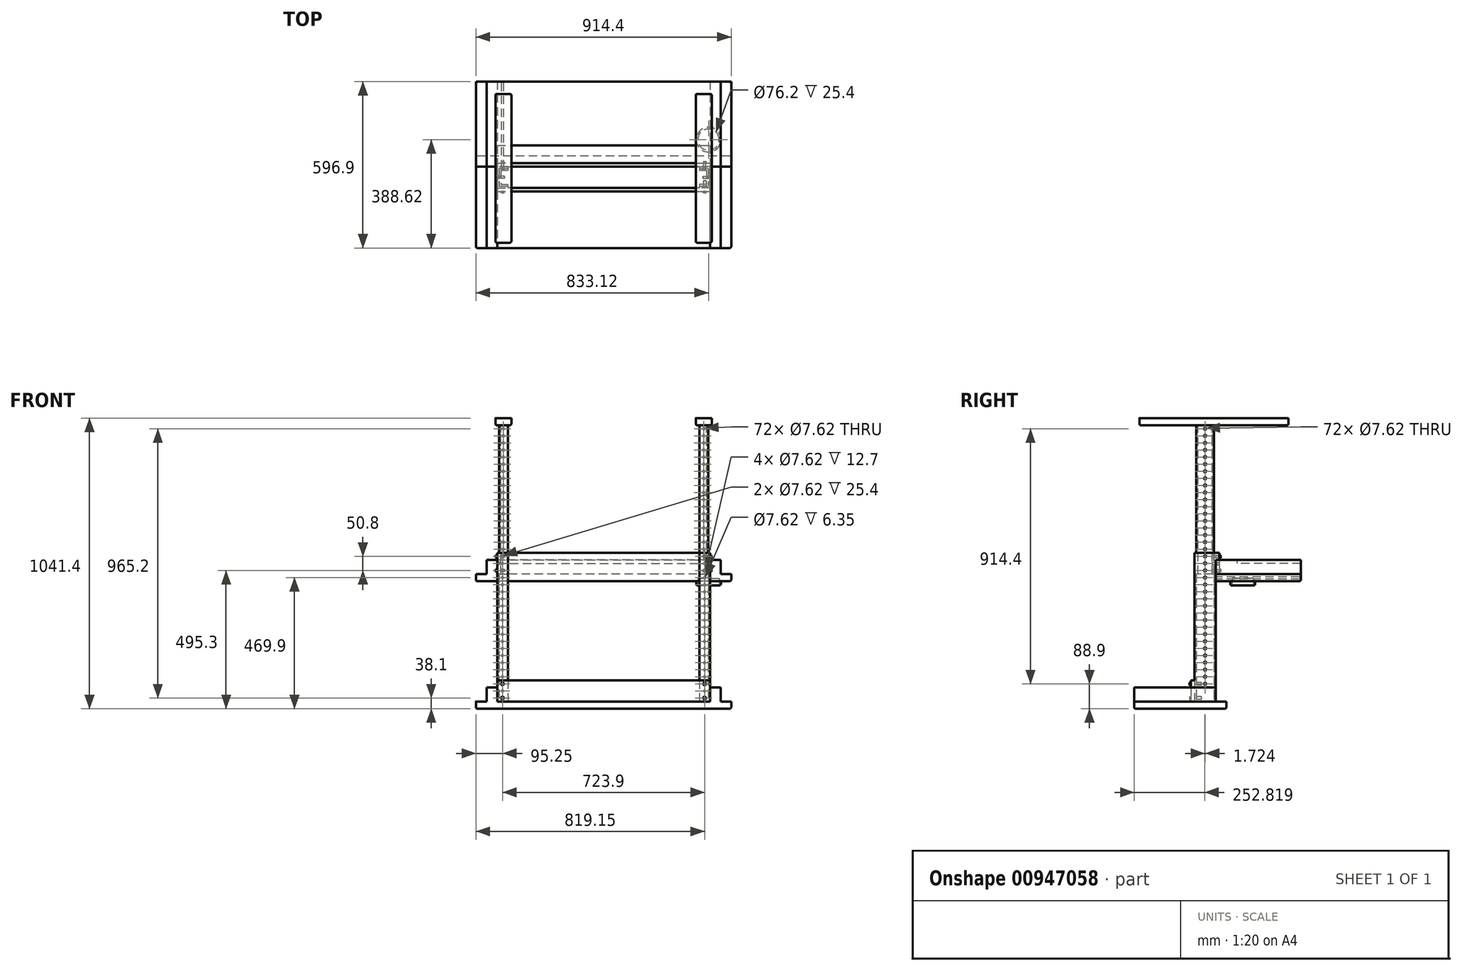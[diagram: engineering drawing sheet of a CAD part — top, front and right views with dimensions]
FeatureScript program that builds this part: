
annotation { "Feature Type Name" : "Feature", "Feature Type Description" : "" }
export const myFeature = defineFeature(function(context is Context, id is Id, definition is map)
    precondition{}
    {
        {
            var Q0;
            Q0=qCreatedBy(makeId("Top.planeOp"),FACE);
            var sketch = newSketch(context, id + "F0", { "sketchPlane" : qUnion([Q0])});
            skLineSegment(sketch, "E0.bottom", {"start": v(457.2, -165.1) * mm, "end": v(-457.2, -165.1) * mm});
            skLineSegment(sketch, "E0.top", {"start": v(457.2, 165.1) * mm, "end": v(-457.2, 165.1) * mm});
            skLineSegment(sketch, "E0.left", {"start": v(457.2, -165.1) * mm, "end": v(457.2, 165.1) * mm});
            skLineSegment(sketch, "E0.right", {"start": v(-457.2, -165.1) * mm, "end": v(-457.2, 165.1) * mm});
            skPoint(sketch, "E0.middle", {"position": v(0, 0) * mm});
            skSolve(sketch);
        }
        {
            var Q0;
            Q0=makeQuery(id+"F0.imprint","IMPRINT",FACE,{"disambiguationData":[TD([[makeQuery(id+"F0.imprint","IMPRINT",EDGE,{"derivedFrom":sQuery(id+"F0.wireOp",EDGE,"E0.bottom")}),-1.0]])]});
            extrude(context, id + "F1", {"entities" : qUnion([Q0]), "depth" : 25.4 * mm, "offsetDistance" : 25.4 * mm});
        }
        {
            var Q0;
            Q0=makeQuery(id+"F1.opExtrude","CAP_FACE",FACE,{"disambiguationData":[OSD([sQuery(id+"F0.wireOp",EDGE,"E0.bottom"),sQuery(id+"F0.wireOp",EDGE,"E0.top"),sQuery(id+"F0.wireOp",EDGE,"E0.left"),sQuery(id+"F0.wireOp",EDGE,"E0.right")])],"isStart":false});
            var sketch = newSketch(context, id + "F2", { "sketchPlane" : qUnion([Q0])});
            skLineSegment(sketch, "E1.bottom", {"start": v(-457.2, 165.1) * mm, "end": v(-381, 165.1) * mm});
            skLineSegment(sketch, "E1.top", {"start": v(-457.2, -165.1) * mm, "end": v(-381, -165.1) * mm});
            skLineSegment(sketch, "E1.left", {"start": v(-457.2, 165.1) * mm, "end": v(-457.2, -165.1) * mm});
            skLineSegment(sketch, "E1.right", {"start": v(-381, 165.1) * mm, "end": v(-381, -165.1) * mm});
            skLineSegment(sketch, "E2.bottom", {"start": v(457.2, -165.1) * mm, "end": v(381, -165.1) * mm});
            skLineSegment(sketch, "E2.top", {"start": v(457.2, 165.1) * mm, "end": v(381, 165.1) * mm});
            skLineSegment(sketch, "E2.left", {"start": v(457.2, -165.1) * mm, "end": v(457.2, 165.1) * mm});
            skLineSegment(sketch, "E2.right", {"start": v(381, -165.1) * mm, "end": v(381, 165.1) * mm});
            skLineSegment(sketch, "E3.bottom", {"start": v(-381, -165.1) * mm, "end": v(-419.1, -165.1) * mm});
            skLineSegment(sketch, "E3.top", {"start": v(-381, 165.1) * mm, "end": v(-419.1, 165.1) * mm});
            skLineSegment(sketch, "E3.left", {"start": v(-381, -165.1) * mm, "end": v(-381, 165.1) * mm});
            skLineSegment(sketch, "E3.right", {"start": v(-419.1, -165.1) * mm, "end": v(-419.1, 165.1) * mm});
            skLineSegment(sketch, "E4.bottom", {"start": v(381, 165.1) * mm, "end": v(419.1, 165.1) * mm});
            skLineSegment(sketch, "E4.top", {"start": v(381, -165.1) * mm, "end": v(419.1, -165.1) * mm});
            skLineSegment(sketch, "E4.left", {"start": v(381, 165.1) * mm, "end": v(381, -165.1) * mm});
            skLineSegment(sketch, "E4.right", {"start": v(419.1, 165.1) * mm, "end": v(419.1, -165.1) * mm});
            skLineSegment(sketch, "E5.bottom", {"start": v(-457.2, 165.1) * mm, "end": v(457.2, 165.1) * mm});
            skLineSegment(sketch, "E5.top", {"start": v(-457.2, 127) * mm, "end": v(457.2, 127) * mm});
            skLineSegment(sketch, "E5.left", {"start": v(-457.2, 165.1) * mm, "end": v(-457.2, 127) * mm});
            skLineSegment(sketch, "E5.right", {"start": v(457.2, 165.1) * mm, "end": v(457.2, 127) * mm});
            skLineSegment(sketch, "E6.bottom", {"start": v(-381, 127) * mm, "end": v(-342.9, 127) * mm});
            skLineSegment(sketch, "E6.top", {"start": v(-381, 50.8) * mm, "end": v(-342.9, 50.8) * mm});
            skLineSegment(sketch, "E6.left", {"start": v(-381, 127) * mm, "end": v(-381, 50.8) * mm});
            skLineSegment(sketch, "E6.right", {"start": v(-342.9, 127) * mm, "end": v(-342.9, 50.8) * mm});
            skLineSegment(sketch, "E7.bottom", {"start": v(381, 127) * mm, "end": v(342.9, 127) * mm});
            skLineSegment(sketch, "E7.top", {"start": v(381, 50.8) * mm, "end": v(342.9, 50.8) * mm});
            skLineSegment(sketch, "E7.left", {"start": v(381, 127) * mm, "end": v(381, 50.8) * mm});
            skLineSegment(sketch, "E7.right", {"start": v(342.9, 127) * mm, "end": v(342.9, 50.8) * mm});
            skLineSegment(sketch, "E8.bottom", {"start": v(342.9, 127) * mm, "end": v(381, 127) * mm});
            skLineSegment(sketch, "E8.top", {"start": v(342.9, 120.65) * mm, "end": v(381, 120.65) * mm});
            skLineSegment(sketch, "E8.left", {"start": v(342.9, 127) * mm, "end": v(342.9, 120.65) * mm});
            skLineSegment(sketch, "E8.right", {"start": v(381, 127) * mm, "end": v(381, 120.65) * mm});
            skLineSegment(sketch, "E9.bottom", {"start": v(342.9, 50.8) * mm, "end": v(381, 50.8) * mm});
            skLineSegment(sketch, "E9.top", {"start": v(342.9, 57.15) * mm, "end": v(381, 57.15) * mm});
            skLineSegment(sketch, "E9.left", {"start": v(342.9, 50.8) * mm, "end": v(342.9, 57.15) * mm});
            skLineSegment(sketch, "E9.right", {"start": v(381, 50.8) * mm, "end": v(381, 57.15) * mm});
            skLineSegment(sketch, "E10.bottom", {"start": v(381, 120.65) * mm, "end": v(374.65, 120.65) * mm});
            skLineSegment(sketch, "E10.top", {"start": v(381, 57.15) * mm, "end": v(374.65, 57.15) * mm});
            skLineSegment(sketch, "E10.left", {"start": v(381, 120.65) * mm, "end": v(381, 57.15) * mm});
            skLineSegment(sketch, "E10.right", {"start": v(374.65, 120.65) * mm, "end": v(374.65, 57.15) * mm});
            skLineSegment(sketch, "E11.top", {"start": v(-381, 120.65) * mm, "end": v(-342.9, 120.65) * mm});
            skLineSegment(sketch, "E11.left", {"start": v(-381, 127) * mm, "end": v(-381, 120.65) * mm});
            skLineSegment(sketch, "E11.right", {"start": v(-342.9, 127) * mm, "end": v(-342.9, 120.65) * mm});
            skLineSegment(sketch, "E12.top", {"start": v(-381, 57.15) * mm, "end": v(-342.9, 57.15) * mm});
            skLineSegment(sketch, "E12.left", {"start": v(-381, 50.8) * mm, "end": v(-381, 57.15) * mm});
            skLineSegment(sketch, "E12.right", {"start": v(-342.9, 50.8) * mm, "end": v(-342.9, 57.15) * mm});
            skLineSegment(sketch, "E13.bottom", {"start": v(-381, 120.65) * mm, "end": v(-374.65, 120.65) * mm});
            skLineSegment(sketch, "E13.top", {"start": v(-381, 57.15) * mm, "end": v(-374.65, 57.15) * mm});
            skLineSegment(sketch, "E13.left", {"start": v(-381, 120.65) * mm, "end": v(-381, 57.15) * mm});
            skLineSegment(sketch, "E13.right", {"start": v(-374.65, 120.65) * mm, "end": v(-374.65, 57.15) * mm});
            skLineSegment(sketch, "E14.bottom", {"start": v(-381, 50.8) * mm, "end": v(381, 50.8) * mm});
            skLineSegment(sketch, "E14.top", {"start": v(-381, 38.1) * mm, "end": v(381, 38.1) * mm});
            skLineSegment(sketch, "E14.left", {"start": v(-381, 50.8) * mm, "end": v(-381, 38.1) * mm});
            skLineSegment(sketch, "E14.right", {"start": v(381, 50.8) * mm, "end": v(381, 38.1) * mm});
            skSolve(sketch);
        }
        {
            var Q0;
            {var subQ0=sQuery(id+"F2.wireOp",EDGE,"E1.right");var subQ5=makeQuery(id+"F2.imprint","INTERSECT",VERTEX,{"derivedFrom":[subQ0,sQuery(id+"F2.wireOp",EDGE,"E11.top")]});Q0=makeQuery(id+"F2.imprint","IMPRINT",FACE,{"disambiguationData":[TD([[makeQuery(id+"F2.imprint","IMPRINT",EDGE,{"disambiguationData":[TD([[subQ5,-1.0]])],"derivedFrom":subQ0}),-1.0]])]});}
            var Q1;
            {var subQ0=sQuery(id+"F2.wireOp",EDGE,"E2.right");var subQ3=makeQuery(id+"F2.imprint","INTERSECT",VERTEX,{"derivedFrom":[subQ0,sQuery(id+"F2.wireOp",EDGE,"E8.top")]});Q1=makeQuery(id+"F2.imprint","IMPRINT",FACE,{"disambiguationData":[TD([[makeQuery(id+"F2.imprint","IMPRINT",EDGE,{"disambiguationData":[TD([[subQ3,1.0]])],"derivedFrom":subQ0}),-1.0]])]});}
            extrude(context, id + "F3", {"entities" : qUnion([Q0, Q1]), "operationType" : NewBodyOperationType.ADD, "depth" : 50.8 * mm, "offsetDistance" : 25.4 * mm});
        }
        {
            var Q0;
            {var subQ1=sQuery(id+"F2.wireOp",EDGE,"E6.top");Q0=makeQuery(id+"F2.imprint","IMPRINT",FACE,{"disambiguationData":[TD([[makeQuery(id+"F2.imprint","IMPRINT",EDGE,{"derivedFrom":subQ1}),-1.0]])]});}
            extrude(context, id + "F4", {"entities" : qUnion([Q0]), "operationType" : NewBodyOperationType.ADD, "depth" : 76.2 * mm, "offsetDistance" : 25.4 * mm});
        }
        {
            var Q0;
            {var subQ5=sQuery(id+"F2.wireOp",EDGE,"E13.right");Q0=makeQuery(id+"F2.imprint","IMPRINT",FACE,{"disambiguationData":[TD([[makeQuery(id+"F2.imprint","IMPRINT",EDGE,{"derivedFrom":subQ5}),-1.0]])]});}
            var Q1;
            {var subQ0=sQuery(id+"F2.wireOp",EDGE,"E11.top");var subQ6=sQuery(id+"F2.wireOp",EDGE,"E1.right");var subQ7=makeQuery(id+"F2.imprint","INTERSECT",VERTEX,{"derivedFrom":[subQ6,subQ0]});Q1=makeQuery(id+"F2.imprint","IMPRINT",FACE,{"disambiguationData":[TD([[makeQuery(id+"F2.imprint","IMPRINT",EDGE,{"disambiguationData":[TD([[subQ7,1.0]])],"derivedFrom":subQ6}),1.0]])]});}
            var Q2;
            {var subQ1=sQuery(id+"F2.wireOp",EDGE,"E6.top");Q2=makeQuery(id+"F2.imprint","IMPRINT",FACE,{"disambiguationData":[TD([[makeQuery(id+"F2.imprint","IMPRINT",EDGE,{"derivedFrom":subQ1}),1.0]])]});}
            var Q3;
            {var subQ4=sQuery(id+"F2.wireOp",EDGE,"E5.top");var subQ5=sQuery(id+"F2.wireOp",EDGE,"E2.right");var subQ6=makeQuery(id+"F2.imprint","INTERSECT",VERTEX,{"derivedFrom":[subQ5,subQ4]});Q3=makeQuery(id+"F2.imprint","IMPRINT",FACE,{"disambiguationData":[TD([[makeQuery(id+"F2.imprint","IMPRINT",EDGE,{"disambiguationData":[TD([[subQ6,1.0]])],"derivedFrom":subQ5}),1.0]])]});}
            var Q4;
            {var subQ5=sQuery(id+"F2.wireOp",EDGE,"E10.right");Q4=makeQuery(id+"F2.imprint","IMPRINT",FACE,{"disambiguationData":[TD([[makeQuery(id+"F2.imprint","IMPRINT",EDGE,{"derivedFrom":subQ5}),1.0]])]});}
            var Q5;
            {var subQ4=sQuery(id+"F2.wireOp",EDGE,"E7.top");Q5=makeQuery(id+"F2.imprint","IMPRINT",FACE,{"disambiguationData":[TD([[makeQuery(id+"F2.imprint","IMPRINT",EDGE,{"derivedFrom":subQ4}),-1.0]])]});}
            extrude(context, id + "F5", {"entities" : qUnion([Q0, Q1, Q2, Q3, Q4, Q5]), "operationType" : NewBodyOperationType.ADD, "depth" : 533.4 * mm, "offsetDistance" : 25.4 * mm});
        }
        {
            var Q0;
            Q0=makeQuery(id+"F4.opExtrude","SWEPT_FACE",FACE,{"disambiguationData":[OSD([sQuery(id+"F2.wireOp",EDGE,"E14.top")])]});
            var sketch = newSketch(context, id + "F6", { "sketchPlane" : qUnion([Q0])});
            skLineSegment(sketch, "E15.bottom", {"start": v(-381, 25.4) * mm, "end": v(-342.9, 25.4) * mm});
            skLineSegment(sketch, "E15.top", {"start": v(-381, 101.6) * mm, "end": v(-342.9, 101.6) * mm});
            skLineSegment(sketch, "E15.left", {"start": v(-381, 25.4) * mm, "end": v(-381, 101.6) * mm});
            skLineSegment(sketch, "E15.right", {"start": v(-342.9, 25.4) * mm, "end": v(-342.9, 101.6) * mm});
            skLineSegment(sketch, "E16.bottom", {"start": v(-342.9, 25.4) * mm, "end": v(-381, 25.4) * mm});
            skLineSegment(sketch, "E16.top", {"start": v(-342.9, 50.8) * mm, "end": v(-381, 50.8) * mm});
            skLineSegment(sketch, "E16.left", {"start": v(-342.9, 25.4) * mm, "end": v(-342.9, 50.8) * mm});
            skLineSegment(sketch, "E16.right", {"start": v(-381, 25.4) * mm, "end": v(-381, 50.8) * mm});
            skLineSegment(sketch, "E17.top", {"start": v(-342.9, 76.2) * mm, "end": v(-381, 76.2) * mm});
            skLineSegment(sketch, "E17.left", {"start": v(-342.9, 50.8) * mm, "end": v(-342.9, 76.2) * mm});
            skLineSegment(sketch, "E17.right", {"start": v(-381, 50.8) * mm, "end": v(-381, 76.2) * mm});
            skCircle(sketch, "E18", {"center": v(-361.95, 38.1) * mm, "radius": 5.08 * mm});
            skCircle(sketch, "E19", {"center": v(-361.95, 88.9) * mm, "radius": 5.08 * mm});
            skLineSegment(sketch, "E20.bottom", {"start": v(381, 101.6) * mm, "end": v(342.9, 101.6) * mm});
            skLineSegment(sketch, "E20.top", {"start": v(381, 25.4) * mm, "end": v(342.9, 25.4) * mm});
            skLineSegment(sketch, "E20.left", {"start": v(381, 101.6) * mm, "end": v(381, 25.4) * mm});
            skLineSegment(sketch, "E20.right", {"start": v(342.9, 101.6) * mm, "end": v(342.9, 25.4) * mm});
            skLineSegment(sketch, "E21.bottom", {"start": v(342.9, 101.6) * mm, "end": v(381, 101.6) * mm});
            skLineSegment(sketch, "E21.top", {"start": v(342.9, 76.2) * mm, "end": v(381, 76.2) * mm});
            skLineSegment(sketch, "E21.left", {"start": v(342.9, 101.6) * mm, "end": v(342.9, 76.2) * mm});
            skLineSegment(sketch, "E21.right", {"start": v(381, 101.6) * mm, "end": v(381, 76.2) * mm});
            skLineSegment(sketch, "E22.top", {"start": v(342.9, 50.8) * mm, "end": v(381, 50.8) * mm});
            skLineSegment(sketch, "E22.left", {"start": v(342.9, 76.2) * mm, "end": v(342.9, 50.8) * mm});
            skLineSegment(sketch, "E22.right", {"start": v(381, 76.2) * mm, "end": v(381, 50.8) * mm});
            skCircle(sketch, "E23", {"center": v(361.95, 88.9) * mm, "radius": 5.08 * mm});
            skCircle(sketch, "E24", {"center": v(361.95, 38.1) * mm, "radius": 5.08 * mm});
            skSolve(sketch);
        }
        {
            var Q0;
            Q0=makeQuery(id+"F6.imprint","IMPRINT",FACE,{"disambiguationData":[TD([[makeQuery(id+"F6.imprint","IMPRINT",EDGE,{"derivedFrom":sQuery(id+"F6.wireOp",EDGE,"E19")}),1.0]])]});
            var Q1;
            Q1=makeQuery(id+"F6.imprint","IMPRINT",FACE,{"disambiguationData":[TD([[makeQuery(id+"F6.imprint","IMPRINT",EDGE,{"derivedFrom":sQuery(id+"F6.wireOp",EDGE,"E18")}),1.0]])]});
            var Q2;
            Q2=makeQuery(id+"F6.imprint","IMPRINT",FACE,{"disambiguationData":[TD([[makeQuery(id+"F6.imprint","IMPRINT",EDGE,{"derivedFrom":sQuery(id+"F6.wireOp",EDGE,"E23")}),1.0]])]});
            var Q3;
            Q3=makeQuery(id+"F6.imprint","IMPRINT",FACE,{"disambiguationData":[TD([[makeQuery(id+"F6.imprint","IMPRINT",EDGE,{"derivedFrom":sQuery(id+"F6.wireOp",EDGE,"E24")}),1.0]])]});
            extrude(context, id + "F7", {"entities" : qUnion([Q0, Q1, Q2, Q3]), "operationType" : NewBodyOperationType.ADD, "depth" : 5.08 * mm, "offsetDistance" : 25.4 * mm});
        }
        {
            var Q0;
            Q0=makeQuery(id+"F5.opExtrude","CAP_FACE",FACE,{"disambiguationData":[OSD([sQuery(id+"F2.wireOp",EDGE,"E2.right"),sQuery(id+"F2.wireOp",EDGE,"E5.top"),sQuery(id+"F2.wireOp",EDGE,"E7.top"),sQuery(id+"F2.wireOp",EDGE,"E7.right"),sQuery(id+"F2.wireOp",EDGE,"E8.top"),sQuery(id+"F2.wireOp",EDGE,"E9.top"),sQuery(id+"F2.wireOp",EDGE,"E10.right")])],"isStart":false});
            var sketch = newSketch(context, id + "F8", { "sketchPlane" : qUnion([Q0])});
            skLineSegment(sketch, "E25.bottom", {"start": v(342.9, 120.65) * mm, "end": v(374.65, 120.65) * mm});
            skLineSegment(sketch, "E25.top", {"start": v(342.9, 57.15) * mm, "end": v(374.65, 57.15) * mm});
            skLineSegment(sketch, "E25.left", {"start": v(342.9, 120.65) * mm, "end": v(342.9, 57.15) * mm});
            skLineSegment(sketch, "E25.right", {"start": v(374.65, 120.65) * mm, "end": v(374.65, 57.15) * mm});
            skLineSegment(sketch, "E26.top", {"start": v(342.9, 114.3) * mm, "end": v(374.65, 114.3) * mm});
            skLineSegment(sketch, "E26.left", {"start": v(342.9, 120.65) * mm, "end": v(342.9, 114.3) * mm});
            skLineSegment(sketch, "E26.right", {"start": v(374.65, 120.65) * mm, "end": v(374.65, 114.3) * mm});
            skLineSegment(sketch, "E27.bottom", {"start": v(374.65, 120.65) * mm, "end": v(368.3, 120.65) * mm});
            skLineSegment(sketch, "E27.top", {"start": v(374.65, 57.15) * mm, "end": v(368.3, 57.15) * mm});
            skLineSegment(sketch, "E27.right", {"start": v(368.3, 120.65) * mm, "end": v(368.3, 57.15) * mm});
            skLineSegment(sketch, "E28.bottom", {"start": v(374.65, 57.15) * mm, "end": v(342.9, 57.15) * mm});
            skLineSegment(sketch, "E28.top", {"start": v(374.65, 63.5) * mm, "end": v(342.9, 63.5) * mm});
            skLineSegment(sketch, "E28.left", {"start": v(374.65, 57.15) * mm, "end": v(374.65, 63.5) * mm});
            skLineSegment(sketch, "E28.right", {"start": v(342.9, 57.15) * mm, "end": v(342.9, 63.5) * mm});
            skSolve(sketch);
        }
        {
            var Q0;
            {var subQ0=sQuery(id+"F8.wireOp",EDGE,"E25.left");var subQ6=sQuery(id+"F8.wireOp",EDGE,"E26.top");var subQ7=makeQuery(id+"F8.imprint","INTERSECT",VERTEX,{"derivedFrom":[subQ0,subQ6]});Q0=makeQuery(id+"F8.imprint","IMPRINT",FACE,{"disambiguationData":[TD([[makeQuery(id+"F8.imprint","IMPRINT",EDGE,{"disambiguationData":[TD([[subQ7,-1.0]])],"derivedFrom":subQ6}),1.0]])]});}
            var Q1;
            {var subQ1=sQuery(id+"F8.wireOp",EDGE,"E25.top");var subQ4=sQuery(id+"F8.wireOp",EDGE,"E27.right");var subQ5=makeQuery(id+"F8.imprint","INTERSECT",VERTEX,{"derivedFrom":[subQ1,subQ4]});Q1=makeQuery(id+"F8.imprint","IMPRINT",FACE,{"disambiguationData":[TD([[makeQuery(id+"F8.imprint","IMPRINT",EDGE,{"disambiguationData":[TD([[subQ5,1.0]])],"derivedFrom":subQ4}),-1.0]])]});}
            var Q2;
            {var subQ0=sQuery(id+"F8.wireOp",EDGE,"E25.right");var subQ1=sQuery(id+"F8.wireOp",EDGE,"E25.top");var subQ2=makeQuery(id+"F8.imprint","INTERSECT",VERTEX,{"derivedFrom":[subQ1,subQ0]});Q2=makeQuery(id+"F8.imprint","IMPRINT",FACE,{"disambiguationData":[TD([[makeQuery(id+"F8.imprint","IMPRINT",EDGE,{"disambiguationData":[TD([[subQ2,1.0]])],"derivedFrom":subQ1}),1.0]])]});}
            var Q3;
            {var subQ0=sQuery(id+"F8.wireOp",EDGE,"E26.top");var subQ1=sQuery(id+"F8.wireOp",EDGE,"E25.right");var subQ2=makeQuery(id+"F8.imprint","INTERSECT",VERTEX,{"derivedFrom":[subQ1,subQ0]});Q3=makeQuery(id+"F8.imprint","IMPRINT",FACE,{"disambiguationData":[TD([[makeQuery(id+"F8.imprint","IMPRINT",EDGE,{"disambiguationData":[TD([[subQ2,-1.0]])],"derivedFrom":subQ1}),-1.0]])]});}
            var Q4;
            {var subQ0=sQuery(id+"F8.wireOp",EDGE,"E25.right");var subQ1=sQuery(id+"F8.wireOp",EDGE,"E25.bottom");var subQ2=makeQuery(id+"F8.imprint","INTERSECT",VERTEX,{"derivedFrom":[subQ1,subQ0]});Q4=makeQuery(id+"F8.imprint","IMPRINT",FACE,{"disambiguationData":[TD([[makeQuery(id+"F8.imprint","IMPRINT",EDGE,{"disambiguationData":[TD([[subQ2,1.0]])],"derivedFrom":subQ1}),-1.0]])]});}
            extrude(context, id + "F9", {"entities" : qUnion([Q0, Q1, Q2, Q3, Q4]), "operationType" : NewBodyOperationType.ADD, "depth" : -76.2 * mm, "offsetDistance" : 25.4 * mm});
        }
        {
            var Q0;
            {var subQ0=sQuery(id+"F8.wireOp",EDGE,"E25.left");var subQ6=sQuery(id+"F8.wireOp",EDGE,"E26.top");var subQ7=makeQuery(id+"F8.imprint","INTERSECT",VERTEX,{"derivedFrom":[subQ0,subQ6]});Q0=makeQuery(id+"F8.imprint","IMPRINT",FACE,{"disambiguationData":[TD([[makeQuery(id+"F8.imprint","IMPRINT",EDGE,{"disambiguationData":[TD([[subQ7,-1.0]])],"derivedFrom":subQ6}),1.0]])]});}
            var Q1;
            {var subQ0=sQuery(id+"F8.wireOp",EDGE,"E25.right");var subQ1=sQuery(id+"F8.wireOp",EDGE,"E25.bottom");var subQ2=makeQuery(id+"F8.imprint","INTERSECT",VERTEX,{"derivedFrom":[subQ1,subQ0]});Q1=makeQuery(id+"F8.imprint","IMPRINT",FACE,{"disambiguationData":[TD([[makeQuery(id+"F8.imprint","IMPRINT",EDGE,{"disambiguationData":[TD([[subQ2,1.0]])],"derivedFrom":subQ1}),-1.0]])]});}
            var Q2;
            {var subQ0=sQuery(id+"F8.wireOp",EDGE,"E26.top");var subQ1=sQuery(id+"F8.wireOp",EDGE,"E25.right");var subQ2=makeQuery(id+"F8.imprint","INTERSECT",VERTEX,{"derivedFrom":[subQ1,subQ0]});Q2=makeQuery(id+"F8.imprint","IMPRINT",FACE,{"disambiguationData":[TD([[makeQuery(id+"F8.imprint","IMPRINT",EDGE,{"disambiguationData":[TD([[subQ2,-1.0]])],"derivedFrom":subQ1}),-1.0]])]});}
            var Q3;
            {var subQ0=sQuery(id+"F8.wireOp",EDGE,"E25.right");var subQ1=sQuery(id+"F8.wireOp",EDGE,"E25.top");var subQ2=makeQuery(id+"F8.imprint","INTERSECT",VERTEX,{"derivedFrom":[subQ1,subQ0]});Q3=makeQuery(id+"F8.imprint","IMPRINT",FACE,{"disambiguationData":[TD([[makeQuery(id+"F8.imprint","IMPRINT",EDGE,{"disambiguationData":[TD([[subQ2,1.0]])],"derivedFrom":subQ1}),1.0]])]});}
            var Q4;
            {var subQ1=sQuery(id+"F8.wireOp",EDGE,"E25.top");var subQ4=sQuery(id+"F8.wireOp",EDGE,"E27.right");var subQ5=makeQuery(id+"F8.imprint","INTERSECT",VERTEX,{"derivedFrom":[subQ1,subQ4]});Q4=makeQuery(id+"F8.imprint","IMPRINT",FACE,{"disambiguationData":[TD([[makeQuery(id+"F8.imprint","IMPRINT",EDGE,{"disambiguationData":[TD([[subQ5,1.0]])],"derivedFrom":subQ4}),-1.0]])]});}
            extrude(context, id + "F10", {"entities" : qUnion([Q0, Q1, Q2, Q3, Q4]), "operationType" : NewBodyOperationType.ADD, "depth" : 457.2 * mm, "offsetDistance" : 25.4 * mm});
        }
        {
            var Q0;
            Q0=makeQuery(id+"F5.opExtrude","CAP_FACE",FACE,{"disambiguationData":[OSD([sQuery(id+"F2.wireOp",EDGE,"E1.right"),sQuery(id+"F2.wireOp",EDGE,"E5.top"),sQuery(id+"F2.wireOp",EDGE,"E6.top"),sQuery(id+"F2.wireOp",EDGE,"E6.right"),sQuery(id+"F2.wireOp",EDGE,"E11.top"),sQuery(id+"F2.wireOp",EDGE,"E12.top"),sQuery(id+"F2.wireOp",EDGE,"E13.right")])],"isStart":false});
            var sketch = newSketch(context, id + "F11", { "sketchPlane" : qUnion([Q0])});
            skLineSegment(sketch, "E29.bottom", {"start": v(-374.65, 120.65) * mm, "end": v(-342.86, 120.65) * mm});
            skLineSegment(sketch, "E29.top", {"start": v(-374.65, 114.3) * mm, "end": v(-342.86, 114.3) * mm});
            skLineSegment(sketch, "E29.left", {"start": v(-374.65, 120.65) * mm, "end": v(-374.65, 114.3) * mm});
            skLineSegment(sketch, "E29.right", {"start": v(-342.86, 120.65) * mm, "end": v(-342.86, 114.3) * mm});
            skLineSegment(sketch, "E30.bottom", {"start": v(-374.65, 120.65) * mm, "end": v(-368.3, 120.65) * mm});
            skLineSegment(sketch, "E30.top", {"start": v(-374.65, 57.15) * mm, "end": v(-368.3, 57.15) * mm});
            skLineSegment(sketch, "E30.left", {"start": v(-374.65, 120.65) * mm, "end": v(-374.65, 57.15) * mm});
            skLineSegment(sketch, "E30.right", {"start": v(-368.3, 120.65) * mm, "end": v(-368.3, 57.15) * mm});
            skLineSegment(sketch, "E31.bottom", {"start": v(-374.65, 57.15) * mm, "end": v(-342.9, 57.15) * mm});
            skLineSegment(sketch, "E31.top", {"start": v(-374.65, 63.5) * mm, "end": v(-342.9, 63.5) * mm});
            skLineSegment(sketch, "E31.left", {"start": v(-374.65, 57.15) * mm, "end": v(-374.65, 63.5) * mm});
            skLineSegment(sketch, "E31.right", {"start": v(-342.9, 57.15) * mm, "end": v(-342.9, 63.5) * mm});
            skSolve(sketch);
        }
        {
            var Q0;
            {var subQ0=sQuery(id+"F11.wireOp",EDGE,"E29.left");Q0=makeQuery(id+"F11.imprint","IMPRINT",FACE,{"disambiguationData":[TD([[makeQuery(id+"F11.imprint","IMPRINT",EDGE,{"derivedFrom":subQ0}),1.0]])]});}
            var Q1;
            {var subQ3=sQuery(id+"F11.wireOp",EDGE,"E29.right");Q1=makeQuery(id+"F11.imprint","IMPRINT",FACE,{"disambiguationData":[TD([[makeQuery(id+"F11.imprint","IMPRINT",EDGE,{"derivedFrom":subQ3}),-1.0]])]});}
            var Q2;
            {var subQ0=sQuery(id+"F11.wireOp",EDGE,"E30.right");var subQ1=sQuery(id+"F11.wireOp",EDGE,"E29.top");var subQ2=makeQuery(id+"F11.imprint","INTERSECT",VERTEX,{"derivedFrom":[subQ1,subQ0]});Q2=makeQuery(id+"F11.imprint","IMPRINT",FACE,{"disambiguationData":[TD([[makeQuery(id+"F11.imprint","IMPRINT",EDGE,{"disambiguationData":[TD([[subQ2,-1.0]])],"derivedFrom":subQ0}),-1.0]])]});}
            var Q3;
            {var subQ0=sQuery(id+"F11.wireOp",EDGE,"E30.top");Q3=makeQuery(id+"F11.imprint","IMPRINT",FACE,{"disambiguationData":[TD([[makeQuery(id+"F11.imprint","IMPRINT",EDGE,{"derivedFrom":subQ0}),1.0]])]});}
            var Q4;
            {var subQ0=sQuery(id+"F11.wireOp",EDGE,"E31.bottom");Q4=makeQuery(id+"F11.imprint","IMPRINT",FACE,{"disambiguationData":[TD([[makeQuery(id+"F11.imprint","IMPRINT",EDGE,{"derivedFrom":subQ0}),1.0]])]});}
            extrude(context, id + "F12", {"entities" : qUnion([Q0, Q1, Q2, Q3, Q4]), "operationType" : NewBodyOperationType.ADD, "depth" : -76.2 * mm, "offsetDistance" : 25.4 * mm});
        }
        {
            var Q0;
            {var subQ3=sQuery(id+"F11.wireOp",EDGE,"E29.right");Q0=makeQuery(id+"F11.imprint","IMPRINT",FACE,{"disambiguationData":[TD([[makeQuery(id+"F11.imprint","IMPRINT",EDGE,{"derivedFrom":subQ3}),-1.0]])]});}
            var Q1;
            {var subQ0=sQuery(id+"F11.wireOp",EDGE,"E29.left");Q1=makeQuery(id+"F11.imprint","IMPRINT",FACE,{"disambiguationData":[TD([[makeQuery(id+"F11.imprint","IMPRINT",EDGE,{"derivedFrom":subQ0}),1.0]])]});}
            var Q2;
            {var subQ0=sQuery(id+"F11.wireOp",EDGE,"E30.right");var subQ1=sQuery(id+"F11.wireOp",EDGE,"E29.top");var subQ2=makeQuery(id+"F11.imprint","INTERSECT",VERTEX,{"derivedFrom":[subQ1,subQ0]});Q2=makeQuery(id+"F11.imprint","IMPRINT",FACE,{"disambiguationData":[TD([[makeQuery(id+"F11.imprint","IMPRINT",EDGE,{"disambiguationData":[TD([[subQ2,-1.0]])],"derivedFrom":subQ0}),-1.0]])]});}
            var Q3;
            {var subQ0=sQuery(id+"F11.wireOp",EDGE,"E30.top");Q3=makeQuery(id+"F11.imprint","IMPRINT",FACE,{"disambiguationData":[TD([[makeQuery(id+"F11.imprint","IMPRINT",EDGE,{"derivedFrom":subQ0}),1.0]])]});}
            var Q4;
            {var subQ0=sQuery(id+"F11.wireOp",EDGE,"E31.bottom");Q4=makeQuery(id+"F11.imprint","IMPRINT",FACE,{"disambiguationData":[TD([[makeQuery(id+"F11.imprint","IMPRINT",EDGE,{"derivedFrom":subQ0}),1.0]])]});}
            extrude(context, id + "F13", {"entities" : qUnion([Q0, Q1, Q2, Q3, Q4]), "operationType" : NewBodyOperationType.ADD, "depth" : 457.2 * mm, "offsetDistance" : 25.4 * mm});
        }
        {
            var Q0;
            {var subQ0=sQuery(id+"F2.wireOp",EDGE,"E1.right");Q0=makeQuery(id+"F5.boolean.opBoolean","MERGE",FACE,{"derivedFrom":[makeQuery(id+"F4.opExtrude","SWEPT_FACE",FACE,{"disambiguationData":[OSD([subQ0])]}),makeQuery(id+"F5.opExtrude","SWEPT_FACE",FACE,{"disambiguationData":[OSD([subQ0])]})]});}
            var sketch = newSketch(context, id + "F14", { "sketchPlane" : qUnion([Q0])});
            skLineSegment(sketch, "E32.bottom", {"start": v(-127, 558.8) * mm, "end": v(-50.8, 558.8) * mm});
            skLineSegment(sketch, "E32.top", {"start": v(-127, 533.4) * mm, "end": v(-50.8, 533.4) * mm});
            skLineSegment(sketch, "E32.left", {"start": v(-127, 558.8) * mm, "end": v(-127, 533.4) * mm});
            skLineSegment(sketch, "E32.right", {"start": v(-50.8, 558.8) * mm, "end": v(-50.8, 533.4) * mm});
            skLineSegment(sketch, "E33.top", {"start": v(-127, 508) * mm, "end": v(-50.8, 508) * mm});
            skLineSegment(sketch, "E33.left", {"start": v(-127, 533.4) * mm, "end": v(-127, 508) * mm});
            skLineSegment(sketch, "E33.right", {"start": v(-50.8, 533.4) * mm, "end": v(-50.8, 508) * mm});
            skLineSegment(sketch, "E34.top", {"start": v(-127, 482.6) * mm, "end": v(-50.8, 482.6) * mm});
            skLineSegment(sketch, "E34.left", {"start": v(-127, 508) * mm, "end": v(-127, 482.6) * mm});
            skLineSegment(sketch, "E34.right", {"start": v(-50.8, 508) * mm, "end": v(-50.8, 482.6) * mm});
            skLineSegment(sketch, "E35.top", {"start": v(-127, 457.2) * mm, "end": v(-50.8, 457.2) * mm});
            skLineSegment(sketch, "E35.left", {"start": v(-127, 482.6) * mm, "end": v(-127, 457.2) * mm});
            skLineSegment(sketch, "E35.right", {"start": v(-50.8, 482.6) * mm, "end": v(-50.8, 457.2) * mm});
            skLineSegment(sketch, "E36.bottom", {"start": v(-127, 457.2) * mm, "end": v(-48.44, 457.2) * mm});
            skLineSegment(sketch, "E36.top", {"start": v(-127, 431.8) * mm, "end": v(-48.44, 431.8) * mm});
            skLineSegment(sketch, "E36.left", {"start": v(-127, 457.2) * mm, "end": v(-127, 431.8) * mm});
            skLineSegment(sketch, "E36.right", {"start": v(-48.44, 457.2) * mm, "end": v(-48.44, 431.8) * mm});
            skLineSegment(sketch, "E37.bottom", {"start": v(-127, 431.8) * mm, "end": v(-50.8, 431.8) * mm});
            skLineSegment(sketch, "E37.top", {"start": v(-127, 406.4) * mm, "end": v(-50.8, 406.4) * mm});
            skLineSegment(sketch, "E37.left", {"start": v(-127, 431.8) * mm, "end": v(-127, 406.4) * mm});
            skLineSegment(sketch, "E37.right", {"start": v(-50.8, 431.8) * mm, "end": v(-50.8, 406.4) * mm});
            skLineSegment(sketch, "E38.bottom", {"start": v(-127, 406.4) * mm, "end": v(-48.44, 406.4) * mm});
            skLineSegment(sketch, "E38.top", {"start": v(-127, 381) * mm, "end": v(-48.44, 381) * mm});
            skLineSegment(sketch, "E38.left", {"start": v(-127, 406.4) * mm, "end": v(-127, 381) * mm});
            skLineSegment(sketch, "E38.right", {"start": v(-48.44, 406.4) * mm, "end": v(-48.44, 381) * mm});
            skLineSegment(sketch, "E39.bottom", {"start": v(-127, 381) * mm, "end": v(-50.8, 381) * mm});
            skLineSegment(sketch, "E39.top", {"start": v(-127, 355.6) * mm, "end": v(-50.8, 355.6) * mm});
            skLineSegment(sketch, "E39.left", {"start": v(-127, 381) * mm, "end": v(-127, 355.6) * mm});
            skLineSegment(sketch, "E39.right", {"start": v(-50.8, 381) * mm, "end": v(-50.8, 355.6) * mm});
            skLineSegment(sketch, "E40.top", {"start": v(-127, 330.2) * mm, "end": v(-50.8, 330.2) * mm});
            skLineSegment(sketch, "E40.left", {"start": v(-127, 355.6) * mm, "end": v(-127, 330.2) * mm});
            skLineSegment(sketch, "E40.right", {"start": v(-50.8, 355.6) * mm, "end": v(-50.8, 330.2) * mm});
            skLineSegment(sketch, "E41.top", {"start": v(-127, 304.8) * mm, "end": v(-50.8, 304.8) * mm});
            skLineSegment(sketch, "E41.left", {"start": v(-127, 330.2) * mm, "end": v(-127, 304.8) * mm});
            skLineSegment(sketch, "E41.right", {"start": v(-50.8, 330.2) * mm, "end": v(-50.8, 304.8) * mm});
            skLineSegment(sketch, "E42.bottom", {"start": v(-127, 304.8) * mm, "end": v(-48.44, 304.8) * mm});
            skLineSegment(sketch, "E42.top", {"start": v(-127, 279.4) * mm, "end": v(-48.44, 279.4) * mm});
            skLineSegment(sketch, "E42.left", {"start": v(-127, 304.8) * mm, "end": v(-127, 279.4) * mm});
            skLineSegment(sketch, "E42.right", {"start": v(-48.44, 304.8) * mm, "end": v(-48.44, 279.4) * mm});
            skLineSegment(sketch, "E43.bottom", {"start": v(-127, 279.4) * mm, "end": v(-50.8, 279.4) * mm});
            skLineSegment(sketch, "E43.top", {"start": v(-127, 254) * mm, "end": v(-50.8, 254) * mm});
            skLineSegment(sketch, "E43.left", {"start": v(-127, 279.4) * mm, "end": v(-127, 254) * mm});
            skLineSegment(sketch, "E43.right", {"start": v(-50.8, 279.4) * mm, "end": v(-50.8, 254) * mm});
            skLineSegment(sketch, "E44.top", {"start": v(-127, 228.6) * mm, "end": v(-50.8, 228.6) * mm});
            skLineSegment(sketch, "E44.left", {"start": v(-127, 254) * mm, "end": v(-127, 228.6) * mm});
            skLineSegment(sketch, "E44.right", {"start": v(-50.8, 254) * mm, "end": v(-50.8, 228.6) * mm});
            skLineSegment(sketch, "E45.top", {"start": v(-127, 203.2) * mm, "end": v(-50.8, 203.2) * mm});
            skLineSegment(sketch, "E45.left", {"start": v(-127, 228.6) * mm, "end": v(-127, 203.2) * mm});
            skLineSegment(sketch, "E45.right", {"start": v(-50.8, 228.6) * mm, "end": v(-50.8, 203.2) * mm});
            skLineSegment(sketch, "E46.top", {"start": v(-127, 177.8) * mm, "end": v(-50.8, 177.8) * mm});
            skLineSegment(sketch, "E46.left", {"start": v(-127, 203.2) * mm, "end": v(-127, 177.8) * mm});
            skLineSegment(sketch, "E46.right", {"start": v(-50.8, 203.2) * mm, "end": v(-50.8, 177.8) * mm});
            skLineSegment(sketch, "E47.top", {"start": v(-127, 152.4) * mm, "end": v(-50.8, 152.4) * mm});
            skLineSegment(sketch, "E47.left", {"start": v(-127, 177.8) * mm, "end": v(-127, 152.4) * mm});
            skLineSegment(sketch, "E47.right", {"start": v(-50.8, 177.8) * mm, "end": v(-50.8, 152.4) * mm});
            skLineSegment(sketch, "E48.top", {"start": v(-127, 127) * mm, "end": v(-50.8, 127) * mm});
            skLineSegment(sketch, "E48.left", {"start": v(-127, 152.4) * mm, "end": v(-127, 127) * mm});
            skLineSegment(sketch, "E48.right", {"start": v(-50.8, 152.4) * mm, "end": v(-50.8, 127) * mm});
            skLineSegment(sketch, "E49.top", {"start": v(-127, 101.6) * mm, "end": v(-50.8, 101.6) * mm});
            skLineSegment(sketch, "E49.left", {"start": v(-127, 127) * mm, "end": v(-127, 101.6) * mm});
            skLineSegment(sketch, "E49.right", {"start": v(-50.8, 127) * mm, "end": v(-50.8, 101.6) * mm});
            skLineSegment(sketch, "E50.top", {"start": v(-127, 76.2) * mm, "end": v(-50.8, 76.2) * mm});
            skLineSegment(sketch, "E50.left", {"start": v(-127, 101.6) * mm, "end": v(-127, 76.2) * mm});
            skLineSegment(sketch, "E50.right", {"start": v(-50.8, 101.6) * mm, "end": v(-50.8, 76.2) * mm});
            skCircle(sketch, "E51", {"center": v(-89.44, 190.68) * mm, "radius": 3.81 * mm});
            skCircle(sketch, "E52", {"center": v(-88.9, 165.1) * mm, "radius": 3.81 * mm});
            skCircle(sketch, "E53", {"center": v(-88.9, 139.7) * mm, "radius": 3.81 * mm});
            skCircle(sketch, "E54", {"center": v(-88.9, 114.3) * mm, "radius": 3.81 * mm});
            skCircle(sketch, "E55", {"center": v(-88.9, 88.9) * mm, "radius": 3.81 * mm});
            skCircle(sketch, "E56", {"center": v(-88.32, 317.7) * mm, "radius": 3.81 * mm});
            skCircle(sketch, "E57", {"center": v(-88.9, 292.1) * mm, "radius": 3.81 * mm});
            skCircle(sketch, "E58", {"center": v(-88.9, 266.7) * mm, "radius": 3.81 * mm});
            skCircle(sketch, "E59", {"center": v(-88.9, 241.3) * mm, "radius": 3.81 * mm});
            skCircle(sketch, "E60", {"center": v(-88.9, 215.9) * mm, "radius": 3.81 * mm});
            skCircle(sketch, "E61", {"center": v(-87.72, 368.3) * mm, "radius": 3.81 * mm});
            skCircle(sketch, "E62", {"center": v(-88.9, 342.9) * mm, "radius": 3.8 * mm});
            skCircle(sketch, "E63", {"center": v(-88.9, 393.7) * mm, "radius": 3.81 * mm});
            skCircle(sketch, "E64", {"center": v(-87.72, 418.7) * mm, "radius": 3.81 * mm});
            skPoint(sketch, "E64.centerSnap0", {"position": v(-87.72, 406.4) * mm});
            skCircle(sketch, "E65", {"center": v(-88.9, 444.5) * mm, "radius": 3.81 * mm});
            skCircle(sketch, "E66", {"center": v(-88.9, 469.9) * mm, "radius": 3.81 * mm});
            skCircle(sketch, "E67", {"center": v(-88.9, 495.3) * mm, "radius": 3.81 * mm});
            skCircle(sketch, "E68", {"center": v(-88.9, 546.1) * mm, "radius": 3.81 * mm});
            skCircle(sketch, "E69", {"center": v(-88.9, 520.7) * mm, "radius": 3.81 * mm});
            skLineSegment(sketch, "E70.bottom", {"start": v(-50.8, 76.2) * mm, "end": v(-127.37, 76.2) * mm});
            skSolve(sketch);
        }
        {
            var Q0;
            Q0=makeQuery(id+"F14.imprint","IMPRINT",FACE,{"disambiguationData":[TD([[makeQuery(id+"F14.imprint","IMPRINT",EDGE,{"derivedFrom":sQuery(id+"F14.wireOp",EDGE,"E55")}),1.0]])]});
            var Q1;
            Q1=makeQuery(id+"F14.imprint","IMPRINT",FACE,{"disambiguationData":[TD([[makeQuery(id+"F14.imprint","IMPRINT",EDGE,{"derivedFrom":sQuery(id+"F14.wireOp",EDGE,"E54")}),1.0]])]});
            var Q2;
            Q2=makeQuery(id+"F14.imprint","IMPRINT",FACE,{"disambiguationData":[TD([[makeQuery(id+"F14.imprint","IMPRINT",EDGE,{"derivedFrom":sQuery(id+"F14.wireOp",EDGE,"E53")}),1.0]])]});
            var Q3;
            Q3=makeQuery(id+"F14.imprint","IMPRINT",FACE,{"disambiguationData":[TD([[makeQuery(id+"F14.imprint","IMPRINT",EDGE,{"derivedFrom":sQuery(id+"F14.wireOp",EDGE,"E52")}),1.0]])]});
            var Q4;
            Q4=makeQuery(id+"F14.imprint","IMPRINT",FACE,{"disambiguationData":[TD([[makeQuery(id+"F14.imprint","IMPRINT",EDGE,{"derivedFrom":sQuery(id+"F14.wireOp",EDGE,"E51")}),1.0]])]});
            var Q5;
            Q5=makeQuery(id+"F14.imprint","IMPRINT",FACE,{"disambiguationData":[TD([[makeQuery(id+"F14.imprint","IMPRINT",EDGE,{"derivedFrom":sQuery(id+"F14.wireOp",EDGE,"E60")}),1.0]])]});
            var Q6;
            Q6=makeQuery(id+"F14.imprint","IMPRINT",FACE,{"disambiguationData":[TD([[makeQuery(id+"F14.imprint","IMPRINT",EDGE,{"derivedFrom":sQuery(id+"F14.wireOp",EDGE,"E59")}),1.0]])]});
            var Q7;
            Q7=makeQuery(id+"F14.imprint","IMPRINT",FACE,{"disambiguationData":[TD([[makeQuery(id+"F14.imprint","IMPRINT",EDGE,{"derivedFrom":sQuery(id+"F14.wireOp",EDGE,"E58")}),1.0]])]});
            var Q8;
            Q8=makeQuery(id+"F14.imprint","IMPRINT",FACE,{"disambiguationData":[TD([[makeQuery(id+"F14.imprint","IMPRINT",EDGE,{"derivedFrom":sQuery(id+"F14.wireOp",EDGE,"E57")}),1.0]])]});
            var Q9;
            Q9=makeQuery(id+"F14.imprint","IMPRINT",FACE,{"disambiguationData":[TD([[makeQuery(id+"F14.imprint","IMPRINT",EDGE,{"derivedFrom":sQuery(id+"F14.wireOp",EDGE,"E56")}),1.0]])]});
            var Q10;
            Q10=makeQuery(id+"F14.imprint","IMPRINT",FACE,{"disambiguationData":[TD([[makeQuery(id+"F14.imprint","IMPRINT",EDGE,{"derivedFrom":sQuery(id+"F14.wireOp",EDGE,"E62")}),1.0]])]});
            var Q11;
            Q11=makeQuery(id+"F14.imprint","IMPRINT",FACE,{"disambiguationData":[TD([[makeQuery(id+"F14.imprint","IMPRINT",EDGE,{"derivedFrom":sQuery(id+"F14.wireOp",EDGE,"E61")}),1.0]])]});
            var Q12;
            Q12=makeQuery(id+"F14.imprint","IMPRINT",FACE,{"disambiguationData":[TD([[makeQuery(id+"F14.imprint","IMPRINT",EDGE,{"derivedFrom":sQuery(id+"F14.wireOp",EDGE,"E63")}),1.0]])]});
            var Q13;
            Q13=makeQuery(id+"F14.imprint","IMPRINT",FACE,{"disambiguationData":[TD([[makeQuery(id+"F14.imprint","IMPRINT",EDGE,{"derivedFrom":sQuery(id+"F14.wireOp",EDGE,"E64")}),1.0]])]});
            var Q14;
            Q14=makeQuery(id+"F14.imprint","IMPRINT",FACE,{"disambiguationData":[TD([[makeQuery(id+"F14.imprint","IMPRINT",EDGE,{"derivedFrom":sQuery(id+"F14.wireOp",EDGE,"E65")}),1.0]])]});
            var Q15;
            Q15=makeQuery(id+"F14.imprint","IMPRINT",FACE,{"disambiguationData":[TD([[makeQuery(id+"F14.imprint","IMPRINT",EDGE,{"derivedFrom":sQuery(id+"F14.wireOp",EDGE,"E66")}),1.0]])]});
            var Q16;
            Q16=makeQuery(id+"F14.imprint","IMPRINT",FACE,{"disambiguationData":[TD([[makeQuery(id+"F14.imprint","IMPRINT",EDGE,{"derivedFrom":sQuery(id+"F14.wireOp",EDGE,"E69")}),1.0]])]});
            extrude(context, id + "F15", {"entities" : qUnion([Q0, Q1, Q2, Q3, Q4, Q5, Q6, Q7, Q8, Q9, Q10, Q11, Q12, Q13, Q14, Q15, Q16]), "operationType" : NewBodyOperationType.REMOVE, "oppositeDirection" : true, "depth" : 50.8 * mm, "offsetDistance" : 25.4 * mm});
        }
        {
            var Q0;
            {var subQ0=sQuery(id+"F2.wireOp",EDGE,"E2.right");Q0=makeQuery(id+"F5.boolean.opBoolean","MERGE",FACE,{"derivedFrom":[makeQuery(id+"F4.opExtrude","SWEPT_FACE",FACE,{"disambiguationData":[OSD([subQ0])]}),makeQuery(id+"F5.opExtrude","SWEPT_FACE",FACE,{"disambiguationData":[OSD([subQ0])]})]});}
            var sketch = newSketch(context, id + "F16", { "sketchPlane" : qUnion([Q0])});
            skLineSegment(sketch, "E71.bottom", {"start": v(127, 558.8) * mm, "end": v(50.8, 558.8) * mm});
            skLineSegment(sketch, "E71.top", {"start": v(127, 533.4) * mm, "end": v(50.8, 533.4) * mm});
            skLineSegment(sketch, "E71.left", {"start": v(127, 558.8) * mm, "end": v(127, 533.4) * mm});
            skLineSegment(sketch, "E71.right", {"start": v(50.8, 558.8) * mm, "end": v(50.8, 533.4) * mm});
            skLineSegment(sketch, "E72.top", {"start": v(127, 508) * mm, "end": v(50.8, 508) * mm});
            skLineSegment(sketch, "E72.left", {"start": v(127, 533.4) * mm, "end": v(127, 508) * mm});
            skLineSegment(sketch, "E72.right", {"start": v(50.8, 533.4) * mm, "end": v(50.8, 508) * mm});
            skLineSegment(sketch, "E73.top", {"start": v(127, 482.6) * mm, "end": v(50.8, 482.6) * mm});
            skLineSegment(sketch, "E73.left", {"start": v(127, 508) * mm, "end": v(127, 482.6) * mm});
            skLineSegment(sketch, "E73.right", {"start": v(50.8, 508) * mm, "end": v(50.8, 482.6) * mm});
            skLineSegment(sketch, "E74.top", {"start": v(127, 457.2) * mm, "end": v(50.8, 457.2) * mm});
            skLineSegment(sketch, "E74.left", {"start": v(127, 482.6) * mm, "end": v(127, 457.2) * mm});
            skLineSegment(sketch, "E74.right", {"start": v(50.8, 482.6) * mm, "end": v(50.8, 457.2) * mm});
            skLineSegment(sketch, "E75.top", {"start": v(127, 431.8) * mm, "end": v(50.8, 431.8) * mm});
            skLineSegment(sketch, "E75.left", {"start": v(127, 457.2) * mm, "end": v(127, 431.8) * mm});
            skLineSegment(sketch, "E75.right", {"start": v(50.8, 457.2) * mm, "end": v(50.8, 431.8) * mm});
            skLineSegment(sketch, "E76.top", {"start": v(127, 406.4) * mm, "end": v(50.8, 406.4) * mm});
            skLineSegment(sketch, "E76.left", {"start": v(127, 431.8) * mm, "end": v(127, 406.4) * mm});
            skLineSegment(sketch, "E76.right", {"start": v(50.8, 431.8) * mm, "end": v(50.8, 406.4) * mm});
            skLineSegment(sketch, "E77.top", {"start": v(127, 381) * mm, "end": v(50.8, 381) * mm});
            skLineSegment(sketch, "E77.left", {"start": v(127, 406.4) * mm, "end": v(127, 381) * mm});
            skLineSegment(sketch, "E77.right", {"start": v(50.8, 406.4) * mm, "end": v(50.8, 381) * mm});
            skLineSegment(sketch, "E78.top", {"start": v(127, 355.6) * mm, "end": v(50.8, 355.6) * mm});
            skLineSegment(sketch, "E78.left", {"start": v(127, 381) * mm, "end": v(127, 355.6) * mm});
            skLineSegment(sketch, "E78.right", {"start": v(50.8, 381) * mm, "end": v(50.8, 355.6) * mm});
            skLineSegment(sketch, "E79.top", {"start": v(127, 330.2) * mm, "end": v(50.8, 330.2) * mm});
            skLineSegment(sketch, "E79.left", {"start": v(127, 355.6) * mm, "end": v(127, 330.2) * mm});
            skLineSegment(sketch, "E79.right", {"start": v(50.8, 355.6) * mm, "end": v(50.8, 330.2) * mm});
            skLineSegment(sketch, "E80.top", {"start": v(127, 304.8) * mm, "end": v(50.8, 304.8) * mm});
            skLineSegment(sketch, "E80.left", {"start": v(127, 330.2) * mm, "end": v(127, 304.8) * mm});
            skLineSegment(sketch, "E80.right", {"start": v(50.8, 330.2) * mm, "end": v(50.8, 304.8) * mm});
            skLineSegment(sketch, "E81.top", {"start": v(127, 279.4) * mm, "end": v(50.8, 279.4) * mm});
            skLineSegment(sketch, "E81.left", {"start": v(127, 304.8) * mm, "end": v(127, 279.4) * mm});
            skLineSegment(sketch, "E81.right", {"start": v(50.8, 304.8) * mm, "end": v(50.8, 279.4) * mm});
            skLineSegment(sketch, "E82.top", {"start": v(127, 254) * mm, "end": v(50.8, 254) * mm});
            skLineSegment(sketch, "E82.left", {"start": v(127, 279.4) * mm, "end": v(127, 254) * mm});
            skLineSegment(sketch, "E82.right", {"start": v(50.8, 279.4) * mm, "end": v(50.8, 254) * mm});
            skLineSegment(sketch, "E83.top", {"start": v(127, 228.6) * mm, "end": v(50.8, 228.6) * mm});
            skLineSegment(sketch, "E83.left", {"start": v(127, 254) * mm, "end": v(127, 228.6) * mm});
            skLineSegment(sketch, "E83.right", {"start": v(50.8, 254) * mm, "end": v(50.8, 228.6) * mm});
            skLineSegment(sketch, "E84.top", {"start": v(127, 203.2) * mm, "end": v(50.8, 203.2) * mm});
            skLineSegment(sketch, "E84.left", {"start": v(127, 228.6) * mm, "end": v(127, 203.2) * mm});
            skLineSegment(sketch, "E84.right", {"start": v(50.8, 228.6) * mm, "end": v(50.8, 203.2) * mm});
            skLineSegment(sketch, "E85.top", {"start": v(127, 177.8) * mm, "end": v(50.8, 177.8) * mm});
            skLineSegment(sketch, "E85.left", {"start": v(127, 203.2) * mm, "end": v(127, 177.8) * mm});
            skLineSegment(sketch, "E85.right", {"start": v(50.8, 203.2) * mm, "end": v(50.8, 177.8) * mm});
            skLineSegment(sketch, "E86.top", {"start": v(127, 152.4) * mm, "end": v(50.8, 152.4) * mm});
            skLineSegment(sketch, "E86.left", {"start": v(127, 177.8) * mm, "end": v(127, 152.4) * mm});
            skLineSegment(sketch, "E86.right", {"start": v(50.8, 177.8) * mm, "end": v(50.8, 152.4) * mm});
            skLineSegment(sketch, "E87.top", {"start": v(127, 127) * mm, "end": v(50.8, 127) * mm});
            skLineSegment(sketch, "E87.left", {"start": v(127, 152.4) * mm, "end": v(127, 127) * mm});
            skLineSegment(sketch, "E87.right", {"start": v(50.8, 152.4) * mm, "end": v(50.8, 127) * mm});
            skLineSegment(sketch, "E88.top", {"start": v(127, 101.6) * mm, "end": v(50.8, 101.6) * mm});
            skLineSegment(sketch, "E88.left", {"start": v(127, 127) * mm, "end": v(127, 101.6) * mm});
            skLineSegment(sketch, "E88.right", {"start": v(50.8, 127) * mm, "end": v(50.8, 101.6) * mm});
            skLineSegment(sketch, "E89.bottom", {"start": v(127, 76.2) * mm, "end": v(50.8, 76.2) * mm});
            skLineSegment(sketch, "E89.left", {"start": v(127, 76.2) * mm, "end": v(127, 101.6) * mm});
            skLineSegment(sketch, "E89.right", {"start": v(50.8, 76.2) * mm, "end": v(50.8, 101.6) * mm});
            skCircle(sketch, "E90", {"center": v(88.9, 88.9) * mm, "radius": 3.81 * mm});
            skCircle(sketch, "E91", {"center": v(88.9, 114.3) * mm, "radius": 3.81 * mm});
            skCircle(sketch, "E92", {"center": v(88.9, 139.7) * mm, "radius": 3.81 * mm});
            skCircle(sketch, "E93", {"center": v(88.9, 165.1) * mm, "radius": 3.81 * mm});
            skCircle(sketch, "E94", {"center": v(88.9, 190.5) * mm, "radius": 3.81 * mm});
            skCircle(sketch, "E95", {"center": v(88.9, 215.9) * mm, "radius": 3.81 * mm});
            skCircle(sketch, "E96", {"center": v(88.9, 241.3) * mm, "radius": 3.81 * mm});
            skCircle(sketch, "E97", {"center": v(88.9, 266.7) * mm, "radius": 3.81 * mm});
            skCircle(sketch, "E98", {"center": v(88.9, 292.1) * mm, "radius": 3.81 * mm});
            skCircle(sketch, "E99", {"center": v(88.9, 317.5) * mm, "radius": 3.81 * mm});
            skCircle(sketch, "E100", {"center": v(88.9, 342.9) * mm, "radius": 3.81 * mm});
            skCircle(sketch, "E101", {"center": v(88.9, 368.3) * mm, "radius": 3.8 * mm});
            skCircle(sketch, "E102", {"center": v(88.9, 393.7) * mm, "radius": 3.81 * mm});
            skCircle(sketch, "E103", {"center": v(88.9, 419.1) * mm, "radius": 3.81 * mm});
            skCircle(sketch, "E104", {"center": v(88.9, 444.5) * mm, "radius": 3.81 * mm});
            skCircle(sketch, "E105", {"center": v(88.9, 469.9) * mm, "radius": 3.81 * mm});
            skCircle(sketch, "E106", {"center": v(88.9, 495.3) * mm, "radius": 3.81 * mm});
            skCircle(sketch, "E107", {"center": v(88.9, 520.7) * mm, "radius": 3.81 * mm});
            skCircle(sketch, "E108", {"center": v(88.9, 546.1) * mm, "radius": 3.81 * mm});
            skSolve(sketch);
        }
        {
            var Q0;
            Q0=makeQuery(id+"F6.imprint","IMPRINT",FACE,{"disambiguationData":[TD([[makeQuery(id+"F6.imprint","IMPRINT",EDGE,{"derivedFrom":sQuery(id+"F6.wireOp",EDGE,"E23")}),1.0]])]});
            var Q1;
            Q1=makeQuery(id+"F6.imprint","IMPRINT",FACE,{"disambiguationData":[TD([[makeQuery(id+"F6.imprint","IMPRINT",EDGE,{"derivedFrom":sQuery(id+"F6.wireOp",EDGE,"E24")}),1.0]])]});
            extrude(context, id + "F17", {"entities" : qUnion([Q0, Q1]), "operationType" : NewBodyOperationType.ADD, "depth" : -38.1 * mm, "offsetDistance" : 25.4 * mm});
        }
        {
            var Q0;
            Q0=makeQuery(id+"F16.imprint","IMPRINT",FACE,{"disambiguationData":[TD([[makeQuery(id+"F16.imprint","IMPRINT",EDGE,{"derivedFrom":sQuery(id+"F16.wireOp",EDGE,"E108")}),1.0]])]});
            var Q1;
            Q1=makeQuery(id+"F16.imprint","IMPRINT",FACE,{"disambiguationData":[TD([[makeQuery(id+"F16.imprint","IMPRINT",EDGE,{"derivedFrom":sQuery(id+"F16.wireOp",EDGE,"E107")}),1.0]])]});
            var Q2;
            Q2=makeQuery(id+"F16.imprint","IMPRINT",FACE,{"disambiguationData":[TD([[makeQuery(id+"F16.imprint","IMPRINT",EDGE,{"derivedFrom":sQuery(id+"F16.wireOp",EDGE,"E106")}),1.0]])]});
            var Q3;
            Q3=makeQuery(id+"F16.imprint","IMPRINT",FACE,{"disambiguationData":[TD([[makeQuery(id+"F16.imprint","IMPRINT",EDGE,{"derivedFrom":sQuery(id+"F16.wireOp",EDGE,"E105")}),1.0]])]});
            var Q4;
            Q4=makeQuery(id+"F16.imprint","IMPRINT",FACE,{"disambiguationData":[TD([[makeQuery(id+"F16.imprint","IMPRINT",EDGE,{"derivedFrom":sQuery(id+"F16.wireOp",EDGE,"E104")}),1.0]])]});
            var Q5;
            Q5=makeQuery(id+"F16.imprint","IMPRINT",FACE,{"disambiguationData":[TD([[makeQuery(id+"F16.imprint","IMPRINT",EDGE,{"derivedFrom":sQuery(id+"F16.wireOp",EDGE,"E103")}),1.0]])]});
            var Q6;
            Q6=makeQuery(id+"F16.imprint","IMPRINT",FACE,{"disambiguationData":[TD([[makeQuery(id+"F16.imprint","IMPRINT",EDGE,{"derivedFrom":sQuery(id+"F16.wireOp",EDGE,"E102")}),1.0]])]});
            var Q7;
            Q7=makeQuery(id+"F16.imprint","IMPRINT",FACE,{"disambiguationData":[TD([[makeQuery(id+"F16.imprint","IMPRINT",EDGE,{"derivedFrom":sQuery(id+"F16.wireOp",EDGE,"E101")}),1.0]])]});
            var Q8;
            Q8=makeQuery(id+"F16.imprint","IMPRINT",FACE,{"disambiguationData":[TD([[makeQuery(id+"F16.imprint","IMPRINT",EDGE,{"derivedFrom":sQuery(id+"F16.wireOp",EDGE,"E100")}),1.0]])]});
            var Q9;
            Q9=makeQuery(id+"F16.imprint","IMPRINT",FACE,{"disambiguationData":[TD([[makeQuery(id+"F16.imprint","IMPRINT",EDGE,{"derivedFrom":sQuery(id+"F16.wireOp",EDGE,"E99")}),1.0]])]});
            var Q10;
            Q10=makeQuery(id+"F16.imprint","IMPRINT",FACE,{"disambiguationData":[TD([[makeQuery(id+"F16.imprint","IMPRINT",EDGE,{"derivedFrom":sQuery(id+"F16.wireOp",EDGE,"E98")}),1.0]])]});
            var Q11;
            Q11=makeQuery(id+"F16.imprint","IMPRINT",FACE,{"disambiguationData":[TD([[makeQuery(id+"F16.imprint","IMPRINT",EDGE,{"derivedFrom":sQuery(id+"F16.wireOp",EDGE,"E97")}),1.0]])]});
            var Q12;
            Q12=makeQuery(id+"F16.imprint","IMPRINT",FACE,{"disambiguationData":[TD([[makeQuery(id+"F16.imprint","IMPRINT",EDGE,{"derivedFrom":sQuery(id+"F16.wireOp",EDGE,"E96")}),1.0]])]});
            var Q13;
            Q13=makeQuery(id+"F16.imprint","IMPRINT",FACE,{"disambiguationData":[TD([[makeQuery(id+"F16.imprint","IMPRINT",EDGE,{"derivedFrom":sQuery(id+"F16.wireOp",EDGE,"E95")}),1.0]])]});
            var Q14;
            Q14=makeQuery(id+"F16.imprint","IMPRINT",FACE,{"disambiguationData":[TD([[makeQuery(id+"F16.imprint","IMPRINT",EDGE,{"derivedFrom":sQuery(id+"F16.wireOp",EDGE,"E94")}),1.0]])]});
            var Q15;
            Q15=makeQuery(id+"F16.imprint","IMPRINT",FACE,{"disambiguationData":[TD([[makeQuery(id+"F16.imprint","IMPRINT",EDGE,{"derivedFrom":sQuery(id+"F16.wireOp",EDGE,"E93")}),1.0]])]});
            var Q16;
            Q16=makeQuery(id+"F16.imprint","IMPRINT",FACE,{"disambiguationData":[TD([[makeQuery(id+"F16.imprint","IMPRINT",EDGE,{"derivedFrom":sQuery(id+"F16.wireOp",EDGE,"E92")}),1.0]])]});
            var Q17;
            Q17=makeQuery(id+"F16.imprint","IMPRINT",FACE,{"disambiguationData":[TD([[makeQuery(id+"F16.imprint","IMPRINT",EDGE,{"derivedFrom":sQuery(id+"F16.wireOp",EDGE,"E91")}),1.0]])]});
            var Q18;
            Q18=makeQuery(id+"F16.imprint","IMPRINT",FACE,{"disambiguationData":[TD([[makeQuery(id+"F16.imprint","IMPRINT",EDGE,{"derivedFrom":sQuery(id+"F16.wireOp",EDGE,"E90")}),1.0]])]});
            extrude(context, id + "F18", {"entities" : qUnion([Q0, Q1, Q2, Q3, Q4, Q5, Q6, Q7, Q8, Q9, Q10, Q11, Q12, Q13, Q14, Q15, Q16, Q17, Q18]), "operationType" : NewBodyOperationType.REMOVE, "oppositeDirection" : true, "depth" : 38.1 * mm, "offsetDistance" : 25.4 * mm});
        }
        {
            var Q0;
            Q0=makeQuery(id+"F13.opExtrude","SWEPT_FACE",FACE,{"disambiguationData":[OSD([sQuery(id+"F11.wireOp",EDGE,"E29.left"),sQuery(id+"F11.wireOp",EDGE,"E30.left")])]});
            var sketch = newSketch(context, id + "F19", { "sketchPlane" : qUnion([Q0])});
            skLineSegment(sketch, "E109.bottom", {"start": v(-120.65, 558.8) * mm, "end": v(-57.15, 558.8) * mm});
            skLineSegment(sketch, "E109.top", {"start": v(-120.65, 584.2) * mm, "end": v(-57.15, 584.2) * mm});
            skLineSegment(sketch, "E109.left", {"start": v(-120.65, 558.8) * mm, "end": v(-120.65, 584.2) * mm});
            skLineSegment(sketch, "E109.right", {"start": v(-57.15, 558.8) * mm, "end": v(-57.15, 584.2) * mm});
            skLineSegment(sketch, "E110.top", {"start": v(-120.65, 609.6) * mm, "end": v(-57.15, 609.6) * mm});
            skLineSegment(sketch, "E110.left", {"start": v(-120.65, 584.2) * mm, "end": v(-120.65, 609.6) * mm});
            skLineSegment(sketch, "E110.right", {"start": v(-57.15, 584.2) * mm, "end": v(-57.15, 609.6) * mm});
            skLineSegment(sketch, "E111.top", {"start": v(-120.65, 635) * mm, "end": v(-57.15, 635) * mm});
            skLineSegment(sketch, "E111.left", {"start": v(-120.65, 609.6) * mm, "end": v(-120.65, 635) * mm});
            skLineSegment(sketch, "E111.right", {"start": v(-57.15, 609.6) * mm, "end": v(-57.15, 635) * mm});
            skLineSegment(sketch, "E112.top", {"start": v(-120.65, 660.4) * mm, "end": v(-57.15, 660.4) * mm});
            skLineSegment(sketch, "E112.left", {"start": v(-120.65, 635) * mm, "end": v(-120.65, 660.4) * mm});
            skLineSegment(sketch, "E112.right", {"start": v(-57.15, 635) * mm, "end": v(-57.15, 660.4) * mm});
            skLineSegment(sketch, "E113.top", {"start": v(-120.65, 685.8) * mm, "end": v(-57.15, 685.8) * mm});
            skLineSegment(sketch, "E113.left", {"start": v(-120.65, 660.4) * mm, "end": v(-120.65, 685.8) * mm});
            skLineSegment(sketch, "E113.right", {"start": v(-57.15, 660.4) * mm, "end": v(-57.15, 685.8) * mm});
            skLineSegment(sketch, "E114.top", {"start": v(-120.65, 711.2) * mm, "end": v(-57.15, 711.2) * mm});
            skLineSegment(sketch, "E114.left", {"start": v(-120.65, 685.8) * mm, "end": v(-120.65, 711.2) * mm});
            skLineSegment(sketch, "E114.right", {"start": v(-57.15, 685.8) * mm, "end": v(-57.15, 711.2) * mm});
            skLineSegment(sketch, "E115.top", {"start": v(-120.65, 736.6) * mm, "end": v(-57.15, 736.6) * mm});
            skLineSegment(sketch, "E115.left", {"start": v(-120.65, 711.2) * mm, "end": v(-120.65, 736.6) * mm});
            skLineSegment(sketch, "E115.right", {"start": v(-57.15, 711.2) * mm, "end": v(-57.15, 736.6) * mm});
            skLineSegment(sketch, "E116.top", {"start": v(-120.65, 762) * mm, "end": v(-57.15, 762) * mm});
            skLineSegment(sketch, "E116.left", {"start": v(-120.65, 736.6) * mm, "end": v(-120.65, 762) * mm});
            skLineSegment(sketch, "E116.right", {"start": v(-57.15, 736.6) * mm, "end": v(-57.15, 762) * mm});
            skLineSegment(sketch, "E117.top", {"start": v(-120.65, 787.4) * mm, "end": v(-57.15, 787.4) * mm});
            skLineSegment(sketch, "E117.left", {"start": v(-120.65, 762) * mm, "end": v(-120.65, 787.4) * mm});
            skLineSegment(sketch, "E117.right", {"start": v(-57.15, 762) * mm, "end": v(-57.15, 787.4) * mm});
            skLineSegment(sketch, "E118.top", {"start": v(-120.65, 812.8) * mm, "end": v(-57.15, 812.8) * mm});
            skLineSegment(sketch, "E118.left", {"start": v(-120.65, 787.4) * mm, "end": v(-120.65, 812.8) * mm});
            skLineSegment(sketch, "E118.right", {"start": v(-57.15, 787.4) * mm, "end": v(-57.15, 812.8) * mm});
            skLineSegment(sketch, "E119.top", {"start": v(-120.65, 838.2) * mm, "end": v(-57.15, 838.2) * mm});
            skLineSegment(sketch, "E119.left", {"start": v(-120.65, 812.8) * mm, "end": v(-120.65, 838.2) * mm});
            skLineSegment(sketch, "E119.right", {"start": v(-57.15, 812.8) * mm, "end": v(-57.15, 838.2) * mm});
            skLineSegment(sketch, "E120.top", {"start": v(-120.65, 863.6) * mm, "end": v(-57.15, 863.6) * mm});
            skLineSegment(sketch, "E120.left", {"start": v(-120.65, 838.2) * mm, "end": v(-120.65, 863.6) * mm});
            skLineSegment(sketch, "E120.right", {"start": v(-57.15, 838.2) * mm, "end": v(-57.15, 863.6) * mm});
            skLineSegment(sketch, "E121.top", {"start": v(-120.65, 889) * mm, "end": v(-57.15, 889) * mm});
            skLineSegment(sketch, "E121.left", {"start": v(-120.65, 863.6) * mm, "end": v(-120.65, 889) * mm});
            skLineSegment(sketch, "E121.right", {"start": v(-57.15, 863.6) * mm, "end": v(-57.15, 889) * mm});
            skLineSegment(sketch, "E122.top", {"start": v(-120.65, 914.4) * mm, "end": v(-57.15, 914.4) * mm});
            skLineSegment(sketch, "E122.left", {"start": v(-120.65, 889) * mm, "end": v(-120.65, 914.4) * mm});
            skLineSegment(sketch, "E122.right", {"start": v(-57.15, 889) * mm, "end": v(-57.15, 914.4) * mm});
            skLineSegment(sketch, "E123.top", {"start": v(-120.65, 939.8) * mm, "end": v(-57.15, 939.8) * mm});
            skLineSegment(sketch, "E123.left", {"start": v(-120.65, 914.4) * mm, "end": v(-120.65, 939.8) * mm});
            skLineSegment(sketch, "E123.right", {"start": v(-57.15, 914.4) * mm, "end": v(-57.15, 939.8) * mm});
            skLineSegment(sketch, "E124.top", {"start": v(-120.65, 965.2) * mm, "end": v(-57.15, 965.2) * mm});
            skLineSegment(sketch, "E124.left", {"start": v(-120.65, 939.8) * mm, "end": v(-120.65, 965.2) * mm});
            skLineSegment(sketch, "E124.right", {"start": v(-57.15, 939.8) * mm, "end": v(-57.15, 965.2) * mm});
            skLineSegment(sketch, "E125.top", {"start": v(-120.65, 990.6) * mm, "end": v(-57.15, 990.6) * mm});
            skLineSegment(sketch, "E125.left", {"start": v(-120.65, 965.2) * mm, "end": v(-120.65, 990.6) * mm});
            skLineSegment(sketch, "E125.right", {"start": v(-57.15, 965.2) * mm, "end": v(-57.15, 990.6) * mm});
            skCircle(sketch, "E126", {"center": v(-88.9, 1003.3) * mm, "radius": 3.81 * mm});
            skCircle(sketch, "E127", {"center": v(-88.9, 977.9) * mm, "radius": 3.81 * mm});
            skCircle(sketch, "E128", {"center": v(-88.9, 952.5) * mm, "radius": 3.81 * mm});
            skCircle(sketch, "E129", {"center": v(-88.9, 927.1) * mm, "radius": 3.81 * mm});
            skCircle(sketch, "E130", {"center": v(-88.9, 901.7) * mm, "radius": 3.81 * mm});
            skCircle(sketch, "E131", {"center": v(-88.9, 876.3) * mm, "radius": 3.81 * mm});
            skCircle(sketch, "E132", {"center": v(-88.9, 850.9) * mm, "radius": 3.81 * mm});
            skCircle(sketch, "E133", {"center": v(-88.9, 825.5) * mm, "radius": 3.81 * mm});
            skCircle(sketch, "E134", {"center": v(-88.9, 800.1) * mm, "radius": 3.81 * mm});
            skCircle(sketch, "E135", {"center": v(-88.9, 774.7) * mm, "radius": 3.81 * mm});
            skCircle(sketch, "E136", {"center": v(-88.9, 749.3) * mm, "radius": 3.81 * mm});
            skCircle(sketch, "E137", {"center": v(-88.9, 723.9) * mm, "radius": 3.81 * mm});
            skCircle(sketch, "E138", {"center": v(-88.9, 698.5) * mm, "radius": 3.81 * mm});
            skCircle(sketch, "E139", {"center": v(-88.9, 673.1) * mm, "radius": 3.81 * mm});
            skCircle(sketch, "E140", {"center": v(-88.9, 647.7) * mm, "radius": 3.81 * mm});
            skCircle(sketch, "E141", {"center": v(-88.9, 622.3) * mm, "radius": 3.81 * mm});
            skCircle(sketch, "E142", {"center": v(-88.9, 596.9) * mm, "radius": 3.81 * mm});
            skCircle(sketch, "E143", {"center": v(-88.9, 571.5) * mm, "radius": 3.81 * mm});
            skSolve(sketch);
        }
        {
            var Q0;
            Q0=makeQuery(id+"F19.imprint","IMPRINT",FACE,{"disambiguationData":[TD([[makeQuery(id+"F19.imprint","IMPRINT",EDGE,{"derivedFrom":sQuery(id+"F19.wireOp",EDGE,"E143")}),1.0]])]});
            var Q1;
            Q1=makeQuery(id+"F19.imprint","IMPRINT",FACE,{"disambiguationData":[TD([[makeQuery(id+"F19.imprint","IMPRINT",EDGE,{"derivedFrom":sQuery(id+"F19.wireOp",EDGE,"E142")}),1.0]])]});
            var Q2;
            Q2=makeQuery(id+"F19.imprint","IMPRINT",FACE,{"disambiguationData":[TD([[makeQuery(id+"F19.imprint","IMPRINT",EDGE,{"derivedFrom":sQuery(id+"F19.wireOp",EDGE,"E141")}),1.0]])]});
            var Q3;
            Q3=makeQuery(id+"F19.imprint","IMPRINT",FACE,{"disambiguationData":[TD([[makeQuery(id+"F19.imprint","IMPRINT",EDGE,{"derivedFrom":sQuery(id+"F19.wireOp",EDGE,"E140")}),1.0]])]});
            var Q4;
            Q4=makeQuery(id+"F19.imprint","IMPRINT",FACE,{"disambiguationData":[TD([[makeQuery(id+"F19.imprint","IMPRINT",EDGE,{"derivedFrom":sQuery(id+"F19.wireOp",EDGE,"E139")}),1.0]])]});
            var Q5;
            Q5=makeQuery(id+"F19.imprint","IMPRINT",FACE,{"disambiguationData":[TD([[makeQuery(id+"F19.imprint","IMPRINT",EDGE,{"derivedFrom":sQuery(id+"F19.wireOp",EDGE,"E138")}),1.0]])]});
            var Q6;
            Q6=makeQuery(id+"F19.imprint","IMPRINT",FACE,{"disambiguationData":[TD([[makeQuery(id+"F19.imprint","IMPRINT",EDGE,{"derivedFrom":sQuery(id+"F19.wireOp",EDGE,"E137")}),1.0]])]});
            var Q7;
            Q7=makeQuery(id+"F19.imprint","IMPRINT",FACE,{"disambiguationData":[TD([[makeQuery(id+"F19.imprint","IMPRINT",EDGE,{"derivedFrom":sQuery(id+"F19.wireOp",EDGE,"E136")}),1.0]])]});
            var Q8;
            Q8=makeQuery(id+"F19.imprint","IMPRINT",FACE,{"disambiguationData":[TD([[makeQuery(id+"F19.imprint","IMPRINT",EDGE,{"derivedFrom":sQuery(id+"F19.wireOp",EDGE,"E135")}),1.0]])]});
            var Q9;
            Q9=makeQuery(id+"F19.imprint","IMPRINT",FACE,{"disambiguationData":[TD([[makeQuery(id+"F19.imprint","IMPRINT",EDGE,{"derivedFrom":sQuery(id+"F19.wireOp",EDGE,"E134")}),1.0]])]});
            var Q10;
            Q10=makeQuery(id+"F19.imprint","IMPRINT",FACE,{"disambiguationData":[TD([[makeQuery(id+"F19.imprint","IMPRINT",EDGE,{"derivedFrom":sQuery(id+"F19.wireOp",EDGE,"E133")}),1.0]])]});
            var Q11;
            Q11=makeQuery(id+"F19.imprint","IMPRINT",FACE,{"disambiguationData":[TD([[makeQuery(id+"F19.imprint","IMPRINT",EDGE,{"derivedFrom":sQuery(id+"F19.wireOp",EDGE,"E132")}),1.0]])]});
            var Q12;
            Q12=makeQuery(id+"F19.imprint","IMPRINT",FACE,{"disambiguationData":[TD([[makeQuery(id+"F19.imprint","IMPRINT",EDGE,{"derivedFrom":sQuery(id+"F19.wireOp",EDGE,"E131")}),1.0]])]});
            var Q13;
            Q13=makeQuery(id+"F19.imprint","IMPRINT",FACE,{"disambiguationData":[TD([[makeQuery(id+"F19.imprint","IMPRINT",EDGE,{"derivedFrom":sQuery(id+"F19.wireOp",EDGE,"E130")}),1.0]])]});
            var Q14;
            Q14=makeQuery(id+"F19.imprint","IMPRINT",FACE,{"disambiguationData":[TD([[makeQuery(id+"F19.imprint","IMPRINT",EDGE,{"derivedFrom":sQuery(id+"F19.wireOp",EDGE,"E129")}),1.0]])]});
            var Q15;
            Q15=makeQuery(id+"F19.imprint","IMPRINT",FACE,{"disambiguationData":[TD([[makeQuery(id+"F19.imprint","IMPRINT",EDGE,{"derivedFrom":sQuery(id+"F19.wireOp",EDGE,"E128")}),1.0]])]});
            var Q16;
            Q16=makeQuery(id+"F19.imprint","IMPRINT",FACE,{"disambiguationData":[TD([[makeQuery(id+"F19.imprint","IMPRINT",EDGE,{"derivedFrom":sQuery(id+"F19.wireOp",EDGE,"E127")}),1.0]])]});
            var Q17;
            Q17=makeQuery(id+"F19.imprint","IMPRINT",FACE,{"disambiguationData":[TD([[makeQuery(id+"F19.imprint","IMPRINT",EDGE,{"derivedFrom":sQuery(id+"F19.wireOp",EDGE,"E126")}),1.0]])]});
            extrude(context, id + "F20", {"entities" : qUnion([Q0, Q1, Q2, Q3, Q4, Q5, Q6, Q7, Q8, Q9, Q10, Q11, Q12, Q13, Q14, Q15, Q16, Q17]), "operationType" : NewBodyOperationType.REMOVE, "oppositeDirection" : true, "depth" : 25.4 * mm, "offsetDistance" : 25.4 * mm});
        }
        {
            var Q0;
            Q0=makeQuery(id+"F14.imprint","IMPRINT",FACE,{"disambiguationData":[TD([[makeQuery(id+"F14.imprint","IMPRINT",EDGE,{"derivedFrom":sQuery(id+"F14.wireOp",EDGE,"E68")}),1.0]])]});
            var Q1;
            Q1=makeQuery(id+"F14.imprint","IMPRINT",FACE,{"disambiguationData":[TD([[makeQuery(id+"F14.imprint","IMPRINT",EDGE,{"derivedFrom":sQuery(id+"F14.wireOp",EDGE,"E67")}),1.0]])]});
            extrude(context, id + "F21", {"entities" : qUnion([Q0, Q1]), "operationType" : NewBodyOperationType.ADD, "depth" : 6.35 * mm, "offsetDistance" : 25.4 * mm});
        }
        {
            var Q0;
            Q0=makeQuery(id+"F14.imprint","IMPRINT",FACE,{"disambiguationData":[TD([[makeQuery(id+"F14.imprint","IMPRINT",EDGE,{"derivedFrom":sQuery(id+"F14.wireOp",EDGE,"E68")}),1.0]])]});
            var Q1;
            Q1=makeQuery(id+"F14.imprint","IMPRINT",FACE,{"disambiguationData":[TD([[makeQuery(id+"F14.imprint","IMPRINT",EDGE,{"derivedFrom":sQuery(id+"F14.wireOp",EDGE,"E67")}),1.0]])]});
            extrude(context, id + "F22", {"entities" : qUnion([Q0, Q1]), "operationType" : NewBodyOperationType.ADD, "depth" : -25.4 * mm, "offsetDistance" : 25.4 * mm});
        }
        {
            var Q0;
            Q0=makeQuery(id+"F10.opExtrude","SWEPT_FACE",FACE,{"disambiguationData":[OSD([sQuery(id+"F8.wireOp",EDGE,"E25.right")])]});
            var sketch = newSketch(context, id + "F23", { "sketchPlane" : qUnion([Q0])});
            skLineSegment(sketch, "E144.bottom", {"start": v(57.15, 558.8) * mm, "end": v(120.65, 558.8) * mm});
            skLineSegment(sketch, "E144.top", {"start": v(57.15, 584.2) * mm, "end": v(120.65, 584.2) * mm});
            skLineSegment(sketch, "E144.left", {"start": v(57.15, 558.8) * mm, "end": v(57.15, 584.2) * mm});
            skLineSegment(sketch, "E144.right", {"start": v(120.65, 558.8) * mm, "end": v(120.65, 584.2) * mm});
            skLineSegment(sketch, "E145.top", {"start": v(57.15, 609.6) * mm, "end": v(120.65, 609.6) * mm});
            skLineSegment(sketch, "E145.left", {"start": v(57.15, 584.2) * mm, "end": v(57.15, 609.6) * mm});
            skLineSegment(sketch, "E145.right", {"start": v(120.65, 584.2) * mm, "end": v(120.65, 609.6) * mm});
            skLineSegment(sketch, "E146.top", {"start": v(57.15, 635) * mm, "end": v(120.65, 635) * mm});
            skLineSegment(sketch, "E146.left", {"start": v(57.15, 609.6) * mm, "end": v(57.15, 635) * mm});
            skLineSegment(sketch, "E146.right", {"start": v(120.65, 609.6) * mm, "end": v(120.65, 635) * mm});
            skLineSegment(sketch, "E147.top", {"start": v(57.15, 660.4) * mm, "end": v(120.65, 660.4) * mm});
            skLineSegment(sketch, "E147.left", {"start": v(57.15, 635) * mm, "end": v(57.15, 660.4) * mm});
            skLineSegment(sketch, "E147.right", {"start": v(120.65, 635) * mm, "end": v(120.65, 660.4) * mm});
            skLineSegment(sketch, "E148.top", {"start": v(57.15, 685.8) * mm, "end": v(120.65, 685.8) * mm});
            skLineSegment(sketch, "E148.left", {"start": v(57.15, 660.4) * mm, "end": v(57.15, 685.8) * mm});
            skLineSegment(sketch, "E148.right", {"start": v(120.65, 660.4) * mm, "end": v(120.65, 685.8) * mm});
            skLineSegment(sketch, "E149.top", {"start": v(57.15, 711.2) * mm, "end": v(120.65, 711.2) * mm});
            skLineSegment(sketch, "E149.left", {"start": v(57.15, 685.8) * mm, "end": v(57.15, 711.2) * mm});
            skLineSegment(sketch, "E149.right", {"start": v(120.65, 685.8) * mm, "end": v(120.65, 711.2) * mm});
            skLineSegment(sketch, "E150.top", {"start": v(57.15, 736.6) * mm, "end": v(120.65, 736.6) * mm});
            skLineSegment(sketch, "E150.left", {"start": v(57.15, 711.2) * mm, "end": v(57.15, 736.6) * mm});
            skLineSegment(sketch, "E150.right", {"start": v(120.65, 711.2) * mm, "end": v(120.65, 736.6) * mm});
            skLineSegment(sketch, "E151.top", {"start": v(57.15, 762) * mm, "end": v(120.65, 762) * mm});
            skLineSegment(sketch, "E151.left", {"start": v(57.15, 736.6) * mm, "end": v(57.15, 762) * mm});
            skLineSegment(sketch, "E151.right", {"start": v(120.65, 736.6) * mm, "end": v(120.65, 762) * mm});
            skLineSegment(sketch, "E152.top", {"start": v(57.15, 787.4) * mm, "end": v(120.65, 787.4) * mm});
            skLineSegment(sketch, "E152.left", {"start": v(57.15, 762) * mm, "end": v(57.15, 787.4) * mm});
            skLineSegment(sketch, "E152.right", {"start": v(120.65, 762) * mm, "end": v(120.65, 787.4) * mm});
            skLineSegment(sketch, "E153.top", {"start": v(57.15, 812.8) * mm, "end": v(120.65, 812.8) * mm});
            skLineSegment(sketch, "E153.left", {"start": v(57.15, 787.4) * mm, "end": v(57.15, 812.8) * mm});
            skLineSegment(sketch, "E153.right", {"start": v(120.65, 787.4) * mm, "end": v(120.65, 812.8) * mm});
            skLineSegment(sketch, "E154.top", {"start": v(57.15, 838.2) * mm, "end": v(120.65, 838.2) * mm});
            skLineSegment(sketch, "E154.left", {"start": v(57.15, 812.8) * mm, "end": v(57.15, 838.2) * mm});
            skLineSegment(sketch, "E154.right", {"start": v(120.65, 812.8) * mm, "end": v(120.65, 838.2) * mm});
            skLineSegment(sketch, "E155.top", {"start": v(57.15, 863.6) * mm, "end": v(120.65, 863.6) * mm});
            skLineSegment(sketch, "E155.left", {"start": v(57.15, 838.2) * mm, "end": v(57.15, 863.6) * mm});
            skLineSegment(sketch, "E155.right", {"start": v(120.65, 838.2) * mm, "end": v(120.65, 863.6) * mm});
            skLineSegment(sketch, "E156.top", {"start": v(57.15, 889) * mm, "end": v(120.65, 889) * mm});
            skLineSegment(sketch, "E156.left", {"start": v(57.15, 863.6) * mm, "end": v(57.15, 889) * mm});
            skLineSegment(sketch, "E156.right", {"start": v(120.65, 863.6) * mm, "end": v(120.65, 889) * mm});
            skLineSegment(sketch, "E157.top", {"start": v(57.15, 914.4) * mm, "end": v(120.65, 914.4) * mm});
            skLineSegment(sketch, "E157.left", {"start": v(57.15, 889) * mm, "end": v(57.15, 914.4) * mm});
            skLineSegment(sketch, "E157.right", {"start": v(120.65, 889) * mm, "end": v(120.65, 914.4) * mm});
            skLineSegment(sketch, "E158.top", {"start": v(57.15, 939.8) * mm, "end": v(120.65, 939.8) * mm});
            skLineSegment(sketch, "E158.left", {"start": v(57.15, 914.4) * mm, "end": v(57.15, 939.8) * mm});
            skLineSegment(sketch, "E158.right", {"start": v(120.65, 914.4) * mm, "end": v(120.65, 939.8) * mm});
            skLineSegment(sketch, "E159.top", {"start": v(57.15, 965.2) * mm, "end": v(120.65, 965.2) * mm});
            skLineSegment(sketch, "E159.left", {"start": v(57.15, 939.8) * mm, "end": v(57.15, 965.2) * mm});
            skLineSegment(sketch, "E159.right", {"start": v(120.65, 939.8) * mm, "end": v(120.65, 965.2) * mm});
            skLineSegment(sketch, "E160.top", {"start": v(57.15, 990.6) * mm, "end": v(120.65, 990.6) * mm});
            skLineSegment(sketch, "E160.left", {"start": v(57.15, 965.2) * mm, "end": v(57.15, 990.6) * mm});
            skLineSegment(sketch, "E160.right", {"start": v(120.65, 965.2) * mm, "end": v(120.65, 990.6) * mm});
            skCircle(sketch, "E161", {"center": v(88.9, 800.1) * mm, "radius": 3.81 * mm});
            skCircle(sketch, "E162", {"center": v(88.9, 774.7) * mm, "radius": 3.81 * mm});
            skCircle(sketch, "E163", {"center": v(88.9, 749.3) * mm, "radius": 3.81 * mm});
            skCircle(sketch, "E164", {"center": v(88.9, 723.9) * mm, "radius": 3.81 * mm});
            skCircle(sketch, "E165", {"center": v(88.9, 698.5) * mm, "radius": 3.81 * mm});
            skCircle(sketch, "E166", {"center": v(88.9, 673.1) * mm, "radius": 3.81 * mm});
            skCircle(sketch, "E167", {"center": v(88.9, 647.7) * mm, "radius": 3.81 * mm});
            skCircle(sketch, "E168", {"center": v(88.9, 622.3) * mm, "radius": 3.81 * mm});
            skCircle(sketch, "E169", {"center": v(88.9, 596.9) * mm, "radius": 3.81 * mm});
            skCircle(sketch, "E170", {"center": v(88.9, 571.5) * mm, "radius": 3.81 * mm});
            skCircle(sketch, "E171", {"center": v(88.9, 1003.3) * mm, "radius": 3.81 * mm});
            skCircle(sketch, "E172", {"center": v(88.9, 977.9) * mm, "radius": 3.81 * mm});
            skCircle(sketch, "E173", {"center": v(88.9, 952.5) * mm, "radius": 3.81 * mm});
            skCircle(sketch, "E174", {"center": v(88.9, 927.1) * mm, "radius": 3.81 * mm});
            skCircle(sketch, "E175", {"center": v(88.9, 901.7) * mm, "radius": 3.81 * mm});
            skCircle(sketch, "E176", {"center": v(88.9, 876.3) * mm, "radius": 3.8 * mm});
            skCircle(sketch, "E177", {"center": v(88.9, 850.9) * mm, "radius": 3.81 * mm});
            skCircle(sketch, "E178", {"center": v(88.9, 825.5) * mm, "radius": 3.81 * mm});
            skSolve(sketch);
        }
        {
            var Q0;
            Q0=makeQuery(id+"F16.imprint","IMPRINT",FACE,{"disambiguationData":[TD([[makeQuery(id+"F16.imprint","IMPRINT",EDGE,{"derivedFrom":sQuery(id+"F16.wireOp",EDGE,"E108")}),1.0]])]});
            var Q1;
            Q1=makeQuery(id+"F16.imprint","IMPRINT",FACE,{"disambiguationData":[TD([[makeQuery(id+"F16.imprint","IMPRINT",EDGE,{"derivedFrom":sQuery(id+"F16.wireOp",EDGE,"E106")}),1.0]])]});
            extrude(context, id + "F24", {"entities" : qUnion([Q0, Q1]), "depth" : 6.35 * mm, "offsetDistance" : 25.4 * mm});
        }
        {
            var Q0;
            Q0=makeQuery(id+"F24.opExtrude","SWEPT_BODY",BODY,{"disambiguationData":[OSD([sQuery(id+"F16.wireOp",EDGE,"E108")])]});
            var Q1;
            Q1=makeQuery(id+"F24.opExtrude","SWEPT_BODY",BODY,{"disambiguationData":[OSD([sQuery(id+"F16.wireOp",EDGE,"E106")])]});
            deleteBodies(context, id + "F25", {"entities" : qUnion([Q0, Q1])});
        }
        {
            var Q0;
            Q0=makeQuery(id+"F16.imprint","IMPRINT",FACE,{"disambiguationData":[TD([[makeQuery(id+"F16.imprint","IMPRINT",EDGE,{"derivedFrom":sQuery(id+"F16.wireOp",EDGE,"E108")}),1.0]])]});
            var Q1;
            Q1=makeQuery(id+"F16.imprint","IMPRINT",FACE,{"disambiguationData":[TD([[makeQuery(id+"F16.imprint","IMPRINT",EDGE,{"derivedFrom":sQuery(id+"F16.wireOp",EDGE,"E106")}),1.0]])]});
            extrude(context, id + "F26", {"entities" : qUnion([Q0, Q1]), "depth" : 5.08 * mm, "offsetDistance" : 25.4 * mm});
        }
        {
            var Q0;
            Q0=makeQuery(id+"F16.imprint","IMPRINT",FACE,{"disambiguationData":[TD([[makeQuery(id+"F16.imprint","IMPRINT",EDGE,{"derivedFrom":sQuery(id+"F16.wireOp",EDGE,"E108")}),1.0]])]});
            var Q1;
            Q1=makeQuery(id+"F16.imprint","IMPRINT",FACE,{"disambiguationData":[TD([[makeQuery(id+"F16.imprint","IMPRINT",EDGE,{"derivedFrom":sQuery(id+"F16.wireOp",EDGE,"E106")}),1.0]])]});
            extrude(context, id + "F27", {"entities" : qUnion([Q0, Q1]), "depth" : -25.4 * mm, "offsetDistance" : 25.4 * mm});
        }
        {
            var Q0;
            Q0=makeQuery(id+"F23.imprint","IMPRINT",FACE,{"disambiguationData":[TD([[makeQuery(id+"F23.imprint","IMPRINT",EDGE,{"derivedFrom":sQuery(id+"F23.wireOp",EDGE,"E170")}),1.0]])]});
            var Q1;
            Q1=makeQuery(id+"F23.imprint","IMPRINT",FACE,{"disambiguationData":[TD([[makeQuery(id+"F23.imprint","IMPRINT",EDGE,{"derivedFrom":sQuery(id+"F23.wireOp",EDGE,"E169")}),1.0]])]});
            var Q2;
            Q2=makeQuery(id+"F23.imprint","IMPRINT",FACE,{"disambiguationData":[TD([[makeQuery(id+"F23.imprint","IMPRINT",EDGE,{"derivedFrom":sQuery(id+"F23.wireOp",EDGE,"E167")}),1.0]])]});
            var Q3;
            Q3=makeQuery(id+"F23.imprint","IMPRINT",FACE,{"disambiguationData":[TD([[makeQuery(id+"F23.imprint","IMPRINT",EDGE,{"derivedFrom":sQuery(id+"F23.wireOp",EDGE,"E168")}),1.0]])]});
            var Q4;
            Q4=makeQuery(id+"F23.imprint","IMPRINT",FACE,{"disambiguationData":[TD([[makeQuery(id+"F23.imprint","IMPRINT",EDGE,{"derivedFrom":sQuery(id+"F23.wireOp",EDGE,"E166")}),1.0]])]});
            var Q5;
            Q5=makeQuery(id+"F23.imprint","IMPRINT",FACE,{"disambiguationData":[TD([[makeQuery(id+"F23.imprint","IMPRINT",EDGE,{"derivedFrom":sQuery(id+"F23.wireOp",EDGE,"E165")}),1.0]])]});
            var Q6;
            Q6=makeQuery(id+"F23.imprint","IMPRINT",FACE,{"disambiguationData":[TD([[makeQuery(id+"F23.imprint","IMPRINT",EDGE,{"derivedFrom":sQuery(id+"F23.wireOp",EDGE,"E164")}),1.0]])]});
            var Q7;
            Q7=makeQuery(id+"F23.imprint","IMPRINT",FACE,{"disambiguationData":[TD([[makeQuery(id+"F23.imprint","IMPRINT",EDGE,{"derivedFrom":sQuery(id+"F23.wireOp",EDGE,"E163")}),1.0]])]});
            var Q8;
            Q8=makeQuery(id+"F23.imprint","IMPRINT",FACE,{"disambiguationData":[TD([[makeQuery(id+"F23.imprint","IMPRINT",EDGE,{"derivedFrom":sQuery(id+"F23.wireOp",EDGE,"E162")}),1.0]])]});
            var Q9;
            Q9=makeQuery(id+"F23.imprint","IMPRINT",FACE,{"disambiguationData":[TD([[makeQuery(id+"F23.imprint","IMPRINT",EDGE,{"derivedFrom":sQuery(id+"F23.wireOp",EDGE,"E161")}),1.0]])]});
            var Q10;
            Q10=makeQuery(id+"F23.imprint","IMPRINT",FACE,{"disambiguationData":[TD([[makeQuery(id+"F23.imprint","IMPRINT",EDGE,{"derivedFrom":sQuery(id+"F23.wireOp",EDGE,"E178")}),1.0]])]});
            var Q11;
            Q11=makeQuery(id+"F23.imprint","IMPRINT",FACE,{"disambiguationData":[TD([[makeQuery(id+"F23.imprint","IMPRINT",EDGE,{"derivedFrom":sQuery(id+"F23.wireOp",EDGE,"E177")}),1.0]])]});
            var Q12;
            Q12=makeQuery(id+"F23.imprint","IMPRINT",FACE,{"disambiguationData":[TD([[makeQuery(id+"F23.imprint","IMPRINT",EDGE,{"derivedFrom":sQuery(id+"F23.wireOp",EDGE,"E176")}),1.0]])]});
            var Q13;
            Q13=makeQuery(id+"F23.imprint","IMPRINT",FACE,{"disambiguationData":[TD([[makeQuery(id+"F23.imprint","IMPRINT",EDGE,{"derivedFrom":sQuery(id+"F23.wireOp",EDGE,"E175")}),1.0]])]});
            var Q14;
            Q14=makeQuery(id+"F23.imprint","IMPRINT",FACE,{"disambiguationData":[TD([[makeQuery(id+"F23.imprint","IMPRINT",EDGE,{"derivedFrom":sQuery(id+"F23.wireOp",EDGE,"E174")}),1.0]])]});
            var Q15;
            Q15=makeQuery(id+"F23.imprint","IMPRINT",FACE,{"disambiguationData":[TD([[makeQuery(id+"F23.imprint","IMPRINT",EDGE,{"derivedFrom":sQuery(id+"F23.wireOp",EDGE,"E173")}),1.0]])]});
            var Q16;
            Q16=makeQuery(id+"F23.imprint","IMPRINT",FACE,{"disambiguationData":[TD([[makeQuery(id+"F23.imprint","IMPRINT",EDGE,{"derivedFrom":sQuery(id+"F23.wireOp",EDGE,"E172")}),1.0]])]});
            var Q17;
            Q17=makeQuery(id+"F23.imprint","IMPRINT",FACE,{"disambiguationData":[TD([[makeQuery(id+"F23.imprint","IMPRINT",EDGE,{"derivedFrom":sQuery(id+"F23.wireOp",EDGE,"E171")}),1.0]])]});
            extrude(context, id + "F28", {"entities" : qUnion([Q0, Q1, Q2, Q3, Q4, Q5, Q6, Q7, Q8, Q9, Q10, Q11, Q12, Q13, Q14, Q15, Q16, Q17]), "operationType" : NewBodyOperationType.REMOVE, "oppositeDirection" : true, "depth" : 25.4 * mm, "offsetDistance" : 25.4 * mm});
        }
        {
            var Q0;
            {var subQ0=sQuery(id+"F2.wireOp",EDGE,"E5.top");var subQ1=makeQuery(id+"F2.imprint","INTERSECT",VERTEX,{"derivedFrom":[sQuery(id+"F2.wireOp",EDGE,"E2.right"),subQ0]});Q0=makeQuery(id+"F5.boolean.opBoolean","MERGE",FACE,{"derivedFrom":[makeQuery(id+"F3.opExtrude","SWEPT_FACE",FACE,{"disambiguationData":[OSD([subQ0]),TDD([makeQuery(id+"F2.imprint","IMPRINT",EDGE,{"disambiguationData":[TD([[subQ1,-1.0]])],"derivedFrom":subQ0})])]}),makeQuery(id+"F5.opExtrude","SWEPT_FACE",FACE,{"disambiguationData":[OSD([subQ0]),TDD([makeQuery(id+"F2.imprint","IMPRINT",EDGE,{"disambiguationData":[TD([[subQ1,1.0]])],"derivedFrom":subQ0})])]})]});}
            var sketch = newSketch(context, id + "F29", { "sketchPlane" : qUnion([Q0])});
            skLineSegment(sketch, "E179.bottom", {"start": v(-381, 25.4) * mm, "end": v(-342.9, 25.4) * mm});
            skLineSegment(sketch, "E179.top", {"start": v(-381, 50.8) * mm, "end": v(-342.9, 50.8) * mm});
            skLineSegment(sketch, "E179.left", {"start": v(-381, 25.4) * mm, "end": v(-381, 50.8) * mm});
            skLineSegment(sketch, "E179.right", {"start": v(-342.9, 25.4) * mm, "end": v(-342.9, 50.8) * mm});
            skLineSegment(sketch, "E180.top", {"start": v(-381, 76.2) * mm, "end": v(-342.9, 76.2) * mm});
            skLineSegment(sketch, "E180.left", {"start": v(-381, 50.8) * mm, "end": v(-381, 76.2) * mm});
            skLineSegment(sketch, "E180.right", {"start": v(-342.9, 50.8) * mm, "end": v(-342.9, 76.2) * mm});
            skLineSegment(sketch, "E181.top", {"start": v(-381, 101.6) * mm, "end": v(-342.9, 101.6) * mm});
            skLineSegment(sketch, "E181.left", {"start": v(-381, 76.2) * mm, "end": v(-381, 101.6) * mm});
            skLineSegment(sketch, "E181.right", {"start": v(-342.9, 76.2) * mm, "end": v(-342.9, 101.6) * mm});
            skLineSegment(sketch, "E182.top", {"start": v(-381, 127) * mm, "end": v(-342.9, 127) * mm});
            skLineSegment(sketch, "E182.left", {"start": v(-381, 101.6) * mm, "end": v(-381, 127) * mm});
            skLineSegment(sketch, "E182.right", {"start": v(-342.9, 101.6) * mm, "end": v(-342.9, 127) * mm});
            skLineSegment(sketch, "E183.top", {"start": v(-381, 152.4) * mm, "end": v(-342.9, 152.4) * mm});
            skLineSegment(sketch, "E183.left", {"start": v(-381, 127) * mm, "end": v(-381, 152.4) * mm});
            skLineSegment(sketch, "E183.right", {"start": v(-342.9, 127) * mm, "end": v(-342.9, 152.4) * mm});
            skLineSegment(sketch, "E184.top", {"start": v(-381, 177.8) * mm, "end": v(-342.9, 177.8) * mm});
            skLineSegment(sketch, "E184.left", {"start": v(-381, 152.4) * mm, "end": v(-381, 177.8) * mm});
            skLineSegment(sketch, "E184.right", {"start": v(-342.9, 152.4) * mm, "end": v(-342.9, 177.8) * mm});
            skLineSegment(sketch, "E185.top", {"start": v(-381, 203.2) * mm, "end": v(-342.9, 203.2) * mm});
            skLineSegment(sketch, "E185.left", {"start": v(-381, 177.8) * mm, "end": v(-381, 203.2) * mm});
            skLineSegment(sketch, "E185.right", {"start": v(-342.9, 177.8) * mm, "end": v(-342.9, 203.2) * mm});
            skLineSegment(sketch, "E186.top", {"start": v(-381, 228.6) * mm, "end": v(-342.9, 228.6) * mm});
            skLineSegment(sketch, "E186.left", {"start": v(-381, 203.2) * mm, "end": v(-381, 228.6) * mm});
            skLineSegment(sketch, "E186.right", {"start": v(-342.9, 203.2) * mm, "end": v(-342.9, 228.6) * mm});
            skLineSegment(sketch, "E187.top", {"start": v(-381, 254) * mm, "end": v(-342.9, 254) * mm});
            skLineSegment(sketch, "E187.left", {"start": v(-381, 228.6) * mm, "end": v(-381, 254) * mm});
            skLineSegment(sketch, "E187.right", {"start": v(-342.9, 228.6) * mm, "end": v(-342.9, 254) * mm});
            skLineSegment(sketch, "E188.top", {"start": v(-381, 279.4) * mm, "end": v(-342.9, 279.4) * mm});
            skLineSegment(sketch, "E188.left", {"start": v(-381, 254) * mm, "end": v(-381, 279.4) * mm});
            skLineSegment(sketch, "E188.right", {"start": v(-342.9, 254) * mm, "end": v(-342.9, 279.4) * mm});
            skLineSegment(sketch, "E189.top", {"start": v(-381, 304.8) * mm, "end": v(-342.9, 304.8) * mm});
            skLineSegment(sketch, "E189.left", {"start": v(-381, 279.4) * mm, "end": v(-381, 304.8) * mm});
            skLineSegment(sketch, "E189.right", {"start": v(-342.9, 279.4) * mm, "end": v(-342.9, 304.8) * mm});
            skLineSegment(sketch, "E190.top", {"start": v(-381, 330.2) * mm, "end": v(-342.9, 330.2) * mm});
            skLineSegment(sketch, "E190.left", {"start": v(-381, 304.8) * mm, "end": v(-381, 330.2) * mm});
            skLineSegment(sketch, "E190.right", {"start": v(-342.9, 304.8) * mm, "end": v(-342.9, 330.2) * mm});
            skLineSegment(sketch, "E191.top", {"start": v(-381, 355.6) * mm, "end": v(-342.9, 355.6) * mm});
            skLineSegment(sketch, "E191.left", {"start": v(-381, 330.2) * mm, "end": v(-381, 355.6) * mm});
            skLineSegment(sketch, "E191.right", {"start": v(-342.9, 330.2) * mm, "end": v(-342.9, 355.6) * mm});
            skLineSegment(sketch, "E192.top", {"start": v(-381, 381) * mm, "end": v(-342.9, 381) * mm});
            skLineSegment(sketch, "E192.left", {"start": v(-381, 355.6) * mm, "end": v(-381, 381) * mm});
            skLineSegment(sketch, "E192.right", {"start": v(-342.9, 355.6) * mm, "end": v(-342.9, 381) * mm});
            skLineSegment(sketch, "E193.top", {"start": v(-381, 406.4) * mm, "end": v(-342.9, 406.4) * mm});
            skLineSegment(sketch, "E193.left", {"start": v(-381, 381) * mm, "end": v(-381, 406.4) * mm});
            skLineSegment(sketch, "E193.right", {"start": v(-342.9, 381) * mm, "end": v(-342.9, 406.4) * mm});
            skLineSegment(sketch, "E194.bottom", {"start": v(-381, 406.4) * mm, "end": v(-338.79, 406.4) * mm});
            skLineSegment(sketch, "E194.top", {"start": v(-381, 431.8) * mm, "end": v(-338.79, 431.8) * mm});
            skLineSegment(sketch, "E194.left", {"start": v(-381, 406.4) * mm, "end": v(-381, 431.8) * mm});
            skLineSegment(sketch, "E194.right", {"start": v(-338.79, 406.4) * mm, "end": v(-338.79, 431.8) * mm});
            skLineSegment(sketch, "E195.bottom", {"start": v(-381, 431.8) * mm, "end": v(-342.9, 431.8) * mm});
            skLineSegment(sketch, "E195.top", {"start": v(-381, 457.2) * mm, "end": v(-342.9, 457.2) * mm});
            skLineSegment(sketch, "E195.left", {"start": v(-381, 431.8) * mm, "end": v(-381, 457.2) * mm});
            skLineSegment(sketch, "E195.right", {"start": v(-342.9, 431.8) * mm, "end": v(-342.9, 457.2) * mm});
            skLineSegment(sketch, "E196.top", {"start": v(-381, 482.6) * mm, "end": v(-342.9, 482.6) * mm});
            skLineSegment(sketch, "E196.left", {"start": v(-381, 457.2) * mm, "end": v(-381, 482.6) * mm});
            skLineSegment(sketch, "E196.right", {"start": v(-342.9, 457.2) * mm, "end": v(-342.9, 482.6) * mm});
            skLineSegment(sketch, "E197.top", {"start": v(-381, 508) * mm, "end": v(-342.9, 508) * mm});
            skLineSegment(sketch, "E197.left", {"start": v(-381, 482.6) * mm, "end": v(-381, 508) * mm});
            skLineSegment(sketch, "E197.right", {"start": v(-342.9, 482.6) * mm, "end": v(-342.9, 508) * mm});
            skLineSegment(sketch, "E198.top", {"start": v(-381, 533.4) * mm, "end": v(-342.9, 533.4) * mm});
            skLineSegment(sketch, "E198.left", {"start": v(-381, 508) * mm, "end": v(-381, 533.4) * mm});
            skLineSegment(sketch, "E198.right", {"start": v(-342.9, 508) * mm, "end": v(-342.9, 533.4) * mm});
            skCircle(sketch, "E199", {"center": v(-361.95, 546.1) * mm, "radius": 3.8 * mm});
            skCircle(sketch, "E200", {"center": v(-361.95, 520.7) * mm, "radius": 3.81 * mm});
            skCircle(sketch, "E201", {"center": v(-361.95, 495.3) * mm, "radius": 3.81 * mm});
            skCircle(sketch, "E202", {"center": v(-361.95, 469.9) * mm, "radius": 3.81 * mm});
            skCircle(sketch, "E203", {"center": v(-361.95, 419.1) * mm, "radius": 3.81 * mm});
            skCircle(sketch, "E204", {"center": v(-361.95, 444.5) * mm, "radius": 3.81 * mm});
            skCircle(sketch, "E205", {"center": v(-361.95, 393.7) * mm, "radius": 3.81 * mm});
            skCircle(sketch, "E206", {"center": v(-361.95, 368.3) * mm, "radius": 3.81 * mm});
            skCircle(sketch, "E207", {"center": v(-361.95, 342.9) * mm, "radius": 3.81 * mm});
            skCircle(sketch, "E208", {"center": v(-361.95, 317.5) * mm, "radius": 3.81 * mm});
            skCircle(sketch, "E209", {"center": v(-361.95, 292.1) * mm, "radius": 3.8 * mm});
            skCircle(sketch, "E210", {"center": v(-361.95, 266.7) * mm, "radius": 3.81 * mm});
            skCircle(sketch, "E211", {"center": v(-361.95, 241.3) * mm, "radius": 3.8 * mm});
            skCircle(sketch, "E212", {"center": v(-361.95, 215.9) * mm, "radius": 3.81 * mm});
            skCircle(sketch, "E213", {"center": v(-361.95, 190.5) * mm, "radius": 3.81 * mm});
            skCircle(sketch, "E214", {"center": v(-361.95, 165.1) * mm, "radius": 3.81 * mm});
            skCircle(sketch, "E215", {"center": v(-361.95, 139.7) * mm, "radius": 3.81 * mm});
            skCircle(sketch, "E216", {"center": v(-361.95, 114.3) * mm, "radius": 3.8 * mm});
            skCircle(sketch, "E217", {"center": v(-361.95, 88.9) * mm, "radius": 3.81 * mm});
            skCircle(sketch, "E218", {"center": v(-361.95, 63.5) * mm, "radius": 3.81 * mm});
            skCircle(sketch, "E219", {"center": v(-361.95, 38.1) * mm, "radius": 3.8 * mm});
            skSolve(sketch);
        }
        {
            var Q0;
            Q0=makeQuery(id+"F29.imprint","IMPRINT",FACE,{"disambiguationData":[TD([[makeQuery(id+"F29.imprint","IMPRINT",EDGE,{"derivedFrom":sQuery(id+"F29.wireOp",EDGE,"E199")}),1.0]])]});
            var Q1;
            Q1=makeQuery(id+"F29.imprint","IMPRINT",FACE,{"disambiguationData":[TD([[makeQuery(id+"F29.imprint","IMPRINT",EDGE,{"derivedFrom":sQuery(id+"F29.wireOp",EDGE,"E200")}),1.0]])]});
            var Q2;
            Q2=makeQuery(id+"F29.imprint","IMPRINT",FACE,{"disambiguationData":[TD([[makeQuery(id+"F29.imprint","IMPRINT",EDGE,{"derivedFrom":sQuery(id+"F29.wireOp",EDGE,"E201")}),1.0]])]});
            var Q3;
            Q3=makeQuery(id+"F29.imprint","IMPRINT",FACE,{"disambiguationData":[TD([[makeQuery(id+"F29.imprint","IMPRINT",EDGE,{"derivedFrom":sQuery(id+"F29.wireOp",EDGE,"E202")}),1.0]])]});
            var Q4;
            Q4=makeQuery(id+"F29.imprint","IMPRINT",FACE,{"disambiguationData":[TD([[makeQuery(id+"F29.imprint","IMPRINT",EDGE,{"derivedFrom":sQuery(id+"F29.wireOp",EDGE,"E204")}),1.0]])]});
            var Q5;
            Q5=makeQuery(id+"F29.imprint","IMPRINT",FACE,{"disambiguationData":[TD([[makeQuery(id+"F29.imprint","IMPRINT",EDGE,{"derivedFrom":sQuery(id+"F29.wireOp",EDGE,"E203")}),1.0]])]});
            var Q6;
            Q6=makeQuery(id+"F29.imprint","IMPRINT",FACE,{"disambiguationData":[TD([[makeQuery(id+"F29.imprint","IMPRINT",EDGE,{"derivedFrom":sQuery(id+"F29.wireOp",EDGE,"E205")}),1.0]])]});
            var Q7;
            Q7=makeQuery(id+"F29.imprint","IMPRINT",FACE,{"disambiguationData":[TD([[makeQuery(id+"F29.imprint","IMPRINT",EDGE,{"derivedFrom":sQuery(id+"F29.wireOp",EDGE,"E206")}),1.0]])]});
            var Q8;
            Q8=makeQuery(id+"F29.imprint","IMPRINT",FACE,{"disambiguationData":[TD([[makeQuery(id+"F29.imprint","IMPRINT",EDGE,{"derivedFrom":sQuery(id+"F29.wireOp",EDGE,"E207")}),1.0]])]});
            var Q9;
            Q9=makeQuery(id+"F29.imprint","IMPRINT",FACE,{"disambiguationData":[TD([[makeQuery(id+"F29.imprint","IMPRINT",EDGE,{"derivedFrom":sQuery(id+"F29.wireOp",EDGE,"E208")}),1.0]])]});
            var Q10;
            Q10=makeQuery(id+"F29.imprint","IMPRINT",FACE,{"disambiguationData":[TD([[makeQuery(id+"F29.imprint","IMPRINT",EDGE,{"derivedFrom":sQuery(id+"F29.wireOp",EDGE,"E209")}),1.0]])]});
            var Q11;
            Q11=makeQuery(id+"F29.imprint","IMPRINT",FACE,{"disambiguationData":[TD([[makeQuery(id+"F29.imprint","IMPRINT",EDGE,{"derivedFrom":sQuery(id+"F29.wireOp",EDGE,"E210")}),1.0]])]});
            var Q12;
            Q12=makeQuery(id+"F29.imprint","IMPRINT",FACE,{"disambiguationData":[TD([[makeQuery(id+"F29.imprint","IMPRINT",EDGE,{"derivedFrom":sQuery(id+"F29.wireOp",EDGE,"E211")}),1.0]])]});
            var Q13;
            Q13=makeQuery(id+"F29.imprint","IMPRINT",FACE,{"disambiguationData":[TD([[makeQuery(id+"F29.imprint","IMPRINT",EDGE,{"derivedFrom":sQuery(id+"F29.wireOp",EDGE,"E212")}),1.0]])]});
            var Q14;
            Q14=makeQuery(id+"F29.imprint","IMPRINT",FACE,{"disambiguationData":[TD([[makeQuery(id+"F29.imprint","IMPRINT",EDGE,{"derivedFrom":sQuery(id+"F29.wireOp",EDGE,"E213")}),1.0]])]});
            var Q15;
            Q15=makeQuery(id+"F29.imprint","IMPRINT",FACE,{"disambiguationData":[TD([[makeQuery(id+"F29.imprint","IMPRINT",EDGE,{"derivedFrom":sQuery(id+"F29.wireOp",EDGE,"E214")}),1.0]])]});
            var Q16;
            Q16=makeQuery(id+"F29.imprint","IMPRINT",FACE,{"disambiguationData":[TD([[makeQuery(id+"F29.imprint","IMPRINT",EDGE,{"derivedFrom":sQuery(id+"F29.wireOp",EDGE,"E215")}),1.0]])]});
            var Q17;
            Q17=makeQuery(id+"F29.imprint","IMPRINT",FACE,{"disambiguationData":[TD([[makeQuery(id+"F29.imprint","IMPRINT",EDGE,{"derivedFrom":sQuery(id+"F29.wireOp",EDGE,"E216")}),1.0]])]});
            var Q18;
            Q18=makeQuery(id+"F29.imprint","IMPRINT",FACE,{"disambiguationData":[TD([[makeQuery(id+"F29.imprint","IMPRINT",EDGE,{"derivedFrom":sQuery(id+"F29.wireOp",EDGE,"E217")}),1.0]])]});
            var Q19;
            Q19=makeQuery(id+"F29.imprint","IMPRINT",FACE,{"disambiguationData":[TD([[makeQuery(id+"F29.imprint","IMPRINT",EDGE,{"derivedFrom":sQuery(id+"F29.wireOp",EDGE,"E218")}),1.0]])]});
            var Q20;
            Q20=makeQuery(id+"F29.imprint","IMPRINT",FACE,{"disambiguationData":[TD([[makeQuery(id+"F29.imprint","IMPRINT",EDGE,{"derivedFrom":sQuery(id+"F29.wireOp",EDGE,"E219")}),1.0]])]});
            extrude(context, id + "F30", {"entities" : qUnion([Q0, Q1, Q2, Q3, Q4, Q5, Q6, Q7, Q8, Q9, Q10, Q11, Q12, Q13, Q14, Q15, Q16, Q17, Q18, Q19, Q20]), "operationType" : NewBodyOperationType.REMOVE, "oppositeDirection" : true, "depth" : 25.4 * mm, "offsetDistance" : 25.4 * mm});
        }
        {
            var Q0;
            {var subQ0=sQuery(id+"F2.wireOp",EDGE,"E5.top");var subQ1=makeQuery(id+"F2.imprint","INTERSECT",VERTEX,{"derivedFrom":[sQuery(id+"F2.wireOp",EDGE,"E1.right"),subQ0]});Q0=makeQuery(id+"F5.boolean.opBoolean","MERGE",FACE,{"derivedFrom":[makeQuery(id+"F3.opExtrude","SWEPT_FACE",FACE,{"disambiguationData":[OSD([subQ0]),TDD([makeQuery(id+"F2.imprint","IMPRINT",EDGE,{"disambiguationData":[TD([[subQ1,1.0]])],"derivedFrom":subQ0})])]}),makeQuery(id+"F5.opExtrude","SWEPT_FACE",FACE,{"disambiguationData":[OSD([subQ0]),TDD([makeQuery(id+"F2.imprint","IMPRINT",EDGE,{"disambiguationData":[TD([[makeQuery(id+"F2.imprint","INTERSECT",VERTEX,{"derivedFrom":[subQ0,sQuery(id+"F2.wireOp",EDGE,"E6.right")]}),1.0]])],"derivedFrom":subQ0})])]})]});}
            var sketch = newSketch(context, id + "F31", { "sketchPlane" : qUnion([Q0])});
            skLineSegment(sketch, "E220.bottom", {"start": v(342.9, 558.8) * mm, "end": v(381, 558.8) * mm});
            skLineSegment(sketch, "E220.top", {"start": v(342.9, 533.4) * mm, "end": v(381, 533.4) * mm});
            skLineSegment(sketch, "E220.left", {"start": v(342.9, 558.8) * mm, "end": v(342.9, 533.4) * mm});
            skLineSegment(sketch, "E220.right", {"start": v(381, 558.8) * mm, "end": v(381, 533.4) * mm});
            skLineSegment(sketch, "E221.top", {"start": v(342.9, 508) * mm, "end": v(381, 508) * mm});
            skLineSegment(sketch, "E221.left", {"start": v(342.9, 533.4) * mm, "end": v(342.9, 508) * mm});
            skLineSegment(sketch, "E221.right", {"start": v(381, 533.4) * mm, "end": v(381, 508) * mm});
            skLineSegment(sketch, "E222.top", {"start": v(342.9, 482.6) * mm, "end": v(381, 482.6) * mm});
            skLineSegment(sketch, "E222.left", {"start": v(342.9, 508) * mm, "end": v(342.9, 482.6) * mm});
            skLineSegment(sketch, "E222.right", {"start": v(381, 508) * mm, "end": v(381, 482.6) * mm});
            skLineSegment(sketch, "E223.top", {"start": v(342.9, 457.2) * mm, "end": v(381, 457.2) * mm});
            skLineSegment(sketch, "E223.left", {"start": v(342.9, 482.6) * mm, "end": v(342.9, 457.2) * mm});
            skLineSegment(sketch, "E223.right", {"start": v(381, 482.6) * mm, "end": v(381, 457.2) * mm});
            skLineSegment(sketch, "E224.top", {"start": v(342.9, 431.8) * mm, "end": v(381, 431.8) * mm});
            skLineSegment(sketch, "E224.left", {"start": v(342.9, 457.2) * mm, "end": v(342.9, 431.8) * mm});
            skLineSegment(sketch, "E224.right", {"start": v(381, 457.2) * mm, "end": v(381, 431.8) * mm});
            skCircle(sketch, "E225", {"center": v(361.95, 546.1) * mm, "radius": 3.81 * mm});
            skCircle(sketch, "E226", {"center": v(361.95, 520.7) * mm, "radius": 3.81 * mm});
            skCircle(sketch, "E227", {"center": v(361.95, 495.3) * mm, "radius": 3.81 * mm});
            skCircle(sketch, "E228", {"center": v(361.95, 469.9) * mm, "radius": 3.81 * mm});
            skCircle(sketch, "E229", {"center": v(361.95, 444.5) * mm, "radius": 3.81 * mm});
            skLineSegment(sketch, "E230.top", {"start": v(342.9, 406.4) * mm, "end": v(381, 406.4) * mm});
            skLineSegment(sketch, "E230.left", {"start": v(342.9, 431.8) * mm, "end": v(342.9, 406.4) * mm});
            skLineSegment(sketch, "E230.right", {"start": v(381, 431.8) * mm, "end": v(381, 406.4) * mm});
            skLineSegment(sketch, "E231.top", {"start": v(342.9, 381) * mm, "end": v(381, 381) * mm});
            skLineSegment(sketch, "E231.left", {"start": v(342.9, 406.4) * mm, "end": v(342.9, 381) * mm});
            skLineSegment(sketch, "E231.right", {"start": v(381, 406.4) * mm, "end": v(381, 381) * mm});
            skLineSegment(sketch, "E232.top", {"start": v(342.9, 355.6) * mm, "end": v(381, 355.6) * mm});
            skLineSegment(sketch, "E232.left", {"start": v(342.9, 381) * mm, "end": v(342.9, 355.6) * mm});
            skLineSegment(sketch, "E232.right", {"start": v(381, 381) * mm, "end": v(381, 355.6) * mm});
            skLineSegment(sketch, "E233.top", {"start": v(342.9, 330.2) * mm, "end": v(381, 330.2) * mm});
            skLineSegment(sketch, "E233.left", {"start": v(342.9, 355.6) * mm, "end": v(342.9, 330.2) * mm});
            skLineSegment(sketch, "E233.right", {"start": v(381, 355.6) * mm, "end": v(381, 330.2) * mm});
            skLineSegment(sketch, "E234.top", {"start": v(342.9, 304.8) * mm, "end": v(381, 304.8) * mm});
            skLineSegment(sketch, "E234.left", {"start": v(342.9, 330.2) * mm, "end": v(342.9, 304.8) * mm});
            skLineSegment(sketch, "E234.right", {"start": v(381, 330.2) * mm, "end": v(381, 304.8) * mm});
            skLineSegment(sketch, "E235.top", {"start": v(342.9, 279.4) * mm, "end": v(381, 279.4) * mm});
            skLineSegment(sketch, "E235.left", {"start": v(342.9, 304.8) * mm, "end": v(342.9, 279.4) * mm});
            skLineSegment(sketch, "E235.right", {"start": v(381, 304.8) * mm, "end": v(381, 279.4) * mm});
            skLineSegment(sketch, "E236.top", {"start": v(342.9, 254) * mm, "end": v(381, 254) * mm});
            skLineSegment(sketch, "E236.left", {"start": v(342.9, 279.4) * mm, "end": v(342.9, 254) * mm});
            skLineSegment(sketch, "E236.right", {"start": v(381, 279.4) * mm, "end": v(381, 254) * mm});
            skLineSegment(sketch, "E237.top", {"start": v(342.9, 228.6) * mm, "end": v(381, 228.6) * mm});
            skLineSegment(sketch, "E237.left", {"start": v(342.9, 254) * mm, "end": v(342.9, 228.6) * mm});
            skLineSegment(sketch, "E237.right", {"start": v(381, 254) * mm, "end": v(381, 228.6) * mm});
            skLineSegment(sketch, "E238.top", {"start": v(342.9, 203.2) * mm, "end": v(381, 203.2) * mm});
            skLineSegment(sketch, "E238.left", {"start": v(342.9, 228.6) * mm, "end": v(342.9, 203.2) * mm});
            skLineSegment(sketch, "E238.right", {"start": v(381, 228.6) * mm, "end": v(381, 203.2) * mm});
            skLineSegment(sketch, "E239.top", {"start": v(342.9, 177.8) * mm, "end": v(381, 177.8) * mm});
            skLineSegment(sketch, "E239.left", {"start": v(342.9, 203.2) * mm, "end": v(342.9, 177.8) * mm});
            skLineSegment(sketch, "E239.right", {"start": v(381, 203.2) * mm, "end": v(381, 177.8) * mm});
            skLineSegment(sketch, "E240.top", {"start": v(342.9, 152.4) * mm, "end": v(381, 152.4) * mm});
            skLineSegment(sketch, "E240.left", {"start": v(342.9, 177.8) * mm, "end": v(342.9, 152.4) * mm});
            skLineSegment(sketch, "E240.right", {"start": v(381, 177.8) * mm, "end": v(381, 152.4) * mm});
            skLineSegment(sketch, "E241.top", {"start": v(342.9, 127) * mm, "end": v(381, 127) * mm});
            skLineSegment(sketch, "E241.left", {"start": v(342.9, 152.4) * mm, "end": v(342.9, 127) * mm});
            skLineSegment(sketch, "E241.right", {"start": v(381, 152.4) * mm, "end": v(381, 127) * mm});
            skLineSegment(sketch, "E242.top", {"start": v(342.9, 101.6) * mm, "end": v(381, 101.6) * mm});
            skLineSegment(sketch, "E242.left", {"start": v(342.9, 127) * mm, "end": v(342.9, 101.6) * mm});
            skLineSegment(sketch, "E242.right", {"start": v(381, 127) * mm, "end": v(381, 101.6) * mm});
            skLineSegment(sketch, "E243.top", {"start": v(342.9, 76.2) * mm, "end": v(381, 76.2) * mm});
            skLineSegment(sketch, "E243.left", {"start": v(342.9, 101.6) * mm, "end": v(342.9, 76.2) * mm});
            skLineSegment(sketch, "E243.right", {"start": v(381, 101.6) * mm, "end": v(381, 76.2) * mm});
            skLineSegment(sketch, "E244.top", {"start": v(342.9, 51.8) * mm, "end": v(381, 51.8) * mm});
            skLineSegment(sketch, "E244.left", {"start": v(342.9, 76.2) * mm, "end": v(342.9, 51.8) * mm});
            skLineSegment(sketch, "E244.right", {"start": v(381, 76.2) * mm, "end": v(381, 51.8) * mm});
            skLineSegment(sketch, "E245.top", {"start": v(342.9, 25.4) * mm, "end": v(381, 25.4) * mm});
            skLineSegment(sketch, "E245.left", {"start": v(342.9, 51.8) * mm, "end": v(342.9, 25.4) * mm});
            skLineSegment(sketch, "E245.right", {"start": v(381, 51.8) * mm, "end": v(381, 25.4) * mm});
            skCircle(sketch, "E246", {"center": v(361.95, 419.1) * mm, "radius": 3.81 * mm});
            skCircle(sketch, "E247", {"center": v(361.95, 393.7) * mm, "radius": 3.8 * mm});
            skCircle(sketch, "E248", {"center": v(361.95, 368.3) * mm, "radius": 3.81 * mm});
            skCircle(sketch, "E249", {"center": v(361.95, 342.9) * mm, "radius": 3.8 * mm});
            skCircle(sketch, "E250", {"center": v(361.95, 317.5) * mm, "radius": 3.81 * mm});
            skCircle(sketch, "E251", {"center": v(361.95, 292.1) * mm, "radius": 3.8 * mm});
            skCircle(sketch, "E252", {"center": v(361.95, 266.7) * mm, "radius": 3.8 * mm});
            skCircle(sketch, "E253", {"center": v(361.95, 241.3) * mm, "radius": 3.81 * mm});
            skCircle(sketch, "E254", {"center": v(361.95, 215.9) * mm, "radius": 3.81 * mm});
            skCircle(sketch, "E255", {"center": v(361.95, 190.5) * mm, "radius": 3.81 * mm});
            skCircle(sketch, "E256", {"center": v(361.95, 165.1) * mm, "radius": 3.8 * mm});
            skCircle(sketch, "E257", {"center": v(361.95, 139.7) * mm, "radius": 3.81 * mm});
            skCircle(sketch, "E258", {"center": v(361.95, 114.3) * mm, "radius": 3.81 * mm});
            skCircle(sketch, "E259", {"center": v(361.95, 88.9) * mm, "radius": 3.81 * mm});
            skCircle(sketch, "E260", {"center": v(361.95, 64) * mm, "radius": 3.81 * mm});
            skCircle(sketch, "E261", {"center": v(361.95, 38.6) * mm, "radius": 3.81 * mm});
            skSolve(sketch);
        }
        {
            var Q0;
            Q0=makeQuery(id+"F31.imprint","IMPRINT",FACE,{"disambiguationData":[TD([[makeQuery(id+"F31.imprint","IMPRINT",EDGE,{"derivedFrom":sQuery(id+"F31.wireOp",EDGE,"E225")}),1.0]])]});
            var Q1;
            Q1=makeQuery(id+"F31.imprint","IMPRINT",FACE,{"disambiguationData":[TD([[makeQuery(id+"F31.imprint","IMPRINT",EDGE,{"derivedFrom":sQuery(id+"F31.wireOp",EDGE,"E226")}),1.0]])]});
            var Q2;
            Q2=makeQuery(id+"F31.imprint","IMPRINT",FACE,{"disambiguationData":[TD([[makeQuery(id+"F31.imprint","IMPRINT",EDGE,{"derivedFrom":sQuery(id+"F31.wireOp",EDGE,"E227")}),1.0]])]});
            var Q3;
            Q3=makeQuery(id+"F31.imprint","IMPRINT",FACE,{"disambiguationData":[TD([[makeQuery(id+"F31.imprint","IMPRINT",EDGE,{"derivedFrom":sQuery(id+"F31.wireOp",EDGE,"E228")}),1.0]])]});
            var Q4;
            Q4=makeQuery(id+"F31.imprint","IMPRINT",FACE,{"disambiguationData":[TD([[makeQuery(id+"F31.imprint","IMPRINT",EDGE,{"derivedFrom":sQuery(id+"F31.wireOp",EDGE,"E229")}),1.0]])]});
            var Q5;
            Q5=makeQuery(id+"F31.imprint","IMPRINT",FACE,{"disambiguationData":[TD([[makeQuery(id+"F31.imprint","IMPRINT",EDGE,{"derivedFrom":sQuery(id+"F31.wireOp",EDGE,"E247")}),1.0]])]});
            var Q6;
            Q6=makeQuery(id+"F31.imprint","IMPRINT",FACE,{"disambiguationData":[TD([[makeQuery(id+"F31.imprint","IMPRINT",EDGE,{"derivedFrom":sQuery(id+"F31.wireOp",EDGE,"E248")}),1.0]])]});
            var Q7;
            Q7=makeQuery(id+"F31.imprint","IMPRINT",FACE,{"disambiguationData":[TD([[makeQuery(id+"F31.imprint","IMPRINT",EDGE,{"derivedFrom":sQuery(id+"F31.wireOp",EDGE,"E249")}),1.0]])]});
            var Q8;
            Q8=makeQuery(id+"F31.imprint","IMPRINT",FACE,{"disambiguationData":[TD([[makeQuery(id+"F31.imprint","IMPRINT",EDGE,{"derivedFrom":sQuery(id+"F31.wireOp",EDGE,"E250")}),1.0]])]});
            var Q9;
            Q9=makeQuery(id+"F31.imprint","IMPRINT",FACE,{"disambiguationData":[TD([[makeQuery(id+"F31.imprint","IMPRINT",EDGE,{"derivedFrom":sQuery(id+"F31.wireOp",EDGE,"E251")}),1.0]])]});
            var Q10;
            Q10=makeQuery(id+"F31.imprint","IMPRINT",FACE,{"disambiguationData":[TD([[makeQuery(id+"F31.imprint","IMPRINT",EDGE,{"derivedFrom":sQuery(id+"F31.wireOp",EDGE,"E252")}),1.0]])]});
            var Q11;
            Q11=makeQuery(id+"F31.imprint","IMPRINT",FACE,{"disambiguationData":[TD([[makeQuery(id+"F31.imprint","IMPRINT",EDGE,{"derivedFrom":sQuery(id+"F31.wireOp",EDGE,"E253")}),1.0]])]});
            var Q12;
            Q12=makeQuery(id+"F31.imprint","IMPRINT",FACE,{"disambiguationData":[TD([[makeQuery(id+"F31.imprint","IMPRINT",EDGE,{"derivedFrom":sQuery(id+"F31.wireOp",EDGE,"E254")}),1.0]])]});
            var Q13;
            Q13=makeQuery(id+"F31.imprint","IMPRINT",FACE,{"disambiguationData":[TD([[makeQuery(id+"F31.imprint","IMPRINT",EDGE,{"derivedFrom":sQuery(id+"F31.wireOp",EDGE,"E255")}),1.0]])]});
            var Q14;
            Q14=makeQuery(id+"F31.imprint","IMPRINT",FACE,{"disambiguationData":[TD([[makeQuery(id+"F31.imprint","IMPRINT",EDGE,{"derivedFrom":sQuery(id+"F31.wireOp",EDGE,"E256")}),1.0]])]});
            var Q15;
            Q15=makeQuery(id+"F31.imprint","IMPRINT",FACE,{"disambiguationData":[TD([[makeQuery(id+"F31.imprint","IMPRINT",EDGE,{"derivedFrom":sQuery(id+"F31.wireOp",EDGE,"E257")}),1.0]])]});
            var Q16;
            Q16=makeQuery(id+"F31.imprint","IMPRINT",FACE,{"disambiguationData":[TD([[makeQuery(id+"F31.imprint","IMPRINT",EDGE,{"derivedFrom":sQuery(id+"F31.wireOp",EDGE,"E258")}),1.0]])]});
            var Q17;
            Q17=makeQuery(id+"F31.imprint","IMPRINT",FACE,{"disambiguationData":[TD([[makeQuery(id+"F31.imprint","IMPRINT",EDGE,{"derivedFrom":sQuery(id+"F31.wireOp",EDGE,"E259")}),1.0]])]});
            var Q18;
            Q18=makeQuery(id+"F31.imprint","IMPRINT",FACE,{"disambiguationData":[TD([[makeQuery(id+"F31.imprint","IMPRINT",EDGE,{"derivedFrom":sQuery(id+"F31.wireOp",EDGE,"E260")}),1.0]])]});
            var Q19;
            Q19=makeQuery(id+"F31.imprint","IMPRINT",FACE,{"disambiguationData":[TD([[makeQuery(id+"F31.imprint","IMPRINT",EDGE,{"derivedFrom":sQuery(id+"F31.wireOp",EDGE,"E261")}),1.0]])]});
            var Q20;
            Q20=makeQuery(id+"F31.imprint","IMPRINT",FACE,{"disambiguationData":[TD([[makeQuery(id+"F31.imprint","IMPRINT",EDGE,{"derivedFrom":sQuery(id+"F31.wireOp",EDGE,"E246")}),1.0]])]});
            extrude(context, id + "F32", {"entities" : qUnion([Q0, Q1, Q2, Q3, Q4, Q5, Q6, Q7, Q8, Q9, Q10, Q11, Q12, Q13, Q14, Q15, Q16, Q17, Q18, Q19, Q20]), "operationType" : NewBodyOperationType.REMOVE, "oppositeDirection" : true, "depth" : 25.4 * mm, "offsetDistance" : 25.4 * mm});
        }
        {
            var Q0;
            {var subQ0=sQuery(id+"F11.wireOp",EDGE,"E29.bottom");Q0=makeQuery(id+"F13.boolean.opBoolean","MERGE",FACE,{"derivedFrom":[makeQuery(id+"F12.opExtrude","SWEPT_FACE",FACE,{"disambiguationData":[OSD([subQ0])]}),makeQuery(id+"F13.opExtrude","SWEPT_FACE",FACE,{"disambiguationData":[OSD([subQ0])]})]});}
            var sketch = newSketch(context, id + "F33", { "sketchPlane" : qUnion([Q0])});
            skLineSegment(sketch, "E262.bottom", {"start": v(342.86, 1016) * mm, "end": v(374.65, 1016) * mm});
            skLineSegment(sketch, "E262.top", {"start": v(342.86, 990.6) * mm, "end": v(374.65, 990.6) * mm});
            skLineSegment(sketch, "E262.left", {"start": v(342.86, 1016) * mm, "end": v(342.86, 990.6) * mm});
            skLineSegment(sketch, "E262.right", {"start": v(374.65, 1016) * mm, "end": v(374.65, 990.6) * mm});
            skLineSegment(sketch, "E263.bottom", {"start": v(342.86, 990.6) * mm, "end": v(376.94, 990.6) * mm});
            skLineSegment(sketch, "E263.top", {"start": v(342.86, 965.2) * mm, "end": v(376.94, 965.2) * mm});
            skLineSegment(sketch, "E263.left", {"start": v(342.86, 990.6) * mm, "end": v(342.86, 965.2) * mm});
            skLineSegment(sketch, "E263.right", {"start": v(376.94, 990.6) * mm, "end": v(376.94, 965.2) * mm});
            skLineSegment(sketch, "E264.bottom", {"start": v(342.86, 965.2) * mm, "end": v(376.7, 965.2) * mm});
            skLineSegment(sketch, "E264.top", {"start": v(342.86, 939.8) * mm, "end": v(376.7, 939.8) * mm});
            skLineSegment(sketch, "E264.left", {"start": v(342.86, 965.2) * mm, "end": v(342.86, 939.8) * mm});
            skLineSegment(sketch, "E264.right", {"start": v(376.7, 965.2) * mm, "end": v(376.7, 939.8) * mm});
            skLineSegment(sketch, "E265.bottom", {"start": v(342.86, 939.8) * mm, "end": v(374.65, 939.8) * mm});
            skLineSegment(sketch, "E265.top", {"start": v(342.86, 914.4) * mm, "end": v(374.65, 914.4) * mm});
            skLineSegment(sketch, "E265.left", {"start": v(342.86, 939.8) * mm, "end": v(342.86, 914.4) * mm});
            skLineSegment(sketch, "E265.right", {"start": v(374.65, 939.8) * mm, "end": v(374.65, 914.4) * mm});
            skCircle(sketch, "E266", {"center": v(358.76, 1003.3) * mm, "radius": 3.81 * mm});
            skCircle(sketch, "E267", {"center": v(358.76, 977.9) * mm, "radius": 3.81 * mm});
            skCircle(sketch, "E268", {"center": v(358.76, 952.5) * mm, "radius": 3.81 * mm});
            skCircle(sketch, "E269", {"center": v(358.76, 927.1) * mm, "radius": 3.81 * mm});
            skLineSegment(sketch, "E270.top", {"start": v(342.86, 889) * mm, "end": v(374.65, 889) * mm});
            skLineSegment(sketch, "E270.left", {"start": v(342.86, 914.4) * mm, "end": v(342.86, 889) * mm});
            skLineSegment(sketch, "E270.right", {"start": v(374.65, 914.4) * mm, "end": v(374.65, 889) * mm});
            skLineSegment(sketch, "E271.top", {"start": v(342.86, 863.6) * mm, "end": v(374.65, 863.6) * mm});
            skLineSegment(sketch, "E271.left", {"start": v(342.86, 889) * mm, "end": v(342.86, 863.6) * mm});
            skLineSegment(sketch, "E271.right", {"start": v(374.65, 889) * mm, "end": v(374.65, 863.6) * mm});
            skLineSegment(sketch, "E272.top", {"start": v(342.86, 838.2) * mm, "end": v(374.65, 838.2) * mm});
            skLineSegment(sketch, "E272.left", {"start": v(342.86, 863.6) * mm, "end": v(342.86, 838.2) * mm});
            skLineSegment(sketch, "E272.right", {"start": v(374.65, 863.6) * mm, "end": v(374.65, 838.2) * mm});
            skLineSegment(sketch, "E273.top", {"start": v(342.86, 812.8) * mm, "end": v(374.65, 812.8) * mm});
            skLineSegment(sketch, "E273.left", {"start": v(342.86, 838.2) * mm, "end": v(342.86, 812.8) * mm});
            skLineSegment(sketch, "E273.right", {"start": v(374.65, 838.2) * mm, "end": v(374.65, 812.8) * mm});
            skLineSegment(sketch, "E274.top", {"start": v(342.86, 787.4) * mm, "end": v(374.65, 787.4) * mm});
            skLineSegment(sketch, "E274.left", {"start": v(342.86, 812.8) * mm, "end": v(342.86, 787.4) * mm});
            skLineSegment(sketch, "E274.right", {"start": v(374.65, 812.8) * mm, "end": v(374.65, 787.4) * mm});
            skCircle(sketch, "E275", {"center": v(358.76, 901.7) * mm, "radius": 3.81 * mm});
            skCircle(sketch, "E276", {"center": v(358.76, 876.3) * mm, "radius": 3.81 * mm});
            skCircle(sketch, "E277", {"center": v(358.76, 850.9) * mm, "radius": 3.81 * mm});
            skCircle(sketch, "E278", {"center": v(358.76, 825.5) * mm, "radius": 3.81 * mm});
            skCircle(sketch, "E279", {"center": v(358.76, 800.1) * mm, "radius": 3.81 * mm});
            skLineSegment(sketch, "E280.top", {"start": v(342.86, 762) * mm, "end": v(374.65, 762) * mm});
            skLineSegment(sketch, "E280.left", {"start": v(342.86, 787.4) * mm, "end": v(342.86, 762) * mm});
            skLineSegment(sketch, "E280.right", {"start": v(374.65, 787.4) * mm, "end": v(374.65, 762) * mm});
            skLineSegment(sketch, "E281.bottom", {"start": v(342.86, 762) * mm, "end": v(377.84, 762) * mm});
            skLineSegment(sketch, "E281.top", {"start": v(342.86, 736.6) * mm, "end": v(377.84, 736.6) * mm});
            skLineSegment(sketch, "E281.left", {"start": v(342.86, 762) * mm, "end": v(342.86, 736.6) * mm});
            skLineSegment(sketch, "E281.right", {"start": v(377.84, 762) * mm, "end": v(377.84, 736.6) * mm});
            skLineSegment(sketch, "E282.bottom", {"start": v(342.86, 736.6) * mm, "end": v(374.65, 736.6) * mm});
            skLineSegment(sketch, "E282.top", {"start": v(342.86, 711.2) * mm, "end": v(374.65, 711.2) * mm});
            skLineSegment(sketch, "E282.left", {"start": v(342.86, 736.6) * mm, "end": v(342.86, 711.2) * mm});
            skLineSegment(sketch, "E282.right", {"start": v(374.65, 736.6) * mm, "end": v(374.65, 711.2) * mm});
            skLineSegment(sketch, "E283.top", {"start": v(342.86, 685.8) * mm, "end": v(374.65, 685.8) * mm});
            skLineSegment(sketch, "E283.left", {"start": v(342.86, 711.2) * mm, "end": v(342.86, 685.8) * mm});
            skLineSegment(sketch, "E283.right", {"start": v(374.65, 711.2) * mm, "end": v(374.65, 685.8) * mm});
            skLineSegment(sketch, "E284.top", {"start": v(342.86, 660.4) * mm, "end": v(374.65, 660.4) * mm});
            skLineSegment(sketch, "E284.left", {"start": v(342.86, 685.8) * mm, "end": v(342.86, 660.4) * mm});
            skLineSegment(sketch, "E284.right", {"start": v(374.65, 685.8) * mm, "end": v(374.65, 660.4) * mm});
            skLineSegment(sketch, "E285.top", {"start": v(342.86, 635) * mm, "end": v(374.65, 635) * mm});
            skLineSegment(sketch, "E285.left", {"start": v(342.86, 660.4) * mm, "end": v(342.86, 635) * mm});
            skLineSegment(sketch, "E285.right", {"start": v(374.65, 660.4) * mm, "end": v(374.65, 635) * mm});
            skLineSegment(sketch, "E286.top", {"start": v(342.86, 609.6) * mm, "end": v(374.65, 609.6) * mm});
            skLineSegment(sketch, "E286.left", {"start": v(342.86, 635) * mm, "end": v(342.86, 609.6) * mm});
            skLineSegment(sketch, "E286.right", {"start": v(374.65, 635) * mm, "end": v(374.65, 609.6) * mm});
            skCircle(sketch, "E287", {"center": v(358.76, 774.7) * mm, "radius": 3.81 * mm});
            skCircle(sketch, "E288", {"center": v(358.76, 749.3) * mm, "radius": 3.81 * mm});
            skCircle(sketch, "E289", {"center": v(358.76, 723.9) * mm, "radius": 3.81 * mm});
            skCircle(sketch, "E290", {"center": v(358.76, 698.5) * mm, "radius": 3.81 * mm});
            skCircle(sketch, "E291", {"center": v(358.76, 673.1) * mm, "radius": 3.81 * mm});
            skCircle(sketch, "E292", {"center": v(358.76, 647.7) * mm, "radius": 3.81 * mm});
            skCircle(sketch, "E293", {"center": v(358.76, 622.3) * mm, "radius": 3.81 * mm});
            skLineSegment(sketch, "E294.top", {"start": v(342.86, 584.2) * mm, "end": v(374.65, 584.2) * mm});
            skLineSegment(sketch, "E294.left", {"start": v(342.86, 609.6) * mm, "end": v(342.86, 584.2) * mm});
            skLineSegment(sketch, "E294.right", {"start": v(374.65, 609.6) * mm, "end": v(374.65, 584.2) * mm});
            skCircle(sketch, "E295", {"center": v(358.76, 596.9) * mm, "radius": 3.81 * mm});
            skCircle(sketch, "E296", {"center": v(358.78, 571.5) * mm, "radius": 3.81 * mm});
            skSolve(sketch);
        }
        {
            var Q0;
            Q0=makeQuery(id+"F33.imprint","IMPRINT",FACE,{"disambiguationData":[TD([[makeQuery(id+"F33.imprint","IMPRINT",EDGE,{"derivedFrom":sQuery(id+"F33.wireOp",EDGE,"E296")}),1.0]])]});
            var Q1;
            Q1=makeQuery(id+"F33.imprint","IMPRINT",FACE,{"disambiguationData":[TD([[makeQuery(id+"F33.imprint","IMPRINT",EDGE,{"derivedFrom":sQuery(id+"F33.wireOp",EDGE,"E295")}),1.0]])]});
            var Q2;
            Q2=makeQuery(id+"F33.imprint","IMPRINT",FACE,{"disambiguationData":[TD([[makeQuery(id+"F33.imprint","IMPRINT",EDGE,{"derivedFrom":sQuery(id+"F33.wireOp",EDGE,"E293")}),1.0]])]});
            var Q3;
            Q3=makeQuery(id+"F33.imprint","IMPRINT",FACE,{"disambiguationData":[TD([[makeQuery(id+"F33.imprint","IMPRINT",EDGE,{"derivedFrom":sQuery(id+"F33.wireOp",EDGE,"E292")}),1.0]])]});
            var Q4;
            Q4=makeQuery(id+"F33.imprint","IMPRINT",FACE,{"disambiguationData":[TD([[makeQuery(id+"F33.imprint","IMPRINT",EDGE,{"derivedFrom":sQuery(id+"F33.wireOp",EDGE,"E291")}),1.0]])]});
            var Q5;
            Q5=makeQuery(id+"F33.imprint","IMPRINT",FACE,{"disambiguationData":[TD([[makeQuery(id+"F33.imprint","IMPRINT",EDGE,{"derivedFrom":sQuery(id+"F33.wireOp",EDGE,"E290")}),1.0]])]});
            var Q6;
            Q6=makeQuery(id+"F33.imprint","IMPRINT",FACE,{"disambiguationData":[TD([[makeQuery(id+"F33.imprint","IMPRINT",EDGE,{"derivedFrom":sQuery(id+"F33.wireOp",EDGE,"E289")}),1.0]])]});
            var Q7;
            Q7=makeQuery(id+"F33.imprint","IMPRINT",FACE,{"disambiguationData":[TD([[makeQuery(id+"F33.imprint","IMPRINT",EDGE,{"derivedFrom":sQuery(id+"F33.wireOp",EDGE,"E288")}),1.0]])]});
            var Q8;
            Q8=makeQuery(id+"F33.imprint","IMPRINT",FACE,{"disambiguationData":[TD([[makeQuery(id+"F33.imprint","IMPRINT",EDGE,{"derivedFrom":sQuery(id+"F33.wireOp",EDGE,"E287")}),1.0]])]});
            var Q9;
            Q9=makeQuery(id+"F33.imprint","IMPRINT",FACE,{"disambiguationData":[TD([[makeQuery(id+"F33.imprint","IMPRINT",EDGE,{"derivedFrom":sQuery(id+"F33.wireOp",EDGE,"E279")}),1.0]])]});
            var Q10;
            Q10=makeQuery(id+"F33.imprint","IMPRINT",FACE,{"disambiguationData":[TD([[makeQuery(id+"F33.imprint","IMPRINT",EDGE,{"derivedFrom":sQuery(id+"F33.wireOp",EDGE,"E278")}),1.0]])]});
            var Q11;
            Q11=makeQuery(id+"F33.imprint","IMPRINT",FACE,{"disambiguationData":[TD([[makeQuery(id+"F33.imprint","IMPRINT",EDGE,{"derivedFrom":sQuery(id+"F33.wireOp",EDGE,"E277")}),1.0]])]});
            var Q12;
            Q12=makeQuery(id+"F33.imprint","IMPRINT",FACE,{"disambiguationData":[TD([[makeQuery(id+"F33.imprint","IMPRINT",EDGE,{"derivedFrom":sQuery(id+"F33.wireOp",EDGE,"E276")}),1.0]])]});
            var Q13;
            Q13=makeQuery(id+"F33.imprint","IMPRINT",FACE,{"disambiguationData":[TD([[makeQuery(id+"F33.imprint","IMPRINT",EDGE,{"derivedFrom":sQuery(id+"F33.wireOp",EDGE,"E275")}),1.0]])]});
            var Q14;
            Q14=makeQuery(id+"F33.imprint","IMPRINT",FACE,{"disambiguationData":[TD([[makeQuery(id+"F33.imprint","IMPRINT",EDGE,{"derivedFrom":sQuery(id+"F33.wireOp",EDGE,"E266")}),1.0]])]});
            var Q15;
            Q15=makeQuery(id+"F33.imprint","IMPRINT",FACE,{"disambiguationData":[TD([[makeQuery(id+"F33.imprint","IMPRINT",EDGE,{"derivedFrom":sQuery(id+"F33.wireOp",EDGE,"E267")}),1.0]])]});
            var Q16;
            Q16=makeQuery(id+"F33.imprint","IMPRINT",FACE,{"disambiguationData":[TD([[makeQuery(id+"F33.imprint","IMPRINT",EDGE,{"derivedFrom":sQuery(id+"F33.wireOp",EDGE,"E268")}),1.0]])]});
            var Q17;
            Q17=makeQuery(id+"F33.imprint","IMPRINT",FACE,{"disambiguationData":[TD([[makeQuery(id+"F33.imprint","IMPRINT",EDGE,{"derivedFrom":sQuery(id+"F33.wireOp",EDGE,"E269")}),1.0]])]});
            extrude(context, id + "F34", {"entities" : qUnion([Q0, Q1, Q2, Q3, Q4, Q5, Q6, Q7, Q8, Q9, Q10, Q11, Q12, Q13, Q14, Q15, Q16, Q17]), "operationType" : NewBodyOperationType.REMOVE, "oppositeDirection" : true, "depth" : 25.4 * mm, "offsetDistance" : 25.4 * mm});
        }
        {
            var Q0;
            Q0=makeQuery(id+"F10.opExtrude","SWEPT_FACE",FACE,{"disambiguationData":[OSD([sQuery(id+"F8.wireOp",EDGE,"E25.bottom")])]});
            var sketch = newSketch(context, id + "F35", { "sketchPlane" : qUnion([Q0])});
            skLineSegment(sketch, "E297.bottom", {"start": v(-374.65, 1016) * mm, "end": v(-342.9, 1016) * mm});
            skLineSegment(sketch, "E297.top", {"start": v(-374.65, 990.6) * mm, "end": v(-342.9, 990.6) * mm});
            skLineSegment(sketch, "E297.left", {"start": v(-374.65, 1016) * mm, "end": v(-374.65, 990.6) * mm});
            skLineSegment(sketch, "E297.right", {"start": v(-342.9, 1016) * mm, "end": v(-342.9, 990.6) * mm});
            skLineSegment(sketch, "E298.top", {"start": v(-374.65, 965.2) * mm, "end": v(-342.9, 965.2) * mm});
            skLineSegment(sketch, "E298.left", {"start": v(-374.65, 990.6) * mm, "end": v(-374.65, 965.2) * mm});
            skLineSegment(sketch, "E298.right", {"start": v(-342.9, 990.6) * mm, "end": v(-342.9, 965.2) * mm});
            skLineSegment(sketch, "E299.top", {"start": v(-374.65, 939.8) * mm, "end": v(-342.9, 939.8) * mm});
            skLineSegment(sketch, "E299.left", {"start": v(-374.65, 965.2) * mm, "end": v(-374.65, 939.8) * mm});
            skLineSegment(sketch, "E299.right", {"start": v(-342.9, 965.2) * mm, "end": v(-342.9, 939.8) * mm});
            skLineSegment(sketch, "E300.top", {"start": v(-374.65, 914.4) * mm, "end": v(-342.9, 914.4) * mm});
            skLineSegment(sketch, "E300.left", {"start": v(-374.65, 939.8) * mm, "end": v(-374.65, 914.4) * mm});
            skLineSegment(sketch, "E300.right", {"start": v(-342.9, 939.8) * mm, "end": v(-342.9, 914.4) * mm});
            skLineSegment(sketch, "E301.top", {"start": v(-374.65, 889) * mm, "end": v(-342.9, 889) * mm});
            skLineSegment(sketch, "E301.left", {"start": v(-374.65, 914.4) * mm, "end": v(-374.65, 889) * mm});
            skLineSegment(sketch, "E301.right", {"start": v(-342.9, 914.4) * mm, "end": v(-342.9, 889) * mm});
            skLineSegment(sketch, "E302.top", {"start": v(-374.65, 863.6) * mm, "end": v(-342.9, 863.6) * mm});
            skLineSegment(sketch, "E302.left", {"start": v(-374.65, 889) * mm, "end": v(-374.65, 863.6) * mm});
            skLineSegment(sketch, "E302.right", {"start": v(-342.9, 889) * mm, "end": v(-342.9, 863.6) * mm});
            skLineSegment(sketch, "E303.top", {"start": v(-374.65, 838.2) * mm, "end": v(-342.9, 838.2) * mm});
            skLineSegment(sketch, "E303.left", {"start": v(-374.65, 863.6) * mm, "end": v(-374.65, 838.2) * mm});
            skLineSegment(sketch, "E303.right", {"start": v(-342.9, 863.6) * mm, "end": v(-342.9, 838.2) * mm});
            skLineSegment(sketch, "E304.top", {"start": v(-374.65, 812.8) * mm, "end": v(-342.9, 812.8) * mm});
            skLineSegment(sketch, "E304.left", {"start": v(-374.65, 838.2) * mm, "end": v(-374.65, 812.8) * mm});
            skLineSegment(sketch, "E304.right", {"start": v(-342.9, 838.2) * mm, "end": v(-342.9, 812.8) * mm});
            skLineSegment(sketch, "E305.top", {"start": v(-374.65, 787.4) * mm, "end": v(-342.9, 787.4) * mm});
            skLineSegment(sketch, "E305.left", {"start": v(-374.65, 812.8) * mm, "end": v(-374.65, 787.4) * mm});
            skLineSegment(sketch, "E305.right", {"start": v(-342.9, 812.8) * mm, "end": v(-342.9, 787.4) * mm});
            skLineSegment(sketch, "E306.top", {"start": v(-374.65, 762) * mm, "end": v(-342.9, 762) * mm});
            skLineSegment(sketch, "E306.left", {"start": v(-374.65, 787.4) * mm, "end": v(-374.65, 762) * mm});
            skLineSegment(sketch, "E306.right", {"start": v(-342.9, 787.4) * mm, "end": v(-342.9, 762) * mm});
            skLineSegment(sketch, "E307.top", {"start": v(-374.65, 736.6) * mm, "end": v(-342.9, 736.6) * mm});
            skLineSegment(sketch, "E307.left", {"start": v(-374.65, 762) * mm, "end": v(-374.65, 736.6) * mm});
            skLineSegment(sketch, "E307.right", {"start": v(-342.9, 762) * mm, "end": v(-342.9, 736.6) * mm});
            skLineSegment(sketch, "E308.top", {"start": v(-374.65, 711.2) * mm, "end": v(-342.9, 711.2) * mm});
            skLineSegment(sketch, "E308.left", {"start": v(-374.65, 736.6) * mm, "end": v(-374.65, 711.2) * mm});
            skLineSegment(sketch, "E308.right", {"start": v(-342.9, 736.6) * mm, "end": v(-342.9, 711.2) * mm});
            skLineSegment(sketch, "E309.top", {"start": v(-374.65, 685.8) * mm, "end": v(-342.9, 685.8) * mm});
            skLineSegment(sketch, "E309.left", {"start": v(-374.65, 711.2) * mm, "end": v(-374.65, 685.8) * mm});
            skLineSegment(sketch, "E309.right", {"start": v(-342.9, 711.2) * mm, "end": v(-342.9, 685.8) * mm});
            skLineSegment(sketch, "E310.top", {"start": v(-374.65, 660.4) * mm, "end": v(-342.9, 660.4) * mm});
            skLineSegment(sketch, "E310.left", {"start": v(-374.65, 685.8) * mm, "end": v(-374.65, 660.4) * mm});
            skLineSegment(sketch, "E310.right", {"start": v(-342.9, 685.8) * mm, "end": v(-342.9, 660.4) * mm});
            skLineSegment(sketch, "E311.top", {"start": v(-374.65, 635) * mm, "end": v(-342.9, 635) * mm});
            skLineSegment(sketch, "E311.left", {"start": v(-374.65, 660.4) * mm, "end": v(-374.65, 635) * mm});
            skLineSegment(sketch, "E311.right", {"start": v(-342.9, 660.4) * mm, "end": v(-342.9, 635) * mm});
            skLineSegment(sketch, "E312.top", {"start": v(-374.65, 609.6) * mm, "end": v(-342.9, 609.6) * mm});
            skLineSegment(sketch, "E312.left", {"start": v(-374.65, 635) * mm, "end": v(-374.65, 609.6) * mm});
            skLineSegment(sketch, "E312.right", {"start": v(-342.9, 635) * mm, "end": v(-342.9, 609.6) * mm});
            skLineSegment(sketch, "E313.top", {"start": v(-374.65, 584.2) * mm, "end": v(-342.9, 584.2) * mm});
            skLineSegment(sketch, "E313.left", {"start": v(-374.65, 609.6) * mm, "end": v(-374.65, 584.2) * mm});
            skLineSegment(sketch, "E313.right", {"start": v(-342.9, 609.6) * mm, "end": v(-342.9, 584.2) * mm});
            skCircle(sketch, "E314", {"center": v(-358.78, 571.5) * mm, "radius": 3.81 * mm});
            skCircle(sketch, "E315", {"center": v(-358.78, 596.9) * mm, "radius": 3.81 * mm});
            skCircle(sketch, "E316", {"center": v(-358.77, 622.3) * mm, "radius": 3.81 * mm});
            skCircle(sketch, "E317", {"center": v(-358.78, 647.7) * mm, "radius": 3.81 * mm});
            skCircle(sketch, "E318", {"center": v(-358.77, 673.1) * mm, "radius": 3.81 * mm});
            skCircle(sketch, "E319", {"center": v(-358.77, 698.5) * mm, "radius": 3.81 * mm});
            skCircle(sketch, "E320", {"center": v(-358.77, 723.9) * mm, "radius": 3.81 * mm});
            skCircle(sketch, "E321", {"center": v(-358.78, 749.3) * mm, "radius": 3.81 * mm});
            skCircle(sketch, "E322", {"center": v(-358.78, 774.7) * mm, "radius": 3.81 * mm});
            skCircle(sketch, "E323", {"center": v(-358.78, 800.1) * mm, "radius": 3.8 * mm});
            skCircle(sketch, "E324", {"center": v(-358.78, 825.5) * mm, "radius": 3.81 * mm});
            skCircle(sketch, "E325", {"center": v(-358.77, 850.9) * mm, "radius": 3.81 * mm});
            skCircle(sketch, "E326", {"center": v(-358.77, 876.3) * mm, "radius": 3.81 * mm});
            skCircle(sketch, "E327", {"center": v(-358.78, 901.7) * mm, "radius": 3.81 * mm});
            skCircle(sketch, "E328", {"center": v(-358.78, 927.1) * mm, "radius": 3.81 * mm});
            skCircle(sketch, "E329", {"center": v(-358.77, 952.5) * mm, "radius": 3.8 * mm});
            skCircle(sketch, "E330", {"center": v(-358.78, 977.9) * mm, "radius": 3.81 * mm});
            skCircle(sketch, "E331", {"center": v(-358.77, 1003.3) * mm, "radius": 3.81 * mm});
            skSolve(sketch);
        }
        {
            var Q0;
            Q0=makeQuery(id+"F35.imprint","IMPRINT",FACE,{"disambiguationData":[TD([[makeQuery(id+"F35.imprint","IMPRINT",EDGE,{"derivedFrom":sQuery(id+"F35.wireOp",EDGE,"E314")}),1.0]])]});
            var Q1;
            Q1=makeQuery(id+"F35.imprint","IMPRINT",FACE,{"disambiguationData":[TD([[makeQuery(id+"F35.imprint","IMPRINT",EDGE,{"derivedFrom":sQuery(id+"F35.wireOp",EDGE,"E315")}),1.0]])]});
            var Q2;
            Q2=makeQuery(id+"F35.imprint","IMPRINT",FACE,{"disambiguationData":[TD([[makeQuery(id+"F35.imprint","IMPRINT",EDGE,{"derivedFrom":sQuery(id+"F35.wireOp",EDGE,"E316")}),1.0]])]});
            var Q3;
            Q3=makeQuery(id+"F35.imprint","IMPRINT",FACE,{"disambiguationData":[TD([[makeQuery(id+"F35.imprint","IMPRINT",EDGE,{"derivedFrom":sQuery(id+"F35.wireOp",EDGE,"E317")}),1.0]])]});
            var Q4;
            Q4=makeQuery(id+"F35.imprint","IMPRINT",FACE,{"disambiguationData":[TD([[makeQuery(id+"F35.imprint","IMPRINT",EDGE,{"derivedFrom":sQuery(id+"F35.wireOp",EDGE,"E318")}),1.0]])]});
            var Q5;
            Q5=makeQuery(id+"F35.imprint","IMPRINT",FACE,{"disambiguationData":[TD([[makeQuery(id+"F35.imprint","IMPRINT",EDGE,{"derivedFrom":sQuery(id+"F35.wireOp",EDGE,"E319")}),1.0]])]});
            var Q6;
            Q6=makeQuery(id+"F35.imprint","IMPRINT",FACE,{"disambiguationData":[TD([[makeQuery(id+"F35.imprint","IMPRINT",EDGE,{"derivedFrom":sQuery(id+"F35.wireOp",EDGE,"E320")}),1.0]])]});
            var Q7;
            Q7=makeQuery(id+"F35.imprint","IMPRINT",FACE,{"disambiguationData":[TD([[makeQuery(id+"F35.imprint","IMPRINT",EDGE,{"derivedFrom":sQuery(id+"F35.wireOp",EDGE,"E321")}),1.0]])]});
            var Q8;
            Q8=makeQuery(id+"F35.imprint","IMPRINT",FACE,{"disambiguationData":[TD([[makeQuery(id+"F35.imprint","IMPRINT",EDGE,{"derivedFrom":sQuery(id+"F35.wireOp",EDGE,"E322")}),1.0]])]});
            var Q9;
            Q9=makeQuery(id+"F35.imprint","IMPRINT",FACE,{"disambiguationData":[TD([[makeQuery(id+"F35.imprint","IMPRINT",EDGE,{"derivedFrom":sQuery(id+"F35.wireOp",EDGE,"E323")}),1.0]])]});
            var Q10;
            Q10=makeQuery(id+"F35.imprint","IMPRINT",FACE,{"disambiguationData":[TD([[makeQuery(id+"F35.imprint","IMPRINT",EDGE,{"derivedFrom":sQuery(id+"F35.wireOp",EDGE,"E324")}),1.0]])]});
            var Q11;
            Q11=makeQuery(id+"F35.imprint","IMPRINT",FACE,{"disambiguationData":[TD([[makeQuery(id+"F35.imprint","IMPRINT",EDGE,{"derivedFrom":sQuery(id+"F35.wireOp",EDGE,"E325")}),1.0]])]});
            var Q12;
            Q12=makeQuery(id+"F35.imprint","IMPRINT",FACE,{"disambiguationData":[TD([[makeQuery(id+"F35.imprint","IMPRINT",EDGE,{"derivedFrom":sQuery(id+"F35.wireOp",EDGE,"E326")}),1.0]])]});
            var Q13;
            Q13=makeQuery(id+"F35.imprint","IMPRINT",FACE,{"disambiguationData":[TD([[makeQuery(id+"F35.imprint","IMPRINT",EDGE,{"derivedFrom":sQuery(id+"F35.wireOp",EDGE,"E327")}),1.0]])]});
            var Q14;
            Q14=makeQuery(id+"F35.imprint","IMPRINT",FACE,{"disambiguationData":[TD([[makeQuery(id+"F35.imprint","IMPRINT",EDGE,{"derivedFrom":sQuery(id+"F35.wireOp",EDGE,"E328")}),1.0]])]});
            var Q15;
            Q15=makeQuery(id+"F35.imprint","IMPRINT",FACE,{"disambiguationData":[TD([[makeQuery(id+"F35.imprint","IMPRINT",EDGE,{"derivedFrom":sQuery(id+"F35.wireOp",EDGE,"E329")}),1.0]])]});
            var Q16;
            Q16=makeQuery(id+"F35.imprint","IMPRINT",FACE,{"disambiguationData":[TD([[makeQuery(id+"F35.imprint","IMPRINT",EDGE,{"derivedFrom":sQuery(id+"F35.wireOp",EDGE,"E330")}),1.0]])]});
            var Q17;
            Q17=makeQuery(id+"F35.imprint","IMPRINT",FACE,{"disambiguationData":[TD([[makeQuery(id+"F35.imprint","IMPRINT",EDGE,{"derivedFrom":sQuery(id+"F35.wireOp",EDGE,"E331")}),1.0]])]});
            extrude(context, id + "F36", {"entities" : qUnion([Q0, Q1, Q2, Q3, Q4, Q5, Q6, Q7, Q8, Q9, Q10, Q11, Q12, Q13, Q14, Q15, Q16, Q17]), "operationType" : NewBodyOperationType.REMOVE, "oppositeDirection" : true, "depth" : 25.4 * mm, "offsetDistance" : 25.4 * mm});
        }
        {
            var Q0;
            {var subQ0=sQuery(id+"F2.wireOp",EDGE,"E5.top");var subQ1=makeQuery(id+"F2.imprint","INTERSECT",VERTEX,{"derivedFrom":[sQuery(id+"F2.wireOp",EDGE,"E1.right"),subQ0]});Q0=makeQuery(id+"F5.boolean.opBoolean","MERGE",FACE,{"derivedFrom":[makeQuery(id+"F3.opExtrude","SWEPT_FACE",FACE,{"disambiguationData":[OSD([subQ0]),TDD([makeQuery(id+"F2.imprint","IMPRINT",EDGE,{"disambiguationData":[TD([[subQ1,1.0]])],"derivedFrom":subQ0})])]}),makeQuery(id+"F5.opExtrude","SWEPT_FACE",FACE,{"disambiguationData":[OSD([subQ0]),TDD([makeQuery(id+"F2.imprint","IMPRINT",EDGE,{"disambiguationData":[TD([[makeQuery(id+"F2.imprint","INTERSECT",VERTEX,{"derivedFrom":[subQ0,sQuery(id+"F2.wireOp",EDGE,"E6.right")]}),1.0]])],"derivedFrom":subQ0})])]})]});}
            var sketch = newSketch(context, id + "F37", { "sketchPlane" : qUnion([Q0])});
            skLineSegment(sketch, "E332.bottom", {"start": v(381, 558.8) * mm, "end": v(342.9, 558.8) * mm});
            skLineSegment(sketch, "E332.top", {"start": v(381, 482.6) * mm, "end": v(342.9, 482.6) * mm});
            skLineSegment(sketch, "E332.left", {"start": v(381, 558.8) * mm, "end": v(381, 482.6) * mm});
            skLineSegment(sketch, "E332.right", {"start": v(342.9, 558.8) * mm, "end": v(342.9, 482.6) * mm});
            skLineSegment(sketch, "E333.bottom", {"start": v(381, 482.6) * mm, "end": v(-381, 482.6) * mm});
            skLineSegment(sketch, "E333.top", {"start": v(381, 558.8) * mm, "end": v(-381, 558.8) * mm});
            skLineSegment(sketch, "E333.left", {"start": v(381, 482.6) * mm, "end": v(381, 558.8) * mm});
            skLineSegment(sketch, "E333.right", {"start": v(-381, 482.6) * mm, "end": v(-381, 558.8) * mm});
            skLineSegment(sketch, "E334.top", {"start": v(381, 457.2) * mm, "end": v(-381, 457.2) * mm});
            skLineSegment(sketch, "E334.left", {"start": v(381, 482.6) * mm, "end": v(381, 457.2) * mm});
            skLineSegment(sketch, "E334.right", {"start": v(-381, 482.6) * mm, "end": v(-381, 457.2) * mm});
            skLineSegment(sketch, "E335.bottom", {"start": v(381, 558.8) * mm, "end": v(457.2, 558.8) * mm});
            skLineSegment(sketch, "E335.top", {"start": v(381, 482.6) * mm, "end": v(457.2, 482.6) * mm});
            skLineSegment(sketch, "E335.right", {"start": v(457.2, 558.8) * mm, "end": v(457.2, 482.6) * mm});
            skLineSegment(sketch, "E336.bottom", {"start": v(-381, 457.2) * mm, "end": v(-457.2, 457.2) * mm});
            skLineSegment(sketch, "E336.top", {"start": v(-381, 558.8) * mm, "end": v(-457.2, 558.8) * mm});
            skLineSegment(sketch, "E336.left", {"start": v(-381, 457.2) * mm, "end": v(-381, 558.8) * mm});
            skLineSegment(sketch, "E336.right", {"start": v(-457.2, 457.2) * mm, "end": v(-457.2, 558.8) * mm});
            skLineSegment(sketch, "E337.bottom", {"start": v(-457.2, 457.2) * mm, "end": v(457.2, 457.2) * mm});
            skLineSegment(sketch, "E337.top", {"start": v(-457.2, 482.6) * mm, "end": v(457.2, 482.6) * mm});
            skLineSegment(sketch, "E337.left", {"start": v(-457.2, 457.2) * mm, "end": v(-457.2, 482.6) * mm});
            skLineSegment(sketch, "E337.right", {"start": v(457.2, 457.2) * mm, "end": v(457.2, 482.6) * mm});
            skSolve(sketch);
        }
        {
            var Q0;
            Q0=makeQuery(id+"F37.imprint","IMPRINT",FACE,{"disambiguationData":[TD([[makeQuery(id+"F37.imprint","IMPRINT",EDGE,{"derivedFrom":sQuery(id+"F37.wireOp",EDGE,"E332.right")}),-1.0]])]});
            var Q1;
            Q1=makeQuery(id+"F37.imprint","IMPRINT",FACE,{"disambiguationData":[TD([[makeQuery(id+"F37.imprint","IMPRINT",EDGE,{"derivedFrom":sQuery(id+"F37.wireOp",EDGE,"E332.bottom")}),1.0]])]});
            extrude(context, id + "F38", {"entities" : qUnion([Q0, Q1]), "operationType" : NewBodyOperationType.ADD, "depth" : 12.7 * mm, "offsetDistance" : 25.4 * mm});
        }
        {
            var Q0;
            Q0=makeQuery(id+"F37.imprint","IMPRINT",FACE,{"disambiguationData":[TD([[makeQuery(id+"F37.imprint","IMPRINT",EDGE,{"derivedFrom":sQuery(id+"F37.wireOp",EDGE,"E334.left")}),1.0]])]});
            var Q1;
            {var subQ5=sQuery(id+"F37.wireOp",EDGE,"E332.top");Q1=makeQuery(id+"F37.imprint","IMPRINT",FACE,{"disambiguationData":[TD([[makeQuery(id+"F37.imprint","IMPRINT",EDGE,{"derivedFrom":subQ5}),1.0]])]});}
            var Q2;
            {var subQ0=sQuery(id+"F37.wireOp",EDGE,"E333.bottom");Q2=makeQuery(id+"F37.imprint","IMPRINT",FACE,{"disambiguationData":[TD([[makeQuery(id+"F37.imprint","IMPRINT",EDGE,{"derivedFrom":subQ0}),1.0]])]});}
            var Q3;
            Q3=makeQuery(id+"F37.imprint","IMPRINT",FACE,{"disambiguationData":[TD([[makeQuery(id+"F37.imprint","IMPRINT",EDGE,{"derivedFrom":sQuery(id+"F37.wireOp",EDGE,"E334.right")}),-1.0]])]});
            var Q4;
            Q4=makeQuery(id+"F37.imprint","IMPRINT",FACE,{"disambiguationData":[TD([[makeQuery(id+"F37.imprint","IMPRINT",EDGE,{"derivedFrom":makeQuery(id+"F32.boolean.opBoolean","COPY",EDGE,{"derivedFrom":makeQuery(id+"F32.opExtrude","CAP_EDGE",EDGE,{"disambiguationData":[OSD([sQuery(id+"F31.wireOp",EDGE,"E228")])],"isStart":true})})}),1.0]])]});
            extrude(context, id + "F39", {"entities" : qUnion([Q0, Q1, Q2, Q3, Q4]), "operationType" : NewBodyOperationType.ADD, "depth" : 304.8 * mm, "offsetDistance" : 25.4 * mm});
        }
        {
            var Q0;
            Q0=makeQuery(id+"F39.opExtrude","SWEPT_FACE",FACE,{"disambiguationData":[OSD([sQuery(id+"F37.wireOp",EDGE,"E332.top"),sQuery(id+"F37.wireOp",EDGE,"E333.bottom"),sQuery(id+"F37.wireOp",EDGE,"E335.top"),sQuery(id+"F37.wireOp",EDGE,"E337.top")])]});
            var sketch = newSketch(context, id + "F40", { "sketchPlane" : qUnion([Q0])});
            skLineSegment(sketch, "E338.bottom", {"start": v(-457.2, 431.8) * mm, "end": v(-419.1, 431.8) * mm});
            skLineSegment(sketch, "E338.top", {"start": v(-457.2, 127) * mm, "end": v(-419.1, 127) * mm});
            skLineSegment(sketch, "E338.left", {"start": v(-457.2, 431.8) * mm, "end": v(-457.2, 127) * mm});
            skLineSegment(sketch, "E338.right", {"start": v(-419.1, 431.8) * mm, "end": v(-419.1, 127) * mm});
            skLineSegment(sketch, "E339.bottom", {"start": v(-419.1, 431.8) * mm, "end": v(-381, 431.8) * mm});
            skLineSegment(sketch, "E339.top", {"start": v(-419.1, 127) * mm, "end": v(-381, 127) * mm});
            skLineSegment(sketch, "E339.right", {"start": v(-381, 431.8) * mm, "end": v(-381, 127) * mm});
            skLineSegment(sketch, "E340.bottom", {"start": v(457.2, 431.8) * mm, "end": v(419.1, 431.8) * mm});
            skLineSegment(sketch, "E340.top", {"start": v(457.2, 127) * mm, "end": v(419.1, 127) * mm});
            skLineSegment(sketch, "E340.left", {"start": v(457.2, 431.8) * mm, "end": v(457.2, 127) * mm});
            skLineSegment(sketch, "E340.right", {"start": v(419.1, 431.8) * mm, "end": v(419.1, 127) * mm});
            skLineSegment(sketch, "E341.bottom", {"start": v(419.1, 431.8) * mm, "end": v(381, 431.8) * mm});
            skLineSegment(sketch, "E341.top", {"start": v(419.1, 127) * mm, "end": v(381, 127) * mm});
            skLineSegment(sketch, "E341.right", {"start": v(381, 431.8) * mm, "end": v(381, 127) * mm});
            skSolve(sketch);
        }
        {
            var Q0;
            {var subQ3=sQuery(id+"F40.wireOp",EDGE,"E341.bottom");Q0=makeQuery(id+"F40.imprint","IMPRINT",FACE,{"disambiguationData":[TD([[makeQuery(id+"F40.imprint","IMPRINT",EDGE,{"derivedFrom":subQ3}),1.0]])]});}
            var Q1;
            {var subQ3=sQuery(id+"F40.wireOp",EDGE,"E339.bottom");Q1=makeQuery(id+"F40.imprint","IMPRINT",FACE,{"disambiguationData":[TD([[makeQuery(id+"F40.imprint","IMPRINT",EDGE,{"derivedFrom":subQ3}),1.0]])]});}
            extrude(context, id + "F41", {"entities" : qUnion([Q0, Q1]), "operationType" : NewBodyOperationType.ADD, "depth" : 50.8 * mm, "offsetDistance" : 25.4 * mm});
        }
        {
            var Q0;
            Q0=makeQuery(id+"F38.opExtrude","CAP_FACE",FACE,{"disambiguationData":[OSD([sQuery(id+"F31.wireOp",EDGE,"E225"),sQuery(id+"F31.wireOp",EDGE,"E226"),sQuery(id+"F31.wireOp",EDGE,"E227"),sQuery(id+"F37.wireOp",EDGE,"E332.bottom"),sQuery(id+"F37.wireOp",EDGE,"E332.top"),sQuery(id+"F37.wireOp",EDGE,"E332.left"),sQuery(id+"F37.wireOp",EDGE,"E333.bottom"),sQuery(id+"F37.wireOp",EDGE,"E333.top"),sQuery(id+"F37.wireOp",EDGE,"E333.right")])],"isStart":false});
            var sketch = newSketch(context, id + "F42", { "sketchPlane" : qUnion([Q0])});
            skCircle(sketch, "E342", {"center": v(361.95, 495.3) * mm, "radius": 5.08 * mm});
            skCircle(sketch, "E343", {"center": v(361.95, 546.1) * mm, "radius": 5.08 * mm});
            skSolve(sketch);
        }
        {
            var Q0;
            Q0=makeQuery(id+"F42.imprint","IMPRINT",FACE,{"disambiguationData":[TD([[makeQuery(id+"F42.imprint","IMPRINT",EDGE,{"derivedFrom":sQuery(id+"F42.wireOp",EDGE,"E342")}),1.0]])]});
            var Q1;
            Q1=makeQuery(id+"F42.imprint","IMPRINT",FACE,{"disambiguationData":[TD([[makeQuery(id+"F42.imprint","IMPRINT",EDGE,{"derivedFrom":makeQuery(id+"F38.opExtrude","CAP_EDGE",EDGE,{"disambiguationData":[OSD([sQuery(id+"F31.wireOp",EDGE,"E227")])],"isStart":false})}),1.0]])]});
            var Q2;
            Q2=makeQuery(id+"F42.imprint","IMPRINT",FACE,{"disambiguationData":[TD([[makeQuery(id+"F42.imprint","IMPRINT",EDGE,{"derivedFrom":makeQuery(id+"F38.opExtrude","CAP_EDGE",EDGE,{"disambiguationData":[OSD([sQuery(id+"F31.wireOp",EDGE,"E225")])],"isStart":false})}),1.0]])]});
            var Q3;
            Q3=makeQuery(id+"F42.imprint","IMPRINT",FACE,{"disambiguationData":[TD([[makeQuery(id+"F42.imprint","IMPRINT",EDGE,{"derivedFrom":sQuery(id+"F42.wireOp",EDGE,"E343")}),1.0]])]});
            extrude(context, id + "F43", {"entities" : qUnion([Q0, Q1, Q2, Q3]), "operationType" : NewBodyOperationType.ADD, "depth" : 5.08 * mm, "offsetDistance" : 25.4 * mm});
        }
        {
            var Q0;
            Q0=makeQuery(id+"F38.opExtrude","CAP_FACE",FACE,{"disambiguationData":[OSD([sQuery(id+"F31.wireOp",EDGE,"E225"),sQuery(id+"F31.wireOp",EDGE,"E226"),sQuery(id+"F31.wireOp",EDGE,"E227"),sQuery(id+"F37.wireOp",EDGE,"E332.bottom"),sQuery(id+"F37.wireOp",EDGE,"E332.top"),sQuery(id+"F37.wireOp",EDGE,"E332.left"),sQuery(id+"F37.wireOp",EDGE,"E333.bottom"),sQuery(id+"F37.wireOp",EDGE,"E333.top"),sQuery(id+"F37.wireOp",EDGE,"E333.right")])],"isStart":false});
            var sketch = newSketch(context, id + "F44", { "sketchPlane" : qUnion([Q0])});
            skLineSegment(sketch, "E344.bottom", {"start": v(-381, 482.6) * mm, "end": v(-342.9, 482.6) * mm});
            skLineSegment(sketch, "E344.top", {"start": v(-381, 558.8) * mm, "end": v(-342.9, 558.8) * mm});
            skLineSegment(sketch, "E344.left", {"start": v(-381, 482.6) * mm, "end": v(-381, 558.8) * mm});
            skLineSegment(sketch, "E344.right", {"start": v(-342.9, 482.6) * mm, "end": v(-342.9, 558.8) * mm});
            skLineSegment(sketch, "E345.bottom", {"start": v(-342.9, 558.8) * mm, "end": v(-381, 558.8) * mm});
            skLineSegment(sketch, "E345.top", {"start": v(-342.9, 533.4) * mm, "end": v(-381, 533.4) * mm});
            skLineSegment(sketch, "E345.left", {"start": v(-342.9, 558.8) * mm, "end": v(-342.9, 533.4) * mm});
            skLineSegment(sketch, "E345.right", {"start": v(-381, 558.8) * mm, "end": v(-381, 533.4) * mm});
            skLineSegment(sketch, "E346.top", {"start": v(-342.9, 508) * mm, "end": v(-381, 508) * mm});
            skLineSegment(sketch, "E346.left", {"start": v(-342.9, 533.4) * mm, "end": v(-342.9, 508) * mm});
            skLineSegment(sketch, "E346.right", {"start": v(-381, 533.4) * mm, "end": v(-381, 508) * mm});
            skCircle(sketch, "E347", {"center": v(-362.29, 495.32) * mm, "radius": 5.08 * mm});
            skCircle(sketch, "E348", {"center": v(-362.29, 544.51) * mm, "radius": 5.08 * mm});
            skCircle(sketch, "E349", {"center": v(-361.95, 519.91) * mm, "radius": 3.81 * mm});
            skPoint(sketch, "E349.centerSnap0", {"position": v(-361.95, 558.8) * mm});
            skSolve(sketch);
        }
        {
            var Q0;
            Q0=makeQuery(id+"F44.imprint","IMPRINT",FACE,{"disambiguationData":[TD([[makeQuery(id+"F44.imprint","IMPRINT",EDGE,{"derivedFrom":sQuery(id+"F44.wireOp",EDGE,"E347")}),1.0]])]});
            var Q1;
            Q1=makeQuery(id+"F44.imprint","IMPRINT",FACE,{"disambiguationData":[TD([[makeQuery(id+"F44.imprint","IMPRINT",EDGE,{"derivedFrom":sQuery(id+"F44.wireOp",EDGE,"E348")}),1.0]])]});
            extrude(context, id + "F45", {"entities" : qUnion([Q0, Q1]), "operationType" : NewBodyOperationType.ADD, "depth" : 5.08 * mm, "offsetDistance" : 25.4 * mm});
        }
        {
            var Q0;
            Q0=makeQuery(id+"F44.imprint","IMPRINT",FACE,{"disambiguationData":[TD([[makeQuery(id+"F44.imprint","IMPRINT",EDGE,{"derivedFrom":sQuery(id+"F44.wireOp",EDGE,"E349")}),1.0]])]});
            extrude(context, id + "F46", {"entities" : qUnion([Q0]), "operationType" : NewBodyOperationType.REMOVE, "oppositeDirection" : true, "depth" : 12.7 * mm, "offsetDistance" : 25.4 * mm});
        }
        {
            var Q0;
            Q0=makeQuery(id+"F13.opExtrude","CAP_FACE",FACE,{"disambiguationData":[OSD([sQuery(id+"F11.wireOp",EDGE,"E29.bottom"),sQuery(id+"F11.wireOp",EDGE,"E29.top"),sQuery(id+"F11.wireOp",EDGE,"E29.left"),sQuery(id+"F11.wireOp",EDGE,"E29.right"),sQuery(id+"F11.wireOp",EDGE,"E30.top"),sQuery(id+"F11.wireOp",EDGE,"E30.left"),sQuery(id+"F11.wireOp",EDGE,"E30.right"),sQuery(id+"F11.wireOp",EDGE,"E31.bottom"),sQuery(id+"F11.wireOp",EDGE,"E31.top"),sQuery(id+"F11.wireOp",EDGE,"E31.right")])],"isStart":false});
            var sketch = newSketch(context, id + "F47", { "sketchPlane" : qUnion([Q0])});
            skLineSegment(sketch, "E350.bottom", {"start": v(-374.65, 120.65) * mm, "end": v(-342.9, 120.65) * mm});
            skLineSegment(sketch, "E350.top", {"start": v(-374.65, 57.15) * mm, "end": v(-342.9, 57.15) * mm});
            skLineSegment(sketch, "E350.left", {"start": v(-374.65, 120.65) * mm, "end": v(-374.65, 57.15) * mm});
            skLineSegment(sketch, "E350.right", {"start": v(-342.9, 120.65) * mm, "end": v(-342.9, 57.15) * mm});
            skSolve(sketch);
        }
        {
            var Q0;
            Q0 = qSketchRegion(id + "F47", true);
            extrude(context, id + "F48", {"entities" : qUnion([Q0]), "operationType" : NewBodyOperationType.ADD, "depth" : 25.4 * mm, "offsetDistance" : 25.4 * mm});
        }
        {
            var Q0;
            Q0=makeQuery(id+"F48.boolean.opBoolean","MERGE",FACE,{"derivedFrom":[makeQuery(id+"F13.opExtrude","SWEPT_FACE",FACE,{"disambiguationData":[OSD([sQuery(id+"F11.wireOp",EDGE,"E30.top"),sQuery(id+"F11.wireOp",EDGE,"E31.bottom")])]}),makeQuery(id+"F48.opExtrude","SWEPT_FACE",FACE,{"disambiguationData":[OSD([sQuery(id+"F47.wireOp",EDGE,"E350.top")])]})]});
            var sketch = newSketch(context, id + "F49", { "sketchPlane" : qUnion([Q0])});
            skLineSegment(sketch, "E351.bottom", {"start": v(-374.65, 1041.4) * mm, "end": v(-342.9, 1041.4) * mm});
            skLineSegment(sketch, "E351.top", {"start": v(-374.65, 1016) * mm, "end": v(-342.9, 1016) * mm});
            skLineSegment(sketch, "E351.left", {"start": v(-374.65, 1041.4) * mm, "end": v(-374.65, 1016) * mm});
            skLineSegment(sketch, "E351.right", {"start": v(-342.9, 1041.4) * mm, "end": v(-342.9, 1016) * mm});
            skSolve(sketch);
        }
        {
            var Q0;
            Q0 = qSketchRegion(id + "F49", true);
            extrude(context, id + "F50", {"entities" : qUnion([Q0]), "operationType" : NewBodyOperationType.ADD, "depth" : 203.2 * mm, "offsetDistance" : 25.4 * mm});
        }
        {
            var Q0;
            Q0=makeQuery(id+"F49.imprint","IMPRINT",FACE,{"disambiguationData":[TD([[makeQuery(id+"F49.imprint","IMPRINT",EDGE,{"derivedFrom":sQuery(id+"F49.wireOp",EDGE,"E351.bottom")}),-1.0]])]});
            extrude(context, id + "F51", {"entities" : qUnion([Q0]), "operationType" : NewBodyOperationType.ADD, "depth" : -330.2 * mm, "offsetDistance" : 25.4 * mm});
        }
        {
            var Q0;
            Q0=makeQuery(id+"F10.opExtrude","CAP_FACE",FACE,{"disambiguationData":[OSD([sQuery(id+"F8.wireOp",EDGE,"E25.bottom"),sQuery(id+"F8.wireOp",EDGE,"E25.top"),sQuery(id+"F8.wireOp",EDGE,"E25.left"),sQuery(id+"F8.wireOp",EDGE,"E25.right"),sQuery(id+"F8.wireOp",EDGE,"E26.top"),sQuery(id+"F8.wireOp",EDGE,"E27.right"),sQuery(id+"F8.wireOp",EDGE,"E28.top")])],"isStart":false});
            var sketch = newSketch(context, id + "F52", { "sketchPlane" : qUnion([Q0])});
            skLineSegment(sketch, "E352.bottom", {"start": v(342.9, 120.65) * mm, "end": v(374.65, 120.65) * mm});
            skLineSegment(sketch, "E352.top", {"start": v(342.9, 57.15) * mm, "end": v(374.65, 57.15) * mm});
            skLineSegment(sketch, "E352.left", {"start": v(342.9, 120.65) * mm, "end": v(342.9, 57.15) * mm});
            skLineSegment(sketch, "E352.right", {"start": v(374.65, 120.65) * mm, "end": v(374.65, 57.15) * mm});
            skSolve(sketch);
        }
        {
            var Q0;
            Q0 = qSketchRegion(id + "F52", true);
            extrude(context, id + "F53", {"entities" : qUnion([Q0]), "operationType" : NewBodyOperationType.ADD, "depth" : 25.4 * mm, "offsetDistance" : 25.4 * mm});
        }
        {
            var Q0;
            Q0=makeQuery(id+"F53.boolean.opBoolean","MERGE",FACE,{"derivedFrom":[makeQuery(id+"F10.opExtrude","SWEPT_FACE",FACE,{"disambiguationData":[OSD([sQuery(id+"F8.wireOp",EDGE,"E25.top")])]}),makeQuery(id+"F53.opExtrude","SWEPT_FACE",FACE,{"disambiguationData":[OSD([sQuery(id+"F52.wireOp",EDGE,"E352.top")])]})]});
            var sketch = newSketch(context, id + "F54", { "sketchPlane" : qUnion([Q0])});
            skLineSegment(sketch, "E353.bottom", {"start": v(374.65, 1041.4) * mm, "end": v(342.9, 1041.4) * mm});
            skLineSegment(sketch, "E353.top", {"start": v(374.65, 1016) * mm, "end": v(342.9, 1016) * mm});
            skLineSegment(sketch, "E353.left", {"start": v(374.65, 1041.4) * mm, "end": v(374.65, 1016) * mm});
            skLineSegment(sketch, "E353.right", {"start": v(342.9, 1041.4) * mm, "end": v(342.9, 1016) * mm});
            skSolve(sketch);
        }
        {
            var Q0;
            Q0=makeQuery(id+"F54.imprint","IMPRINT",FACE,{"disambiguationData":[TD([[makeQuery(id+"F54.imprint","IMPRINT",EDGE,{"derivedFrom":sQuery(id+"F54.wireOp",EDGE,"E353.bottom")}),-1.0]])]});
            extrude(context, id + "F55", {"entities" : qUnion([Q0]), "operationType" : NewBodyOperationType.ADD, "depth" : 203.2 * mm, "offsetDistance" : 25.4 * mm});
        }
        {
            var Q0;
            Q0=makeQuery(id+"F54.imprint","IMPRINT",FACE,{"disambiguationData":[TD([[makeQuery(id+"F54.imprint","IMPRINT",EDGE,{"derivedFrom":sQuery(id+"F54.wireOp",EDGE,"E353.bottom")}),-1.0]])]});
            extrude(context, id + "F56", {"entities" : qUnion([Q0]), "operationType" : NewBodyOperationType.ADD, "depth" : -330.2 * mm, "offsetDistance" : 25.4 * mm});
        }
        {
            var Q0;
            {var subQ0=sQuery(id+"F49.wireOp",EDGE,"E351.left");Q0=makeQuery(id+"F51.boolean.opBoolean","MERGE",FACE,{"derivedFrom":[makeQuery(id+"F50.boolean.opBoolean","MERGE",FACE,{"derivedFrom":[makeQuery(id+"F48.boolean.opBoolean","MERGE",FACE,{"derivedFrom":[makeQuery(id+"F13.opExtrude","SWEPT_FACE",FACE,{"disambiguationData":[OSD([sQuery(id+"F11.wireOp",EDGE,"E29.left"),sQuery(id+"F11.wireOp",EDGE,"E30.left")])]}),makeQuery(id+"F48.opExtrude","SWEPT_FACE",FACE,{"disambiguationData":[OSD([sQuery(id+"F47.wireOp",EDGE,"E350.left")])]})]}),makeQuery(id+"F50.opExtrude","SWEPT_FACE",FACE,{"disambiguationData":[OSD([subQ0])]})]}),makeQuery(id+"F51.opExtrude","SWEPT_FACE",FACE,{"disambiguationData":[OSD([subQ0])]})]});}
            var sketch = newSketch(context, id + "F57", { "sketchPlane" : qUnion([Q0])});
            skLineSegment(sketch, "E354.bottom", {"start": v(-387.35, 1016) * mm, "end": v(146.05, 1016) * mm});
            skLineSegment(sketch, "E354.top", {"start": v(-387.35, 1041.4) * mm, "end": v(146.05, 1041.4) * mm});
            skLineSegment(sketch, "E354.left", {"start": v(-387.35, 1016) * mm, "end": v(-387.35, 1041.4) * mm});
            skLineSegment(sketch, "E354.right", {"start": v(146.05, 1016) * mm, "end": v(146.05, 1041.4) * mm});
            skSolve(sketch);
        }
        {
            var Q0;
            Q0=makeQuery(id+"F57.imprint","IMPRINT",FACE,{"disambiguationData":[TD([[makeQuery(id+"F57.imprint","IMPRINT",EDGE,{"derivedFrom":sQuery(id+"F57.wireOp",EDGE,"E354.top")}),-1.0]])]});
            extrude(context, id + "F58", {"entities" : qUnion([Q0]), "operationType" : NewBodyOperationType.ADD, "depth" : 12.7 * mm, "offsetDistance" : 25.4 * mm});
        }
        {
            var Q0;
            Q0=makeQuery(id+"F57.imprint","IMPRINT",FACE,{"disambiguationData":[TD([[makeQuery(id+"F57.imprint","IMPRINT",EDGE,{"derivedFrom":sQuery(id+"F57.wireOp",EDGE,"E354.top")}),-1.0]])]});
            extrude(context, id + "F59", {"entities" : qUnion([Q0]), "operationType" : NewBodyOperationType.ADD, "depth" : -44.45 * mm, "offsetDistance" : 25.4 * mm});
        }
        {
            var Q0;
            {var subQ0=sQuery(id+"F54.wireOp",EDGE,"E353.left");Q0=makeQuery(id+"F56.boolean.opBoolean","MERGE",FACE,{"derivedFrom":[makeQuery(id+"F55.boolean.opBoolean","MERGE",FACE,{"derivedFrom":[makeQuery(id+"F53.boolean.opBoolean","MERGE",FACE,{"derivedFrom":[makeQuery(id+"F10.opExtrude","SWEPT_FACE",FACE,{"disambiguationData":[OSD([sQuery(id+"F8.wireOp",EDGE,"E25.right")])]}),makeQuery(id+"F53.opExtrude","SWEPT_FACE",FACE,{"disambiguationData":[OSD([sQuery(id+"F52.wireOp",EDGE,"E352.right")])]})]}),makeQuery(id+"F55.opExtrude","SWEPT_FACE",FACE,{"disambiguationData":[OSD([subQ0])]})]}),makeQuery(id+"F56.opExtrude","SWEPT_FACE",FACE,{"disambiguationData":[OSD([subQ0])]})]});}
            var sketch = newSketch(context, id + "F60", { "sketchPlane" : qUnion([Q0])});
            skLineSegment(sketch, "E355.bottom", {"start": v(387.35, 1016) * mm, "end": v(-146.05, 1016) * mm});
            skLineSegment(sketch, "E355.top", {"start": v(387.35, 1041.4) * mm, "end": v(-146.05, 1041.4) * mm});
            skLineSegment(sketch, "E355.left", {"start": v(387.35, 1016) * mm, "end": v(387.35, 1041.4) * mm});
            skLineSegment(sketch, "E355.right", {"start": v(-146.05, 1016) * mm, "end": v(-146.05, 1041.4) * mm});
            skSolve(sketch);
        }
        {
            var Q0;
            Q0 = qSketchRegion(id + "F60", true);
            extrude(context, id + "F61", {"entities" : qUnion([Q0]), "operationType" : NewBodyOperationType.ADD, "depth" : 12.7 * mm, "offsetDistance" : 25.4 * mm});
        }
        {
            var Q0;
            Q0=makeQuery(id+"F60.imprint","IMPRINT",FACE,{"disambiguationData":[TD([[makeQuery(id+"F60.imprint","IMPRINT",EDGE,{"derivedFrom":sQuery(id+"F60.wireOp",EDGE,"E355.top")}),1.0]])]});
            extrude(context, id + "F62", {"entities" : qUnion([Q0]), "operationType" : NewBodyOperationType.ADD, "depth" : -44.45 * mm, "offsetDistance" : 25.4 * mm});
        }
        {
            var Q0;
            Q0=makeQuery(id+"F1.opExtrude","CAP_EDGE",EDGE,{"disambiguationData":[OSD([sQuery(id+"F0.wireOp",EDGE,"E0.right")])],"isStart":true});
            fillet(context, id + "F63", {"entities" : qUnion([Q0]), "radius" : 5.08 * mm, "tangentPropagation" : true, "allowEdgeOverflow" : false});
        }
        {
            var Q0;
            Q0=makeQuery(id+"F1.opExtrude","CAP_EDGE",EDGE,{"disambiguationData":[OSD([sQuery(id+"F0.wireOp",EDGE,"E0.left")])],"isStart":true});
            fillet(context, id + "F64", {"entities" : qUnion([Q0]), "radius" : 5.08 * mm, "tangentPropagation" : true, "allowEdgeOverflow" : false});
        }
        {
            var Q0;
            Q0=makeQuery(id+"F1.opExtrude","CAP_EDGE",EDGE,{"disambiguationData":[OSD([sQuery(id+"F0.wireOp",EDGE,"E0.top")])],"isStart":true});
            var Q1;
            Q1=makeQuery(id+"F1.opExtrude","CAP_EDGE",EDGE,{"disambiguationData":[OSD([sQuery(id+"F0.wireOp",EDGE,"E0.bottom")])],"isStart":true});
            fillet(context, id + "F65", {"entities" : qUnion([Q0, Q1]), "radius" : 5.08 * mm, "tangentPropagation" : true, "allowEdgeOverflow" : false});
        }
        {
            var Q0;
            Q0=makeQuery(id+"F39.opExtrude","SWEPT_EDGE",EDGE,{"disambiguationData":[OSD([sQuery(id+"F37.wireOp",EDGE,"E337.bottom"),sQuery(id+"F37.wireOp",EDGE,"E337.right")])]});
            var Q1;
            Q1=makeQuery(id+"F39.opExtrude","CAP_EDGE",EDGE,{"disambiguationData":[OSD([sQuery(id+"F37.wireOp",EDGE,"E334.top"),sQuery(id+"F37.wireOp",EDGE,"E336.bottom"),sQuery(id+"F37.wireOp",EDGE,"E337.bottom")])],"isStart":false});
            var Q2;
            Q2=makeQuery(id+"F39.opExtrude","SWEPT_EDGE",EDGE,{"disambiguationData":[OSD([sQuery(id+"F37.wireOp",EDGE,"E336.bottom"),sQuery(id+"F37.wireOp",EDGE,"E336.right")])]});
            fillet(context, id + "F66", {"entities" : qUnion([Q0, Q1, Q2]), "radius" : 5.08 * mm, "tangentPropagation" : true, "allowEdgeOverflow" : false});
        }
        {
            var Q0;
            Q0=makeQuery(id+"F58.opExtrude","CAP_EDGE",EDGE,{"disambiguationData":[OSD([sQuery(id+"F57.wireOp",EDGE,"E354.bottom")])],"isStart":false});
            var Q1;
            Q1=makeQuery(id+"F59.opExtrude","CAP_EDGE",EDGE,{"disambiguationData":[OSD([sQuery(id+"F57.wireOp",EDGE,"E354.bottom")])],"isStart":false});
            var Q2;
            Q2=makeQuery(id+"F62.opExtrude","CAP_EDGE",EDGE,{"disambiguationData":[OSD([sQuery(id+"F60.wireOp",EDGE,"E355.bottom")])],"isStart":false});
            var Q3;
            Q3=makeQuery(id+"F61.opExtrude","CAP_EDGE",EDGE,{"disambiguationData":[OSD([sQuery(id+"F60.wireOp",EDGE,"E355.bottom")])],"isStart":false});
            fillet(context, id + "F67", {"entities" : qUnion([Q0, Q1, Q2, Q3]), "radius" : 5.08 * mm, "tangentPropagation" : true, "allowEdgeOverflow" : false});
        }
        {
            var Q0;
            {var subQ0=sQuery(id+"F60.wireOp",EDGE,"E355.left");var subQ1=sQuery(id+"F60.wireOp",EDGE,"E355.bottom");Q0=makeQuery(id+"F62.boolean.opBoolean","MERGE",EDGE,{"derivedFrom":[makeQuery(id+"F61.boolean.opBoolean","MERGE",EDGE,{"derivedFrom":[makeQuery(id+"F56.opExtrude","CAP_EDGE",EDGE,{"disambiguationData":[OSD([sQuery(id+"F54.wireOp",EDGE,"E353.top")])],"isStart":false}),makeQuery(id+"F61.opExtrude","SWEPT_EDGE",EDGE,{"disambiguationData":[OSD([subQ1,subQ0])]})]}),makeQuery(id+"F62.opExtrude","SWEPT_EDGE",EDGE,{"disambiguationData":[OSD([subQ1,subQ0])]})]});}
            var Q1;
            {var subQ0=sQuery(id+"F57.wireOp",EDGE,"E354.left");var subQ1=sQuery(id+"F57.wireOp",EDGE,"E354.bottom");Q1=makeQuery(id+"F59.boolean.opBoolean","MERGE",EDGE,{"derivedFrom":[makeQuery(id+"F58.boolean.opBoolean","MERGE",EDGE,{"derivedFrom":[makeQuery(id+"F51.opExtrude","CAP_EDGE",EDGE,{"disambiguationData":[OSD([sQuery(id+"F49.wireOp",EDGE,"E351.top")])],"isStart":false}),makeQuery(id+"F58.opExtrude","SWEPT_EDGE",EDGE,{"disambiguationData":[OSD([subQ1,subQ0])]})]}),makeQuery(id+"F59.opExtrude","SWEPT_EDGE",EDGE,{"disambiguationData":[OSD([subQ1,subQ0])]})]});}
            fillet(context, id + "F68", {"entities" : qUnion([Q0, Q1]), "radius" : 5.08 * mm, "tangentPropagation" : true, "allowEdgeOverflow" : false});
        }
        {
            var Q0;
            {var subQ0=sQuery(id+"F57.wireOp",EDGE,"E354.right");var subQ1=sQuery(id+"F57.wireOp",EDGE,"E354.bottom");Q0=makeQuery(id+"F59.boolean.opBoolean","MERGE",EDGE,{"derivedFrom":[makeQuery(id+"F58.boolean.opBoolean","MERGE",EDGE,{"derivedFrom":[makeQuery(id+"F50.opExtrude","CAP_EDGE",EDGE,{"disambiguationData":[OSD([sQuery(id+"F49.wireOp",EDGE,"E351.top")])],"isStart":false}),makeQuery(id+"F58.opExtrude","SWEPT_EDGE",EDGE,{"disambiguationData":[OSD([subQ1,subQ0])]})]}),makeQuery(id+"F59.opExtrude","SWEPT_EDGE",EDGE,{"disambiguationData":[OSD([subQ1,subQ0])]})]});}
            var Q1;
            {var subQ0=sQuery(id+"F60.wireOp",EDGE,"E355.right");var subQ1=sQuery(id+"F60.wireOp",EDGE,"E355.bottom");Q1=makeQuery(id+"F62.boolean.opBoolean","MERGE",EDGE,{"derivedFrom":[makeQuery(id+"F61.boolean.opBoolean","MERGE",EDGE,{"derivedFrom":[makeQuery(id+"F55.opExtrude","CAP_EDGE",EDGE,{"disambiguationData":[OSD([sQuery(id+"F54.wireOp",EDGE,"E353.top")])],"isStart":false}),makeQuery(id+"F61.opExtrude","SWEPT_EDGE",EDGE,{"disambiguationData":[OSD([subQ1,subQ0])]})]}),makeQuery(id+"F62.opExtrude","SWEPT_EDGE",EDGE,{"disambiguationData":[OSD([subQ1,subQ0])]})]});}
            fillet(context, id + "F69", {"entities" : qUnion([Q0, Q1]), "radius" : 5.08 * mm, "tangentPropagation" : true, "allowEdgeOverflow" : false});
        }
        {
            var Q0;
            Q0=makeQuery(id+"F41.opExtrude","SWEPT_FACE",FACE,{"disambiguationData":[OSD([sQuery(id+"F40.wireOp",EDGE,"E341.right")])]});
            var sketch = newSketch(context, id + "F70", { "sketchPlane" : qUnion([Q0])});
            skLineSegment(sketch, "E356.bottom", {"start": v(-431.8, 533.4) * mm, "end": v(-203.2, 533.4) * mm});
            skLineSegment(sketch, "E356.top", {"start": v(-431.8, 520.7) * mm, "end": v(-203.2, 520.7) * mm});
            skLineSegment(sketch, "E356.left", {"start": v(-431.8, 533.4) * mm, "end": v(-431.8, 520.7) * mm});
            skLineSegment(sketch, "E356.right", {"start": v(-203.2, 533.4) * mm, "end": v(-203.2, 520.7) * mm});
            skSolve(sketch);
        }
        {
            var Q0;
            Q0=makeQuery(id+"F70.imprint","IMPRINT",FACE,{"disambiguationData":[TD([[makeQuery(id+"F70.imprint","IMPRINT",EDGE,{"derivedFrom":sQuery(id+"F70.wireOp",EDGE,"E356.bottom")}),-1.0]])]});
            extrude(context, id + "F71", {"entities" : qUnion([Q0]), "operationType" : NewBodyOperationType.ADD, "depth" : 767.08 * mm, "offsetDistance" : 25.4 * mm});
        }
        {
            var Q0;
            Q0=makeQuery(id+"F39.opExtrude","SWEPT_FACE",FACE,{"disambiguationData":[OSD([sQuery(id+"F37.wireOp",EDGE,"E334.top"),sQuery(id+"F37.wireOp",EDGE,"E336.bottom"),sQuery(id+"F37.wireOp",EDGE,"E337.bottom")])]});
            var sketch = newSketch(context, id + "F72", { "sketchPlane" : qUnion([Q0])});
            skLineSegment(sketch, "E357.bottom", {"start": v(452.12, -426.72) * mm, "end": v(375.92, -426.72) * mm});
            skLineSegment(sketch, "E357.left", {"start": v(452.12, -426.72) * mm, "end": v(452.12, -223.52) * mm});
            skCircle(sketch, "E358", {"center": v(375.92, -223.52) * mm, "radius": 38.1 * mm});
            skCircle(sketch, "E359", {"center": v(375.92, -223.52) * mm, "radius": 44.45 * mm});
            skSolve(sketch);
        }
        {
            var Q0;
            Q0=makeQuery(id+"F72.imprint","IMPRINT",FACE,{"disambiguationData":[TD([[makeQuery(id+"F72.imprint","IMPRINT",EDGE,{"derivedFrom":sQuery(id+"F72.wireOp",EDGE,"E358")}),1.0]])]});
            extrude(context, id + "F73", {"entities" : qUnion([Q0]), "operationType" : NewBodyOperationType.REMOVE, "oppositeDirection" : true, "depth" : 10.16 * mm, "offsetDistance" : 25.4 * mm});
        }
        {
            var Q0;
            Q0=makeQuery(id+"F72.imprint","IMPRINT",FACE,{"disambiguationData":[TD([[makeQuery(id+"F72.imprint","IMPRINT",EDGE,{"derivedFrom":sQuery(id+"F72.wireOp",EDGE,"E358")}),-1.0]])]});
            extrude(context, id + "F74", {"entities" : qUnion([Q0]), "operationType" : NewBodyOperationType.ADD, "depth" : 15.24 * mm, "offsetDistance" : 25.4 * mm});
        }
        {
            var Q0;
            Q0=makeQuery(id+"F74.opExtrude","CAP_EDGE",EDGE,{"disambiguationData":[OSD([sQuery(id+"F72.wireOp",EDGE,"E359")])],"isStart":false});
            fillet(context, id + "F75", {"entities" : qUnion([Q0]), "radius" : 5.08 * mm, "tangentPropagation" : true, "allowEdgeOverflow" : false});
        }
    });
